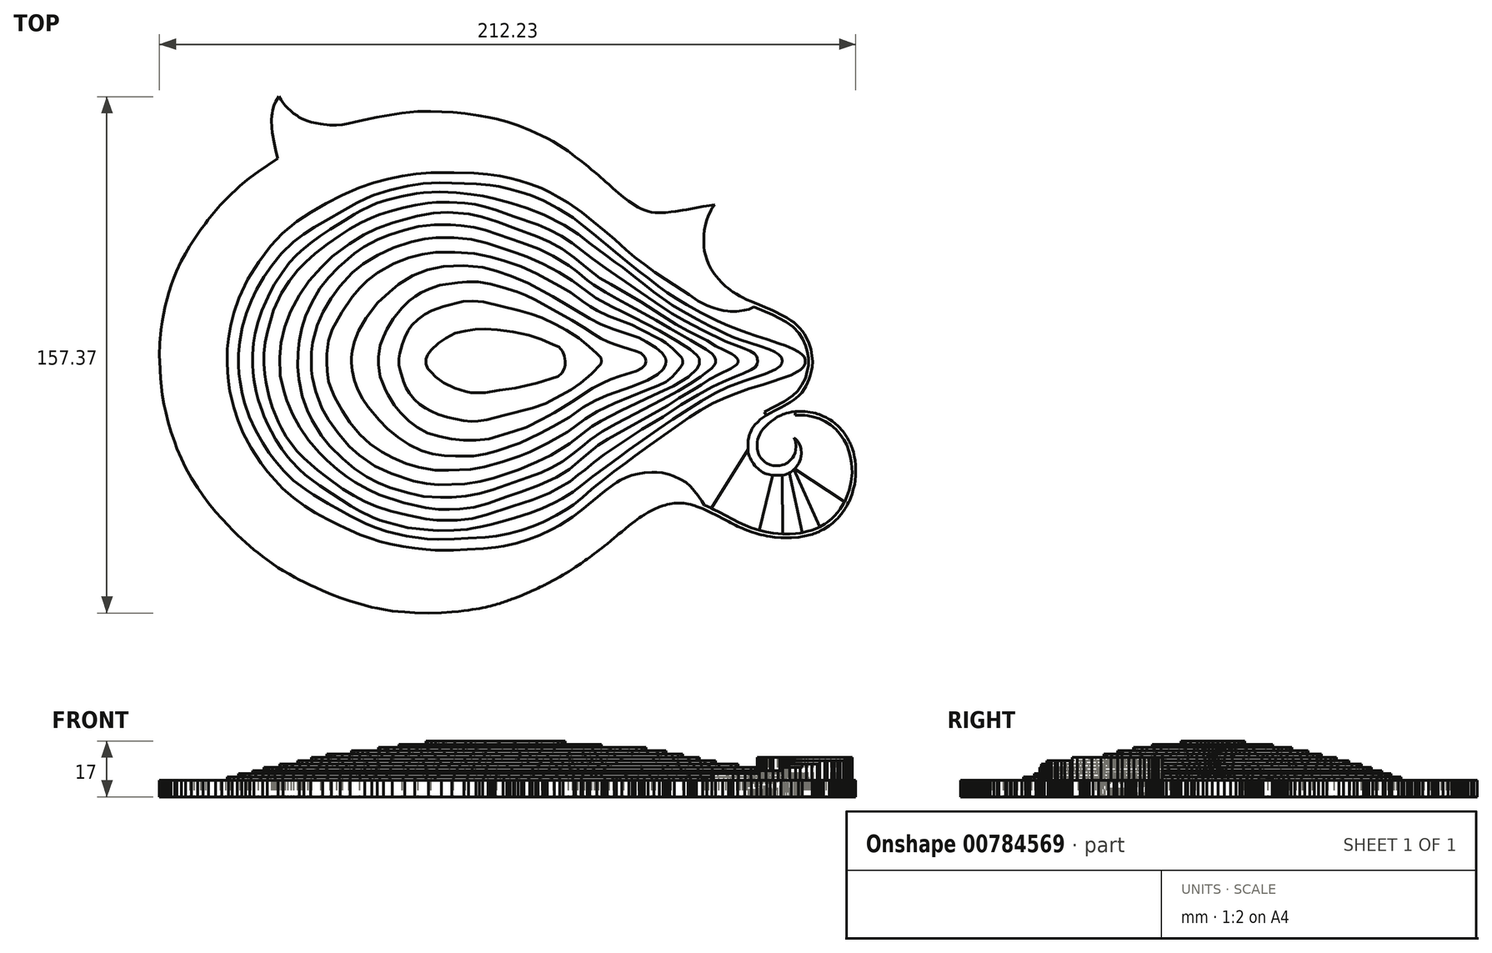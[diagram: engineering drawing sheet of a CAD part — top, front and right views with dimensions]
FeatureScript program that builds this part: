
annotation { "Feature Type Name" : "Feature", "Feature Type Description" : "" }
export const myFeature = defineFeature(function(context is Context, id is Id, definition is map)
    precondition{}
    {
        {
            var Q0;
            Q0=qCreatedBy(makeId("Top.planeOp"),FACE);
            var sketch = newSketch(context, id + "F0", { "sketchPlane" : qUnion([Q0])});
            skLineSegment(sketch, "E0.MirrorCS", {"start": v(99.6, -273.9) * mm, "end": v(99.87, -273.72) * mm});
            skLineSegment(sketch, "E1.MirrorCS", {"start": v(99.87, -273.72) * mm, "end": v(100.2, -273.5) * mm});
            skLineSegment(sketch, "E2.MirrorCS", {"start": v(90.61, -246.87) * mm, "end": v(90.25, -246.1) * mm});
            skLineSegment(sketch, "E3.MirrorCS", {"start": v(97.35, -275.01) * mm, "end": v(97.85, -274.82) * mm});
            skLineSegment(sketch, "E4.MirrorCS", {"start": v(89.29, -252.91) * mm, "end": v(89.86, -252.2) * mm});
            skLineSegment(sketch, "E5.MirrorCS", {"start": v(95.23, -275.73) * mm, "end": v(95.84, -275.58) * mm});
            skLineSegment(sketch, "E6.MirrorCS", {"start": v(101.86, -270.8) * mm, "end": v(102.62, -270) * mm});
            skLineSegment(sketch, "E7.MirrorCS", {"start": v(106.09, -267.45) * mm, "end": v(106.36, -266.93) * mm});
            skLineSegment(sketch, "E8.MirrorCS", {"start": v(100.2, -273.5) * mm, "end": v(100.44, -273.35) * mm});
            skLineSegment(sketch, "E9.MirrorCS", {"start": v(90.25, -246.1) * mm, "end": v(90.81, -246.52) * mm});
            skLineSegment(sketch, "E10.MirrorCS", {"start": v(104.72, -269.4) * mm, "end": v(105.05, -268.97) * mm});
            skLineSegment(sketch, "E11.MirrorCS", {"start": v(108.03, -263.16) * mm, "end": v(108.19, -262.59) * mm});
            skLineSegment(sketch, "E12.MirrorCS", {"start": v(97.85, -274.82) * mm, "end": v(98.18, -274.6) * mm});
            skLineSegment(sketch, "E13.MirrorCS", {"start": v(90.61, -250.7) * mm, "end": v(90.8, -249.93) * mm});
            skLineSegment(sketch, "E14.MirrorCS", {"start": v(103.58, -270.74) * mm, "end": v(103.97, -270.34) * mm});
            skLineSegment(sketch, "E15.MirrorCS", {"start": v(89.86, -252.2) * mm, "end": v(90.22, -251.64) * mm});
            skLineSegment(sketch, "E16.MirrorCS", {"start": v(95.84, -275.58) * mm, "end": v(96.38, -275.37) * mm});
            skLineSegment(sketch, "E17.MirrorCS", {"start": v(102.45, -271.83) * mm, "end": v(102.83, -271.47) * mm});
            skLineSegment(sketch, "E18.MirrorCS", {"start": v(107.11, -265.56) * mm, "end": v(107.27, -265.15) * mm});
            skLineSegment(sketch, "E19.MirrorCS", {"start": v(3.33, -295.73) * mm, "end": v(3.76, -295.55) * mm});
            skLineSegment(sketch, "E20.MirrorCS", {"start": v(106.36, -266.93) * mm, "end": v(106.56, -266.53) * mm});
            skLineSegment(sketch, "E21.MirrorCS", {"start": v(91.71, -247.61) * mm, "end": v(92.2, -248.6) * mm});
            skLineSegment(sketch, "E22.MirrorCS", {"start": v(76.9, -244.77) * mm, "end": v(77.11, -244.24) * mm});
            skLineSegment(sketch, "E23.MirrorCS", {"start": v(100.44, -273.35) * mm, "end": v(100.76, -273.14) * mm});
            skLineSegment(sketch, "E24.MirrorCS", {"start": v(105.8, -267.9) * mm, "end": v(106.09, -267.45) * mm});
            skLineSegment(sketch, "E25.MirrorCS", {"start": v(91.16, -246.85) * mm, "end": v(91.38, -247.1) * mm});
            skLineSegment(sketch, "E26.MirrorCS", {"start": v(90.81, -246.52) * mm, "end": v(91.16, -246.85) * mm});
            skLineSegment(sketch, "E27.MirrorCS", {"start": v(82.4, -241.9) * mm, "end": v(81.84, -242.5) * mm});
            skLineSegment(sketch, "E28.MirrorCS", {"start": v(105.05, -268.97) * mm, "end": v(105.27, -268.64) * mm});
            skLineSegment(sketch, "E29.MirrorCS", {"start": v(106.88, -246.87) * mm, "end": v(106.51, -246.12) * mm});
            skLineSegment(sketch, "E30.MirrorCS", {"start": v(108.58, -261.1) * mm, "end": v(108.77, -260.34) * mm});
            skLineSegment(sketch, "E31.MirrorCS", {"start": v(81.3, -238.26) * mm, "end": v(82.28, -237.75) * mm});
            skLineSegment(sketch, "E32.MirrorCS", {"start": v(90.8, -247.4) * mm, "end": v(90.61, -246.87) * mm});
            skLineSegment(sketch, "E33.MirrorCS", {"start": v(92.13, -275.21) * mm, "end": v(92.88, -275.05) * mm});
            skLineSegment(sketch, "E34.MirrorCS", {"start": v(90.98, -248.7) * mm, "end": v(90.8, -247.4) * mm});
            skLineSegment(sketch, "E35.MirrorCS", {"start": v(108.19, -262.59) * mm, "end": v(108.38, -261.85) * mm});
            skLineSegment(sketch, "E36.MirrorCS", {"start": v(84.64, -240.23) * mm, "end": v(84.04, -240.62) * mm});
            skLineSegment(sketch, "E37.MirrorCS", {"start": v(98.18, -274.6) * mm, "end": v(98.93, -274.27) * mm});
            skLineSegment(sketch, "E38.MirrorCS", {"start": v(83.02, -238.7) * mm, "end": v(84.5, -237.95) * mm});
            skLineSegment(sketch, "E39.MirrorCS", {"start": v(90.8, -249.93) * mm, "end": v(90.98, -248.7) * mm});
            skLineSegment(sketch, "E40.MirrorCS", {"start": v(103.97, -270.34) * mm, "end": v(104.3, -270) * mm});
            skLineSegment(sketch, "E41.MirrorCS", {"start": v(81.92, -239.26) * mm, "end": v(83.02, -238.7) * mm});
            skLineSegment(sketch, "E42.MirrorCS", {"start": v(95.82, -224.6) * mm, "end": v(95.98, -222.96) * mm});
            skLineSegment(sketch, "E43.MirrorCS", {"start": v(107.82, -263.72) * mm, "end": v(108.03, -263.16) * mm});
            skLineSegment(sketch, "E44.MirrorCS", {"start": v(94.48, -239.43) * mm, "end": v(93.59, -239.33) * mm});
            skLineSegment(sketch, "E45.MirrorCS", {"start": v(90.22, -251.64) * mm, "end": v(90.61, -250.7) * mm});
            skLineSegment(sketch, "E46.MirrorCS", {"start": v(86.9, -239.1) * mm, "end": v(86.52, -239.26) * mm});
            skLineSegment(sketch, "E47.MirrorCS", {"start": v(107.27, -265.15) * mm, "end": v(107.48, -264.6) * mm});
            skLineSegment(sketch, "E48.MirrorCS", {"start": v(108.01, -249.29) * mm, "end": v(107.83, -248.86) * mm});
            skLineSegment(sketch, "E49.MirrorCS", {"start": v(96.38, -275.37) * mm, "end": v(96.9, -275.2) * mm});
            skLineSegment(sketch, "E50.MirrorCS", {"start": v(102.83, -271.47) * mm, "end": v(103.22, -271.1) * mm});
            skLineSegment(sketch, "E51.MirrorCS", {"start": v(3.76, -295.55) * mm, "end": v(4.3, -295.36) * mm});
            skLineSegment(sketch, "E52.MirrorCS", {"start": v(94.86, -228.32) * mm, "end": v(95.23, -227.18) * mm});
            skLineSegment(sketch, "E53.MirrorCS", {"start": v(104.4, -267.86) * mm, "end": v(105.38, -266.22) * mm});
            skLineSegment(sketch, "E54.MirrorCS", {"start": v(92.62, -250.96) * mm, "end": v(92.3, -252.6) * mm});
            skLineSegment(sketch, "E55.MirrorCS", {"start": v(88.77, -238.5) * mm, "end": v(88, -238.69) * mm});
            skLineSegment(sketch, "E56.MirrorCS", {"start": v(103.59, -268.9) * mm, "end": v(104.4, -267.86) * mm});
            skLineSegment(sketch, "E57.MirrorCS", {"start": v(92.49, -249.48) * mm, "end": v(92.62, -250.96) * mm});
            skLineSegment(sketch, "E58.MirrorCS", {"start": v(93.95, -230.35) * mm, "end": v(94.5, -229.25) * mm});
            skLineSegment(sketch, "E59.MirrorCS", {"start": v(89.67, -238.32) * mm, "end": v(88.77, -238.5) * mm});
            skLineSegment(sketch, "E60.MirrorCS", {"start": v(94.53, -275.9) * mm, "end": v(95.23, -275.73) * mm});
            skLineSegment(sketch, "E61.MirrorCS", {"start": v(101.53, -272.59) * mm, "end": v(102.06, -272.15) * mm});
            skLineSegment(sketch, "E62.MirrorCS", {"start": v(106.56, -266.53) * mm, "end": v(106.9, -265.9) * mm});
            skLineSegment(sketch, "E63.MirrorCS", {"start": v(108.55, -251.1) * mm, "end": v(108.4, -250.5) * mm});
            skLineSegment(sketch, "E64.MirrorCS", {"start": v(2.24, -296.12) * mm, "end": v(2.77, -295.92) * mm});
            skLineSegment(sketch, "E65.MirrorCS", {"start": v(93.8, -227.93) * mm, "end": v(94.39, -225.67) * mm});
            skLineSegment(sketch, "E66.MirrorCS", {"start": v(90.62, -238.15) * mm, "end": v(89.67, -238.32) * mm});
            skLineSegment(sketch, "E67.MirrorCS", {"start": v(92.2, -248.6) * mm, "end": v(92.49, -249.48) * mm});
            skLineSegment(sketch, "E68.MirrorCS", {"start": v(80.77, -256.67) * mm, "end": v(80.27, -256.3) * mm});
            skLineSegment(sketch, "E69.MirrorCS", {"start": v(77.11, -244.24) * mm, "end": v(77.28, -243.86) * mm});
            skLineSegment(sketch, "E70.MirrorCS", {"start": v(100.76, -273.14) * mm, "end": v(101.02, -272.97) * mm});
            skLineSegment(sketch, "E71.MirrorCS", {"start": v(105.25, -244.28) * mm, "end": v(104.87, -243.87) * mm});
            skLineSegment(sketch, "E72.MirrorCS", {"start": v(99.69, -272.45) * mm, "end": v(100.48, -271.9) * mm});
            skLineSegment(sketch, "E73.MirrorCS", {"start": v(91.38, -247.1) * mm, "end": v(91.71, -247.61) * mm});
            skLineSegment(sketch, "E74.MirrorCS", {"start": v(91.65, -276.49) * mm, "end": v(92.87, -276.3) * mm});
            skLineSegment(sketch, "E75.MirrorCS", {"start": v(96.17, -238.52) * mm, "end": v(95.23, -238.36) * mm});
            skLineSegment(sketch, "E76.MirrorCS", {"start": v(96.9, -238.71) * mm, "end": v(96.17, -238.52) * mm});
            skLineSegment(sketch, "E77.MirrorCS", {"start": v(81.84, -242.5) * mm, "end": v(81, -243.32) * mm});
            skLineSegment(sketch, "E78.MirrorCS", {"start": v(105.27, -268.64) * mm, "end": v(105.47, -268.33) * mm});
            skLineSegment(sketch, "E79.MirrorCS", {"start": v(-0.71, -297.05) * mm, "end": v(-0.14, -296.88) * mm});
            skLineSegment(sketch, "E80.MirrorCS", {"start": v(97.38, -273.66) * mm, "end": v(98.18, -273.35) * mm});
            skLineSegment(sketch, "E81.MirrorCS", {"start": v(90.23, -234.62) * mm, "end": v(90.97, -234.07) * mm});
            skLineSegment(sketch, "E82.MirrorCS", {"start": v(106.51, -246.12) * mm, "end": v(106.17, -245.6) * mm});
            skLineSegment(sketch, "E83.MirrorCS", {"start": v(108.77, -260.34) * mm, "end": v(108.94, -259.25) * mm});
            skLineSegment(sketch, "E84.MirrorCS", {"start": v(89.12, -235.38) * mm, "end": v(90.23, -234.62) * mm});
            skLineSegment(sketch, "E85.MirrorCS", {"start": v(98.03, -239.06) * mm, "end": v(97.46, -238.86) * mm});
            skLineSegment(sketch, "E86.MirrorCS", {"start": v(81.92, -253.9) * mm, "end": v(82.64, -254.23) * mm});
            skLineSegment(sketch, "E87.MirrorCS", {"start": v(99.32, -274.09) * mm, "end": v(99.6, -273.9) * mm});
            skLineSegment(sketch, "E88.MirrorCS", {"start": v(-2.2, -297.42) * mm, "end": v(-1.47, -297.24) * mm});
            skLineSegment(sketch, "E89.MirrorCS", {"start": v(81.92, -239.26) * mm, "end": v(81.3, -238.26) * mm});
            skLineSegment(sketch, "E90.MirrorCS", {"start": v(92.88, -275.05) * mm, "end": v(94.15, -274.78) * mm});
            skLineSegment(sketch, "E91.MirrorCS", {"start": v(86.54, -236.85) * mm, "end": v(89.12, -235.38) * mm});
            skLineSegment(sketch, "E92.MirrorCS", {"start": v(108.38, -261.85) * mm, "end": v(108.58, -261.1) * mm});
            skLineSegment(sketch, "E93.MirrorCS", {"start": v(84.04, -240.62) * mm, "end": v(83.28, -241.18) * mm});
            skLineSegment(sketch, "E94.MirrorCS", {"start": v(98.93, -274.27) * mm, "end": v(99.32, -274.09) * mm});
            skLineSegment(sketch, "E95.MirrorCS", {"start": v(104.54, -269.62) * mm, "end": v(104.72, -269.4) * mm});
            skLineSegment(sketch, "E96.MirrorCS", {"start": v(90.62, -239.35) * mm, "end": v(90.62, -238.15) * mm});
            skLineSegment(sketch, "E97.MirrorCS", {"start": v(84.5, -237.95) * mm, "end": v(86.54, -236.85) * mm});
            skLineSegment(sketch, "E98.MirrorCS", {"start": v(95.8, -221.16) * mm, "end": v(95.45, -219.22) * mm});
            skLineSegment(sketch, "E99.MirrorCS", {"start": v(80.97, -253.15) * mm, "end": v(81.37, -253.53) * mm});
            skLineSegment(sketch, "E100.MirrorCS", {"start": v(104.3, -270) * mm, "end": v(104.54, -269.62) * mm});
            skLineSegment(sketch, "E101.MirrorCS", {"start": v(-3.73, -297.78) * mm, "end": v(-2.94, -297.6) * mm});
            skLineSegment(sketch, "E102.MirrorCS", {"start": v(99.71, -227.6) * mm, "end": v(100.8, -227.29) * mm});
            skLineSegment(sketch, "E103.MirrorCS", {"start": v(107.12, -262) * mm, "end": v(107.65, -259.57) * mm});
            skLineSegment(sketch, "E104.MirrorCS", {"start": v(91.95, -239.27) * mm, "end": v(90.62, -239.35) * mm});
            skLineSegment(sketch, "E105.MirrorCS", {"start": v(95.98, -222.96) * mm, "end": v(95.8, -221.16) * mm});
            skLineSegment(sketch, "E106.MirrorCS", {"start": v(107.45, -247.97) * mm, "end": v(107.27, -247.56) * mm});
            skLineSegment(sketch, "E107.MirrorCS", {"start": v(85.24, -239.83) * mm, "end": v(84.64, -240.23) * mm});
            skLineSegment(sketch, "E108.MirrorCS", {"start": v(106.42, -264.05) * mm, "end": v(107.12, -262) * mm});
            skLineSegment(sketch, "E109.MirrorCS", {"start": v(93.59, -239.33) * mm, "end": v(91.95, -239.27) * mm});
            skLineSegment(sketch, "E110.MirrorCS", {"start": v(79.86, -251.83) * mm, "end": v(80.23, -252.4) * mm});
            skLineSegment(sketch, "E111.MirrorCS", {"start": v(77.36, -253.15) * mm, "end": v(76.92, -252.28) * mm});
            skLineSegment(sketch, "E112.MirrorCS", {"start": v(95.1, -227.6) * mm, "end": v(99.71, -227.6) * mm});
            skLineSegment(sketch, "E113.MirrorCS", {"start": v(86.52, -239.26) * mm, "end": v(85.24, -239.83) * mm});
            skLineSegment(sketch, "E114.MirrorCS", {"start": v(105.75, -265.65) * mm, "end": v(106.42, -264.05) * mm});
            skLineSegment(sketch, "E115.MirrorCS", {"start": v(95.64, -225.7) * mm, "end": v(95.82, -224.6) * mm});
            skLineSegment(sketch, "E116.MirrorCS", {"start": v(107.48, -264.6) * mm, "end": v(107.82, -263.72) * mm});
            skLineSegment(sketch, "E117.MirrorCS", {"start": v(107.83, -248.86) * mm, "end": v(107.62, -248.34) * mm});
            skLineSegment(sketch, "E118.MirrorCS", {"start": v(96.9, -275.2) * mm, "end": v(97.35, -275.01) * mm});
            skLineSegment(sketch, "E119.MirrorCS", {"start": v(103.22, -271.1) * mm, "end": v(103.58, -270.74) * mm});
            skLineSegment(sketch, "E120.MirrorCS", {"start": v(4.3, -295.36) * mm, "end": v(4.8, -295.17) * mm});
            skLineSegment(sketch, "E121.MirrorCS", {"start": v(79.3, -241.27) * mm, "end": v(80.05, -240.58) * mm});
            skLineSegment(sketch, "E122.MirrorCS", {"start": v(95.23, -227.18) * mm, "end": v(95.64, -225.7) * mm});
            skLineSegment(sketch, "E123.MirrorCS", {"start": v(79.3, -250.57) * mm, "end": v(79.48, -251.07) * mm});
            skLineSegment(sketch, "E124.MirrorCS", {"start": v(78.38, -254.64) * mm, "end": v(77.95, -254.05) * mm});
            skLineSegment(sketch, "E125.MirrorCS", {"start": v(87.42, -238.88) * mm, "end": v(86.9, -239.1) * mm});
            skLineSegment(sketch, "E126.MirrorCS", {"start": v(105.38, -266.22) * mm, "end": v(105.75, -265.65) * mm});
            skLineSegment(sketch, "E127.MirrorCS", {"start": v(96.16, -239.75) * mm, "end": v(94.48, -239.43) * mm});
            skLineSegment(sketch, "E128.MirrorCS", {"start": v(94.79, -221.9) * mm, "end": v(94.3, -219.9) * mm});
            skLineSegment(sketch, "E129.MirrorCS", {"start": v(88, -238.69) * mm, "end": v(87.42, -238.88) * mm});
            skLineSegment(sketch, "E130.MirrorCS", {"start": v(79.11, -249.6) * mm, "end": v(79.3, -250.57) * mm});
            skLineSegment(sketch, "E131.MirrorCS", {"start": v(94.7, -224.21) * mm, "end": v(94.79, -221.9) * mm});
            skLineSegment(sketch, "E132.MirrorCS", {"start": v(94.5, -229.25) * mm, "end": v(94.86, -228.32) * mm});
            skLineSegment(sketch, "E133.MirrorCS", {"start": v(102.06, -272.15) * mm, "end": v(102.45, -271.83) * mm});
            skLineSegment(sketch, "E134.MirrorCS", {"start": v(106.9, -265.9) * mm, "end": v(107.11, -265.56) * mm});
            skLineSegment(sketch, "E135.MirrorCS", {"start": v(108.4, -250.5) * mm, "end": v(108.2, -249.88) * mm});
            skLineSegment(sketch, "E136.MirrorCS", {"start": v(2.77, -295.92) * mm, "end": v(3.33, -295.73) * mm});
            skLineSegment(sketch, "E137.MirrorCS", {"start": v(94.39, -225.67) * mm, "end": v(94.7, -224.21) * mm});
            skLineSegment(sketch, "E138.MirrorCS", {"start": v(98.18, -273.35) * mm, "end": v(98.56, -274.43) * mm});
            skLineSegment(sketch, "E139.MirrorCS", {"start": v(80.27, -256.3) * mm, "end": v(79.74, -255.91) * mm});
            skLineSegment(sketch, "E140.MirrorCS", {"start": v(77.28, -243.86) * mm, "end": v(77.49, -243.47) * mm});
            skLineSegment(sketch, "E141.MirrorCS", {"start": v(104.1, -243.03) * mm, "end": v(103.71, -242.63) * mm});
            skLineSegment(sketch, "E142.MirrorCS", {"start": v(102.62, -270) * mm, "end": v(103.59, -268.9) * mm});
            skLineSegment(sketch, "E143.MirrorCS", {"start": v(79.5, -246.07) * mm, "end": v(79.3, -246.67) * mm});
            skLineSegment(sketch, "E144.MirrorCS", {"start": v(87.46, -254.25) * mm, "end": v(87.84, -254.08) * mm});
            skLineSegment(sketch, "E145.MirrorCS", {"start": v(93.77, -276.08) * mm, "end": v(94.53, -275.9) * mm});
            skLineSegment(sketch, "E146.MirrorCS", {"start": v(101.02, -272.97) * mm, "end": v(101.53, -272.59) * mm});
            skLineSegment(sketch, "E147.MirrorCS", {"start": v(92.76, -230) * mm, "end": v(93.8, -227.93) * mm});
            skLineSegment(sketch, "E148.MirrorCS", {"start": v(92.87, -276.3) * mm, "end": v(93.77, -276.08) * mm});
            skLineSegment(sketch, "E149.MirrorCS", {"start": v(100.48, -271.9) * mm, "end": v(101.86, -270.8) * mm});
            skLineSegment(sketch, "E150.MirrorCS", {"start": v(104.2, -244.95) * mm, "end": v(103.05, -243.67) * mm});
            skLineSegment(sketch, "E151.MirrorCS", {"start": v(93.74, -238.15) * mm, "end": v(90.62, -238.15) * mm});
            skLineSegment(sketch, "E152.MirrorCS", {"start": v(65.18, -267.67) * mm, "end": v(64.5, -268.73) * mm});
            skLineSegment(sketch, "E153.MirrorCS", {"start": v(82.07, -257.18) * mm, "end": v(81.5, -257.02) * mm});
            skLineSegment(sketch, "E154.MirrorCS", {"start": v(95.23, -238.36) * mm, "end": v(93.74, -238.15) * mm});
            skLineSegment(sketch, "E155.MirrorCS", {"start": v(80.42, -244.1) * mm, "end": v(79.86, -245.14) * mm});
            skLineSegment(sketch, "E156.MirrorCS", {"start": v(85.97, -254.63) * mm, "end": v(86.9, -254.44) * mm});
            skLineSegment(sketch, "E157.MirrorCS", {"start": v(87.4, -235.1) * mm, "end": v(89.9, -233.35) * mm});
            skLineSegment(sketch, "E158.MirrorCS", {"start": v(98.18, -273.35) * mm, "end": v(99.69, -272.45) * mm});
            skLineSegment(sketch, "E159.MirrorCS", {"start": v(-0.14, -296.88) * mm, "end": v(0.57, -296.66) * mm});
            skLineSegment(sketch, "E160.MirrorCS", {"start": v(105.78, -245) * mm, "end": v(105.6, -244.81) * mm});
            skLineSegment(sketch, "E161.MirrorCS", {"start": v(81, -243.32) * mm, "end": v(80.42, -244.1) * mm});
            skLineSegment(sketch, "E162.MirrorCS", {"start": v(105.47, -268.33) * mm, "end": v(105.8, -267.9) * mm});
            skLineSegment(sketch, "E163.MirrorCS", {"start": v(76.35, -247.04) * mm, "end": v(76.53, -245.94) * mm});
            skLineSegment(sketch, "E164.MirrorCS", {"start": v(90.97, -234.07) * mm, "end": v(91.76, -233.38) * mm});
            skLineSegment(sketch, "E165.MirrorCS", {"start": v(106.17, -245.6) * mm, "end": v(105.78, -245) * mm});
            skLineSegment(sketch, "E166.MirrorCS", {"start": v(84.64, -236.53) * mm, "end": v(87.4, -235.1) * mm});
            skLineSegment(sketch, "E167.MirrorCS", {"start": v(97.46, -238.86) * mm, "end": v(96.9, -238.71) * mm});
            skLineSegment(sketch, "E168.MirrorCS", {"start": v(82.64, -254.23) * mm, "end": v(83.04, -254.43) * mm});
            skLineSegment(sketch, "E169.MirrorCS", {"start": v(-1.47, -297.24) * mm, "end": v(-0.71, -297.05) * mm});
            skLineSegment(sketch, "E170.MirrorCS", {"start": v(82.28, -237.75) * mm, "end": v(84.64, -236.53) * mm});
            skLineSegment(sketch, "E171.MirrorCS", {"start": v(95.73, -274.34) * mm, "end": v(97.38, -273.66) * mm});
            skLineSegment(sketch, "E172.MirrorCS", {"start": v(87.47, -257.42) * mm, "end": v(86.72, -257.6) * mm});
            skLineSegment(sketch, "E173.MirrorCS", {"start": v(76.35, -250.37) * mm, "end": v(76.35, -249.7) * mm});
            skLineSegment(sketch, "E174.MirrorCS", {"start": v(83.28, -241.18) * mm, "end": v(82.4, -241.9) * mm});
            skLineSegment(sketch, "E175.MirrorCS", {"start": v(94.15, -274.78) * mm, "end": v(95.73, -274.34) * mm});
            skLineSegment(sketch, "E176.MirrorCS", {"start": v(81.37, -253.53) * mm, "end": v(81.92, -253.9) * mm});
            skLineSegment(sketch, "E177.MirrorCS", {"start": v(88.56, -257.01) * mm, "end": v(87.47, -257.42) * mm});
            skLineSegment(sketch, "E178.MirrorCS", {"start": v(76.5, -251.1) * mm, "end": v(76.35, -250.37) * mm});
            skLineSegment(sketch, "E179.MirrorCS", {"start": v(107.08, -247.18) * mm, "end": v(106.88, -246.87) * mm});
            skLineSegment(sketch, "E180.MirrorCS", {"start": v(98.56, -239.26) * mm, "end": v(98.03, -239.06) * mm});
            skLineSegment(sketch, "E181.MirrorCS", {"start": v(-2.94, -297.6) * mm, "end": v(-2.2, -297.42) * mm});
            skLineSegment(sketch, "E182.MirrorCS", {"start": v(76.73, -251.83) * mm, "end": v(76.5, -251.1) * mm});
            skLineSegment(sketch, "E183.MirrorCS", {"start": v(107.27, -247.56) * mm, "end": v(107.08, -247.18) * mm});
            skLineSegment(sketch, "E184.MirrorCS", {"start": v(67.47, -270.2) * mm, "end": v(68.58, -270.76) * mm});
            skLineSegment(sketch, "E185.MirrorCS", {"start": v(6.15, -294.64) * mm, "end": v(7.18, -294.24) * mm});
            skLineSegment(sketch, "E186.MirrorCS", {"start": v(80.23, -252.4) * mm, "end": v(80.97, -253.15) * mm});
            skLineSegment(sketch, "E187.MirrorCS", {"start": v(76.92, -252.28) * mm, "end": v(76.73, -251.83) * mm});
            skLineSegment(sketch, "E188.MirrorCS", {"start": v(5.22, -295.01) * mm, "end": v(6.15, -294.64) * mm});
            skLineSegment(sketch, "E189.MirrorCS", {"start": v(-4.64, -297.99) * mm, "end": v(-3.73, -297.78) * mm});
            skLineSegment(sketch, "E190.MirrorCS", {"start": v(90.55, -255.66) * mm, "end": v(89.89, -256.23) * mm});
            skLineSegment(sketch, "E191.MirrorCS", {"start": v(107.62, -248.34) * mm, "end": v(107.45, -247.97) * mm});
            skLineSegment(sketch, "E192.MirrorCS", {"start": v(100.79, -240.38) * mm, "end": v(100.06, -239.99) * mm});
            skLineSegment(sketch, "E193.MirrorCS", {"start": v(4.8, -295.17) * mm, "end": v(5.22, -295.01) * mm});
            skLineSegment(sketch, "E194.MirrorCS", {"start": v(80.05, -240.58) * mm, "end": v(81.92, -239.26) * mm});
            skLineSegment(sketch, "E195.MirrorCS", {"start": v(79.48, -251.07) * mm, "end": v(79.86, -251.83) * mm});
            skLineSegment(sketch, "E196.MirrorCS", {"start": v(77.95, -254.05) * mm, "end": v(77.36, -253.15) * mm});
            skLineSegment(sketch, "E197.MirrorCS", {"start": v(85.52, -275.4) * mm, "end": v(86.83, -275.47) * mm});
            skLineSegment(sketch, "E198.MirrorCS", {"start": v(92.3, -252.6) * mm, "end": v(91.8, -253.92) * mm});
            skLineSegment(sketch, "E199.MirrorCS", {"start": v(79.34, -255.53) * mm, "end": v(78.38, -254.64) * mm});
            skLineSegment(sketch, "E200.MirrorCS", {"start": v(78.37, -242.22) * mm, "end": v(79.3, -241.27) * mm});
            skLineSegment(sketch, "E201.MirrorCS", {"start": v(102.83, -241.84) * mm, "end": v(101.9, -241.13) * mm});
            skLineSegment(sketch, "E202.MirrorCS", {"start": v(108.2, -249.88) * mm, "end": v(108.01, -249.29) * mm});
            skLineSegment(sketch, "E203.MirrorCS", {"start": v(2.25, -294.84) * mm, "end": v(7.3, -292.96) * mm});
            skLineSegment(sketch, "E204.MirrorCS", {"start": v(98.05, -240.3) * mm, "end": v(96.16, -239.75) * mm});
            skLineSegment(sketch, "E205.MirrorCS", {"start": v(79.74, -255.91) * mm, "end": v(79.34, -255.53) * mm});
            skLineSegment(sketch, "E206.MirrorCS", {"start": v(77.49, -243.47) * mm, "end": v(78.37, -242.22) * mm});
            skLineSegment(sketch, "E207.MirrorCS", {"start": v(103.71, -242.63) * mm, "end": v(102.83, -241.84) * mm});
            skLineSegment(sketch, "E208.MirrorCS", {"start": v(79.11, -247.43) * mm, "end": v(79.11, -249.6) * mm});
            skLineSegment(sketch, "E209.MirrorCS", {"start": v(60.6, -267.07) * mm, "end": v(61.14, -267.28) * mm});
            skLineSegment(sketch, "E210.MirrorCS", {"start": v(-2.85, -296.34) * mm, "end": v(2.25, -294.84) * mm});
            skLineSegment(sketch, "E211.MirrorCS", {"start": v(99.77, -241.22) * mm, "end": v(98.05, -240.3) * mm});
            skLineSegment(sketch, "E212.MirrorCS", {"start": v(-66.45, -142.53) * mm, "end": v(-66.63, -142.2) * mm});
            skLineSegment(sketch, "E213.MirrorCS", {"start": v(79.3, -246.67) * mm, "end": v(79.11, -247.43) * mm});
            skLineSegment(sketch, "E214.MirrorCS", {"start": v(87.84, -254.08) * mm, "end": v(88.4, -253.71) * mm});
            skLineSegment(sketch, "E215.MirrorCS", {"start": v(13.73, -291.3) * mm, "end": v(14.1, -291.1) * mm});
            skLineSegment(sketch, "E216.MirrorCS", {"start": v(101.41, -242.2) * mm, "end": v(99.77, -241.22) * mm});
            skLineSegment(sketch, "E217.MirrorCS", {"start": v(104.87, -243.87) * mm, "end": v(104.1, -243.03) * mm});
            skLineSegment(sketch, "E218.MirrorCS", {"start": v(108.76, -251.96) * mm, "end": v(108.55, -251.1) * mm});
            skLineSegment(sketch, "E219.MirrorCS", {"start": v(59.5, -266.66) * mm, "end": v(60.07, -266.88) * mm});
            skLineSegment(sketch, "E220.MirrorCS", {"start": v(1.69, -296.33) * mm, "end": v(2.24, -296.12) * mm});
            skLineSegment(sketch, "E221.MirrorCS", {"start": v(103.05, -243.67) * mm, "end": v(101.41, -242.2) * mm});
            skLineSegment(sketch, "E222.MirrorCS", {"start": v(108.94, -252.95) * mm, "end": v(108.76, -251.96) * mm});
            skLineSegment(sketch, "E223.MirrorCS", {"start": v(58.84, -266.5) * mm, "end": v(59.5, -266.66) * mm});
            skLineSegment(sketch, "E224.MirrorCS", {"start": v(1.1, -296.5) * mm, "end": v(1.69, -296.33) * mm});
            skLineSegment(sketch, "E225.MirrorCS", {"start": v(64.5, -268.73) * mm, "end": v(65.18, -267.67) * mm});
            skLineSegment(sketch, "E226.MirrorCS", {"start": v(-64.78, -144.91) * mm, "end": v(-65.59, -143.92) * mm});
            skLineSegment(sketch, "E227.MirrorCS", {"start": v(81.5, -257.02) * mm, "end": v(80.77, -256.67) * mm});
            skLineSegment(sketch, "E228.MirrorCS", {"start": v(79.86, -245.14) * mm, "end": v(79.5, -246.07) * mm});
            skLineSegment(sketch, "E229.MirrorCS", {"start": v(86.9, -254.44) * mm, "end": v(87.46, -254.25) * mm});
            skLineSegment(sketch, "E230.MirrorCS", {"start": v(0.57, -296.66) * mm, "end": v(1.1, -296.5) * mm});
            skLineSegment(sketch, "E231.MirrorCS", {"start": v(105.5, -246.8) * mm, "end": v(104.2, -244.95) * mm});
            skLineSegment(sketch, "E232.MirrorCS", {"start": v(76.72, -245.27) * mm, "end": v(76.9, -244.77) * mm});
            skLineSegment(sketch, "E233.MirrorCS", {"start": v(105.6, -244.81) * mm, "end": v(105.25, -244.28) * mm});
            skLineSegment(sketch, "E234.MirrorCS", {"start": v(65.75, -267.95) * mm, "end": v(65.18, -267.67) * mm});
            skLineSegment(sketch, "E235.MirrorCS", {"start": v(106.39, -248.36) * mm, "end": v(105.5, -246.8) * mm});
            skLineSegment(sketch, "E236.MirrorCS", {"start": v(82.63, -257.38) * mm, "end": v(82.07, -257.18) * mm});
            skLineSegment(sketch, "E237.MirrorCS", {"start": v(76.53, -245.94) * mm, "end": v(76.72, -245.27) * mm});
            skLineSegment(sketch, "E238.MirrorCS", {"start": v(91.76, -233.38) * mm, "end": v(92.64, -232.4) * mm});
            skLineSegment(sketch, "E239.MirrorCS", {"start": v(83.93, -254.63) * mm, "end": v(85.97, -254.63) * mm});
            skLineSegment(sketch, "E240.MirrorCS", {"start": v(56.75, -266.12) * mm, "end": v(58, -266.3) * mm});
            skLineSegment(sketch, "E241.MirrorCS", {"start": v(83.6, -257.57) * mm, "end": v(82.63, -257.38) * mm});
            skLineSegment(sketch, "E242.MirrorCS", {"start": v(83.04, -254.43) * mm, "end": v(83.93, -254.63) * mm});
            skLineSegment(sketch, "E243.MirrorCS", {"start": v(108.94, -259.25) * mm, "end": v(109.14, -257.55) * mm});
            skLineSegment(sketch, "E244.MirrorCS", {"start": v(62.85, -178.67) * mm, "end": v(63.7, -176.8) * mm});
            skLineSegment(sketch, "E245.MirrorCS", {"start": v(107.06, -250.32) * mm, "end": v(106.39, -248.36) * mm});
            skLineSegment(sketch, "E246.MirrorCS", {"start": v(86.72, -257.6) * mm, "end": v(83.6, -257.57) * mm});
            skLineSegment(sketch, "E247.MirrorCS", {"start": v(76.35, -249.7) * mm, "end": v(76.35, -247.04) * mm});
            skLineSegment(sketch, "E248.MirrorCS", {"start": v(52.44, -266.3) * mm, "end": v(53.83, -266.12) * mm});
            skLineSegment(sketch, "E249.MirrorCS", {"start": v(107.45, -251.72) * mm, "end": v(107.06, -250.32) * mm});
            skLineSegment(sketch, "E250.MirrorCS", {"start": v(69.63, -271.33) * mm, "end": v(70.34, -271.7) * mm});
            skLineSegment(sketch, "E251.MirrorCS", {"start": v(107.85, -253.78) * mm, "end": v(107.45, -251.72) * mm});
            skLineSegment(sketch, "E252.MirrorCS", {"start": v(68.58, -270.76) * mm, "end": v(69.63, -271.33) * mm});
            skLineSegment(sketch, "E253.MirrorCS", {"start": v(107.65, -259.57) * mm, "end": v(108.03, -256.85) * mm});
            skLineSegment(sketch, "E254.MirrorCS", {"start": v(99.32, -239.63) * mm, "end": v(98.56, -239.26) * mm});
            skLineSegment(sketch, "E255.MirrorCS", {"start": v(90.8, -275.38) * mm, "end": v(92.13, -275.21) * mm});
            skLineSegment(sketch, "E256.MirrorCS", {"start": v(65.02, -176.8) * mm, "end": v(65.44, -176.06) * mm});
            skLineSegment(sketch, "E257.MirrorCS", {"start": v(89.89, -256.23) * mm, "end": v(89.28, -256.63) * mm});
            skLineSegment(sketch, "E258.MirrorCS", {"start": v(100.06, -239.99) * mm, "end": v(99.32, -239.63) * mm});
            skLineSegment(sketch, "E259.MirrorCS", {"start": v(66.37, -269.64) * mm, "end": v(67.47, -270.2) * mm});
            skLineSegment(sketch, "E260.MirrorCS", {"start": v(89.04, -275.46) * mm, "end": v(90.8, -275.38) * mm});
            skLineSegment(sketch, "E261.MirrorCS", {"start": v(65.25, -269.1) * mm, "end": v(66.37, -269.64) * mm});
            skLineSegment(sketch, "E262.MirrorCS", {"start": v(-5.54, -298.16) * mm, "end": v(-4.64, -297.99) * mm});
            skLineSegment(sketch, "E263.MirrorCS", {"start": v(86.83, -275.47) * mm, "end": v(89.04, -275.46) * mm});
            skLineSegment(sketch, "E264.MirrorCS", {"start": v(101.34, -240.7) * mm, "end": v(100.79, -240.38) * mm});
            skLineSegment(sketch, "E265.MirrorCS", {"start": v(63.71, -267) * mm, "end": v(65.18, -267.67) * mm});
            skLineSegment(sketch, "E266.MirrorCS", {"start": v(63.76, -268.37) * mm, "end": v(65.25, -269.1) * mm});
            skLineSegment(sketch, "E267.MirrorCS", {"start": v(-6.64, -298.34) * mm, "end": v(-5.54, -298.16) * mm});
            skLineSegment(sketch, "E268.MirrorCS", {"start": v(63.74, -179.76) * mm, "end": v(64.12, -178.68) * mm});
            skLineSegment(sketch, "E269.MirrorCS", {"start": v(91.8, -253.92) * mm, "end": v(91.2, -254.84) * mm});
            skLineSegment(sketch, "E270.MirrorCS", {"start": v(101.9, -241.13) * mm, "end": v(101.34, -240.7) * mm});
            skLineSegment(sketch, "E271.MirrorCS", {"start": v(62.45, -267.78) * mm, "end": v(63.76, -268.37) * mm});
            skLineSegment(sketch, "E272.MirrorCS", {"start": v(61.36, -265.85) * mm, "end": v(63.71, -267) * mm});
            skLineSegment(sketch, "E273.MirrorCS", {"start": v(61.14, -267.28) * mm, "end": v(62.45, -267.78) * mm});
            skLineSegment(sketch, "E274.MirrorCS", {"start": v(58.52, -265.16) * mm, "end": v(61.36, -265.85) * mm});
            skLineSegment(sketch, "E275.MirrorCS", {"start": v(-66.63, -142.2) * mm, "end": v(-67.15, -142.98) * mm});
            skLineSegment(sketch, "E276.MirrorCS", {"start": v(88.4, -253.71) * mm, "end": v(89.29, -252.91) * mm});
            skLineSegment(sketch, "E277.MirrorCS", {"start": v(14.1, -291.1) * mm, "end": v(14.48, -290.92) * mm});
            skLineSegment(sketch, "E278.MirrorCS", {"start": v(55.36, -264.8) * mm, "end": v(58.52, -265.16) * mm});
            skLineSegment(sketch, "E279.MirrorCS", {"start": v(81.75, -274.87) * mm, "end": v(83.87, -275.19) * mm});
            skLineSegment(sketch, "E280.MirrorCS", {"start": v(60.07, -266.88) * mm, "end": v(60.6, -267.07) * mm});
            skLineSegment(sketch, "E281.MirrorCS", {"start": v(52.87, -265.02) * mm, "end": v(55.36, -264.8) * mm});
            skLineSegment(sketch, "E282.MirrorCS", {"start": v(63.02, -182.96) * mm, "end": v(63.2, -182.05) * mm});
            skLineSegment(sketch, "E283.MirrorCS", {"start": v(-65.59, -143.92) * mm, "end": v(-66.09, -143.15) * mm});
            skLineSegment(sketch, "E284.MirrorCS", {"start": v(54.17, -177.17) * mm, "end": v(52.8, -177.37) * mm});
            skLineSegment(sketch, "E285.MirrorCS", {"start": v(93.2, -231.62) * mm, "end": v(93.6, -231.1) * mm});
            skLineSegment(sketch, "E286.MirrorCS", {"start": v(58, -266.3) * mm, "end": v(58.84, -266.5) * mm});
            skLineSegment(sketch, "E287.MirrorCS", {"start": v(92.64, -232.4) * mm, "end": v(93.2, -231.62) * mm});
            skLineSegment(sketch, "E288.MirrorCS", {"start": v(109.14, -254.6) * mm, "end": v(108.94, -252.95) * mm});
            skLineSegment(sketch, "E289.MirrorCS", {"start": v(63.7, -176.8) * mm, "end": v(61.62, -177.1) * mm});
            skLineSegment(sketch, "E290.MirrorCS", {"start": v(-63.04, -146.6) * mm, "end": v(-64.03, -145.74) * mm});
            skLineSegment(sketch, "E291.MirrorCS", {"start": v(89.56, -276.69) * mm, "end": v(91.65, -276.49) * mm});
            skLineSegment(sketch, "E292.MirrorCS", {"start": v(87.37, -276.69) * mm, "end": v(89.56, -276.69) * mm});
            skLineSegment(sketch, "E293.MirrorCS", {"start": v(53.83, -266.12) * mm, "end": v(56.75, -266.12) * mm});
            skLineSegment(sketch, "E294.MirrorCS", {"start": v(67.68, -268.94) * mm, "end": v(65.75, -267.95) * mm});
            skLineSegment(sketch, "E295.MirrorCS", {"start": v(86.3, -276.69) * mm, "end": v(87.37, -276.69) * mm});
            skLineSegment(sketch, "E296.MirrorCS", {"start": v(62.3, -180.12) * mm, "end": v(62.85, -178.67) * mm});
            skLineSegment(sketch, "E297.MirrorCS", {"start": v(69.26, -269.75) * mm, "end": v(67.68, -268.94) * mm});
            skLineSegment(sketch, "E298.MirrorCS", {"start": v(84.44, -276.48) * mm, "end": v(86.3, -276.69) * mm});
            skLineSegment(sketch, "E299.MirrorCS", {"start": v(61.87, -181.89) * mm, "end": v(62.3, -180.12) * mm});
            skLineSegment(sketch, "E300.MirrorCS", {"start": v(-60.53, -148.43) * mm, "end": v(-61.13, -148) * mm});
            skLineSegment(sketch, "E301.MirrorCS", {"start": v(63.62, -175.53) * mm, "end": v(62.64, -175.72) * mm});
            skLineSegment(sketch, "E302.MirrorCS", {"start": v(108.03, -256.85) * mm, "end": v(107.85, -253.78) * mm});
            skLineSegment(sketch, "E303.MirrorCS", {"start": v(61.62, -184.47) * mm, "end": v(61.87, -181.89) * mm});
            skLineSegment(sketch, "E304.MirrorCS", {"start": v(66.11, -175.14) * mm, "end": v(63.62, -175.53) * mm});
            skLineSegment(sketch, "E305.MirrorCS", {"start": v(83.05, -276.29) * mm, "end": v(84.44, -276.48) * mm});
            skLineSegment(sketch, "E306.MirrorCS", {"start": v(61.55, -186.62) * mm, "end": v(61.62, -184.47) * mm});
            skLineSegment(sketch, "E307.MirrorCS", {"start": v(-68.74, -147.33) * mm, "end": v(-68.85, -148.02) * mm});
            skLineSegment(sketch, "E308.MirrorCS", {"start": v(65.44, -176.06) * mm, "end": v(66.11, -175.14) * mm});
            skLineSegment(sketch, "E309.MirrorCS", {"start": v(89.28, -256.63) * mm, "end": v(88.56, -257.01) * mm});
            skLineSegment(sketch, "E310.MirrorCS", {"start": v(50.4, -266.85) * mm, "end": v(50.98, -266.67) * mm});
            skLineSegment(sketch, "E311.MirrorCS", {"start": v(-68.55, -146.34) * mm, "end": v(-68.74, -147.33) * mm});
            skLineSegment(sketch, "E312.MirrorCS", {"start": v(81.16, -275.92) * mm, "end": v(82.02, -276.1) * mm});
            skLineSegment(sketch, "E313.MirrorCS", {"start": v(-68.15, -144.96) * mm, "end": v(-68.55, -146.34) * mm});
            skLineSegment(sketch, "E314.MirrorCS", {"start": v(64.53, -177.84) * mm, "end": v(65.02, -176.8) * mm});
            skLineSegment(sketch, "E315.MirrorCS", {"start": v(-67.65, -143.76) * mm, "end": v(-68.15, -144.96) * mm});
            skLineSegment(sketch, "E316.MirrorCS", {"start": v(64.12, -178.68) * mm, "end": v(64.53, -177.84) * mm});
            skLineSegment(sketch, "E317.MirrorCS", {"start": v(45.94, -177.18) * mm, "end": v(44.83, -176.84) * mm});
            skLineSegment(sketch, "E318.MirrorCS", {"start": v(91.2, -254.84) * mm, "end": v(90.55, -255.66) * mm});
            skLineSegment(sketch, "E319.MirrorCS", {"start": v(-67.15, -142.98) * mm, "end": v(-67.65, -143.76) * mm});
            skLineSegment(sketch, "E320.MirrorCS", {"start": v(78.95, -275.37) * mm, "end": v(79.7, -275.57) * mm});
            skLineSegment(sketch, "E321.MirrorCS", {"start": v(-7.74, -298.53) * mm, "end": v(-6.64, -298.34) * mm});
            skLineSegment(sketch, "E322.MirrorCS", {"start": v(63.4, -181.1) * mm, "end": v(63.74, -179.76) * mm});
            skLineSegment(sketch, "E323.MirrorCS", {"start": v(48.02, -177.54) * mm, "end": v(46.9, -177.42) * mm});
            skLineSegment(sketch, "E324.MirrorCS", {"start": v(-8.97, -298.74) * mm, "end": v(-7.74, -298.53) * mm});
            skLineSegment(sketch, "E325.MirrorCS", {"start": v(14.48, -290.92) * mm, "end": v(14.85, -290.7) * mm});
            skLineSegment(sketch, "E326.MirrorCS", {"start": v(101.3, -218.53) * mm, "end": v(100.23, -218.1) * mm});
            skLineSegment(sketch, "E327.MirrorCS", {"start": v(83.87, -275.19) * mm, "end": v(85.52, -275.4) * mm});
            skLineSegment(sketch, "E328.MirrorCS", {"start": v(63.2, -182.05) * mm, "end": v(63.4, -181.1) * mm});
            skLineSegment(sketch, "E329.MirrorCS", {"start": v(-10.35, -298.9) * mm, "end": v(-8.97, -298.74) * mm});
            skLineSegment(sketch, "E330.MirrorCS", {"start": v(52.1, -178.72) * mm, "end": v(50.75, -178.87) * mm});
            skLineSegment(sketch, "E331.MirrorCS", {"start": v(-11.98, -299.07) * mm, "end": v(-10.35, -298.9) * mm});
            skLineSegment(sketch, "E332.MirrorCS", {"start": v(-8.26, -297.43) * mm, "end": v(-2.85, -296.34) * mm});
            skLineSegment(sketch, "E333.MirrorCS", {"start": v(53.64, -178.5) * mm, "end": v(52.1, -178.72) * mm});
            skLineSegment(sketch, "E334.MirrorCS", {"start": v(-66.09, -143.15) * mm, "end": v(-66.45, -142.53) * mm});
            skLineSegment(sketch, "E335.MirrorCS", {"start": v(52.8, -177.37) * mm, "end": v(51.19, -177.54) * mm});
            skLineSegment(sketch, "E336.MirrorCS", {"start": v(-12.96, -297.99) * mm, "end": v(-8.26, -297.43) * mm});
            skLineSegment(sketch, "E337.MirrorCS", {"start": v(56.44, -178.03) * mm, "end": v(53.64, -178.5) * mm});
            skLineSegment(sketch, "E338.MirrorCS", {"start": v(90.98, -211.64) * mm, "end": v(90.23, -211.03) * mm});
            skLineSegment(sketch, "E339.MirrorCS", {"start": v(62.84, -184.26) * mm, "end": v(63.02, -182.96) * mm});
            skLineSegment(sketch, "E340.MirrorCS", {"start": v(93.6, -231.1) * mm, "end": v(93.95, -230.35) * mm});
            skLineSegment(sketch, "E341.MirrorCS", {"start": v(91.46, -231.98) * mm, "end": v(92.76, -230) * mm});
            skLineSegment(sketch, "E342.MirrorCS", {"start": v(58.74, -177.62) * mm, "end": v(56.44, -178.03) * mm});
            skLineSegment(sketch, "E343.MirrorCS", {"start": v(62.84, -188.01) * mm, "end": v(62.84, -184.26) * mm});
            skLineSegment(sketch, "E344.MirrorCS", {"start": v(56.36, -176.84) * mm, "end": v(54.17, -177.17) * mm});
            skLineSegment(sketch, "E345.MirrorCS", {"start": v(89.9, -233.35) * mm, "end": v(91.46, -231.98) * mm});
            skLineSegment(sketch, "E346.MirrorCS", {"start": v(61.62, -177.1) * mm, "end": v(58.74, -177.62) * mm});
            skLineSegment(sketch, "E347.MirrorCS", {"start": v(-64.03, -145.74) * mm, "end": v(-64.78, -144.91) * mm});
            skLineSegment(sketch, "E348.MirrorCS", {"start": v(57.47, -176.64) * mm, "end": v(56.36, -176.84) * mm});
            skLineSegment(sketch, "E349.MirrorCS", {"start": v(92.92, -213.75) * mm, "end": v(92.06, -212.7) * mm});
            skLineSegment(sketch, "E350.MirrorCS", {"start": v(59.5, -176.28) * mm, "end": v(57.47, -176.64) * mm});
            skLineSegment(sketch, "E351.MirrorCS", {"start": v(109.14, -257.55) * mm, "end": v(109.14, -254.6) * mm});
            skLineSegment(sketch, "E352.MirrorCS", {"start": v(61.56, -175.92) * mm, "end": v(59.5, -176.28) * mm});
            skLineSegment(sketch, "E353.MirrorCS", {"start": v(-62.21, -147.3) * mm, "end": v(-63.04, -146.6) * mm});
            skLineSegment(sketch, "E354.MirrorCS", {"start": v(62.64, -175.72) * mm, "end": v(61.56, -175.92) * mm});
            skLineSegment(sketch, "E355.MirrorCS", {"start": v(70.34, -271.7) * mm, "end": v(71, -272.05) * mm});
            skLineSegment(sketch, "E356.MirrorCS", {"start": v(-61.13, -148) * mm, "end": v(-62.21, -147.3) * mm});
            skLineSegment(sketch, "E357.MirrorCS", {"start": v(51.63, -266.5) * mm, "end": v(52.44, -266.3) * mm});
            skLineSegment(sketch, "E358.MirrorCS", {"start": v(7.98, -293.9) * mm, "end": v(8.88, -293.54) * mm});
            skLineSegment(sketch, "E359.MirrorCS", {"start": v(50.98, -266.67) * mm, "end": v(51.63, -266.5) * mm});
            skLineSegment(sketch, "E360.MirrorCS", {"start": v(82.02, -276.1) * mm, "end": v(83.05, -276.29) * mm});
            skLineSegment(sketch, "E361.MirrorCS", {"start": v(43.83, -176.42) * mm, "end": v(42.76, -175.9) * mm});
            skLineSegment(sketch, "E362.MirrorCS", {"start": v(49.3, -267.22) * mm, "end": v(50.4, -266.85) * mm});
            skLineSegment(sketch, "E363.MirrorCS", {"start": v(44.83, -176.84) * mm, "end": v(43.83, -176.42) * mm});
            skLineSegment(sketch, "E364.MirrorCS", {"start": v(80.27, -275.73) * mm, "end": v(81.16, -275.92) * mm});
            skLineSegment(sketch, "E365.MirrorCS", {"start": v(94.3, -219.9) * mm, "end": v(93.81, -218.1) * mm});
            skLineSegment(sketch, "E366.MirrorCS", {"start": v(46.53, -268.52) * mm, "end": v(47.63, -267.97) * mm});
            skLineSegment(sketch, "E367.MirrorCS", {"start": v(46.9, -177.42) * mm, "end": v(45.94, -177.18) * mm});
            skLineSegment(sketch, "E368.MirrorCS", {"start": v(100.23, -218.1) * mm, "end": v(99.35, -218.03) * mm});
            skLineSegment(sketch, "E369.MirrorCS", {"start": v(48.13, -178.77) * mm, "end": v(45.18, -178.24) * mm});
            skLineSegment(sketch, "E370.MirrorCS", {"start": v(14.85, -290.7) * mm, "end": v(15.16, -290.55) * mm});
            skLineSegment(sketch, "E371.MirrorCS", {"start": v(88.1, -209.58) * mm, "end": v(87.3, -209.16) * mm});
            skLineSegment(sketch, "E372.MirrorCS", {"start": v(44.7, -269.6) * mm, "end": v(45.78, -268.9) * mm});
            skLineSegment(sketch, "E373.MirrorCS", {"start": v(50.75, -178.87) * mm, "end": v(48.13, -178.77) * mm});
            skLineSegment(sketch, "E374.MirrorCS", {"start": v(51.19, -177.54) * mm, "end": v(48.02, -177.54) * mm});
            skLineSegment(sketch, "E375.MirrorCS", {"start": v(75.34, -274.1) * mm, "end": v(76.27, -274.46) * mm});
            skLineSegment(sketch, "E376.MirrorCS", {"start": v(79.8, -274.4) * mm, "end": v(81.75, -274.87) * mm});
            skLineSegment(sketch, "E377.MirrorCS", {"start": v(90.23, -211.03) * mm, "end": v(89.44, -210.46) * mm});
            skLineSegment(sketch, "E378.MirrorCS", {"start": v(72.24, -202.03) * mm, "end": v(71.67, -201.66) * mm});
            skLineSegment(sketch, "E379.MirrorCS", {"start": v(51, -265.4) * mm, "end": v(52.87, -265.02) * mm});
            skLineSegment(sketch, "E380.MirrorCS", {"start": v(49.05, -266.12) * mm, "end": v(51, -265.4) * mm});
            skLineSegment(sketch, "E381.MirrorCS", {"start": v(12.26, -292.05) * mm, "end": v(13, -291.67) * mm});
            skLineSegment(sketch, "E382.MirrorCS", {"start": v(92.06, -212.7) * mm, "end": v(91.64, -212.3) * mm});
            skLineSegment(sketch, "E383.MirrorCS", {"start": v(46.22, -267.35) * mm, "end": v(47.42, -266.73) * mm});
            skLineSegment(sketch, "E384.MirrorCS", {"start": v(71.73, -272.4) * mm, "end": v(72.45, -272.78) * mm});
            skLineSegment(sketch, "E385.MirrorCS", {"start": v(71, -272.05) * mm, "end": v(71.73, -272.4) * mm});
            skLineSegment(sketch, "E386.MirrorCS", {"start": v(9.81, -293.18) * mm, "end": v(10.56, -292.8) * mm});
            skLineSegment(sketch, "E387.MirrorCS", {"start": v(64.3, -193.25) * mm, "end": v(63.75, -191.82) * mm});
            skLineSegment(sketch, "E388.MirrorCS", {"start": v(8.88, -293.54) * mm, "end": v(9.81, -293.18) * mm});
            skLineSegment(sketch, "E389.MirrorCS", {"start": v(102.3, -226.48) * mm, "end": v(103.05, -225.77) * mm});
            skLineSegment(sketch, "E390.MirrorCS", {"start": v(89.99, -212.35) * mm, "end": v(87.92, -210.82) * mm});
            skLineSegment(sketch, "E391.MirrorCS", {"start": v(73.42, -271.91) * mm, "end": v(71.8, -271.08) * mm});
            skLineSegment(sketch, "E392.MirrorCS", {"start": v(-68.85, -148.02) * mm, "end": v(-68.91, -149.41) * mm});
            skLineSegment(sketch, "E393.MirrorCS", {"start": v(95.45, -219.22) * mm, "end": v(94.89, -217.32) * mm});
            skLineSegment(sketch, "E394.MirrorCS", {"start": v(7.18, -294.24) * mm, "end": v(7.98, -293.9) * mm});
            skLineSegment(sketch, "E395.MirrorCS", {"start": v(100.8, -227.29) * mm, "end": v(101.7, -226.84) * mm});
            skLineSegment(sketch, "E396.MirrorCS", {"start": v(91.87, -214.3) * mm, "end": v(89.99, -212.35) * mm});
            skLineSegment(sketch, "E397.MirrorCS", {"start": v(75.45, -272.86) * mm, "end": v(73.42, -271.91) * mm});
            skLineSegment(sketch, "E398.MirrorCS", {"start": v(42.76, -175.9) * mm, "end": v(41.94, -175.37) * mm});
            skLineSegment(sketch, "E399.MirrorCS", {"start": v(92.97, -216.03) * mm, "end": v(91.87, -214.3) * mm});
            skLineSegment(sketch, "E400.MirrorCS", {"start": v(61.65, -188.26) * mm, "end": v(61.55, -186.62) * mm});
            skLineSegment(sketch, "E401.MirrorCS", {"start": v(77.22, -273.57) * mm, "end": v(75.45, -272.86) * mm});
            skLineSegment(sketch, "E402.MirrorCS", {"start": v(42.97, -177.4) * mm, "end": v(40.9, -176.2) * mm});
            skLineSegment(sketch, "E403.MirrorCS", {"start": v(93.81, -218.1) * mm, "end": v(92.97, -216.03) * mm});
            skLineSegment(sketch, "E404.MirrorCS", {"start": v(62.04, -190.26) * mm, "end": v(61.65, -188.26) * mm});
            skLineSegment(sketch, "E405.MirrorCS", {"start": v(27.49, -163.44) * mm, "end": v(26.44, -162.6) * mm});
            skLineSegment(sketch, "E406.MirrorCS", {"start": v(79.8, -274.4) * mm, "end": v(79.53, -275.53) * mm});
            skLineSegment(sketch, "E407.MirrorCS", {"start": v(47.63, -267.97) * mm, "end": v(49.3, -267.22) * mm});
            skLineSegment(sketch, "E408.MirrorCS", {"start": v(62.82, -192.53) * mm, "end": v(62.04, -190.26) * mm});
            skLineSegment(sketch, "E409.MirrorCS", {"start": v(69.49, -199.98) * mm, "end": v(69.08, -199.6) * mm});
            skLineSegment(sketch, "E410.MirrorCS", {"start": v(11.39, -291.1) * mm, "end": v(15.62, -289) * mm});
            skLineSegment(sketch, "E411.MirrorCS", {"start": v(99.35, -218.03) * mm, "end": v(95.1, -218.07) * mm});
            skLineSegment(sketch, "E412.MirrorCS", {"start": v(45.18, -178.24) * mm, "end": v(42.97, -177.4) * mm});
            skLineSegment(sketch, "E413.MirrorCS", {"start": v(15.16, -290.55) * mm, "end": v(17.26, -289.43) * mm});
            skLineSegment(sketch, "E414.MirrorCS", {"start": v(87.3, -209.16) * mm, "end": v(86.38, -208.62) * mm});
            skLineSegment(sketch, "E415.MirrorCS", {"start": v(7.3, -292.96) * mm, "end": v(11.39, -291.1) * mm});
            skLineSegment(sketch, "E416.MirrorCS", {"start": v(63.35, -194.06) * mm, "end": v(62.82, -192.53) * mm});
            skLineSegment(sketch, "E417.MirrorCS", {"start": v(45.78, -268.9) * mm, "end": v(46.53, -268.52) * mm});
            skLineSegment(sketch, "E418.MirrorCS", {"start": v(77.28, -274.84) * mm, "end": v(78.95, -275.37) * mm});
            skLineSegment(sketch, "E419.MirrorCS", {"start": v(89.44, -210.46) * mm, "end": v(88.1, -209.58) * mm});
            skLineSegment(sketch, "E420.MirrorCS", {"start": v(71.67, -201.66) * mm, "end": v(70.97, -201.15) * mm});
            skLineSegment(sketch, "E421.MirrorCS", {"start": v(76.27, -274.46) * mm, "end": v(77.28, -274.84) * mm});
            skLineSegment(sketch, "E422.MirrorCS", {"start": v(-68.07, -161.79) * mm, "end": v(-68.96, -162.37) * mm});
            skLineSegment(sketch, "E423.MirrorCS", {"start": v(103.05, -219.91) * mm, "end": v(102.4, -219.18) * mm});
            skLineSegment(sketch, "E424.MirrorCS", {"start": v(-67.05, -161.12) * mm, "end": v(-68.07, -161.79) * mm});
            skLineSegment(sketch, "E425.MirrorCS", {"start": v(74.47, -273.72) * mm, "end": v(75.34, -274.1) * mm});
            skLineSegment(sketch, "E426.MirrorCS", {"start": v(13, -291.67) * mm, "end": v(13.73, -291.3) * mm});
            skLineSegment(sketch, "E427.MirrorCS", {"start": v(67.1, -199.45) * mm, "end": v(66.2, -198.49) * mm});
            skLineSegment(sketch, "E428.MirrorCS", {"start": v(-67.4, -159.7) * mm, "end": v(-67.05, -161.12) * mm});
            skLineSegment(sketch, "E429.MirrorCS", {"start": v(73.2, -273.16) * mm, "end": v(74.47, -273.72) * mm});
            skLineSegment(sketch, "E430.MirrorCS", {"start": v(-67.72, -158.41) * mm, "end": v(-67.4, -159.7) * mm});
            skLineSegment(sketch, "E431.MirrorCS", {"start": v(91.64, -212.3) * mm, "end": v(90.98, -211.64) * mm});
            skLineSegment(sketch, "E432.MirrorCS", {"start": v(47.42, -266.73) * mm, "end": v(49.05, -266.12) * mm});
            skLineSegment(sketch, "E433.MirrorCS", {"start": v(104.04, -222.83) * mm, "end": v(103.98, -222) * mm});
            skLineSegment(sketch, "E434.MirrorCS", {"start": v(72.45, -272.78) * mm, "end": v(73.2, -273.16) * mm});
            skLineSegment(sketch, "E435.MirrorCS", {"start": v(11.48, -292.39) * mm, "end": v(12.26, -292.05) * mm});
            skLineSegment(sketch, "E436.MirrorCS", {"start": v(-68.13, -156.45) * mm, "end": v(-67.72, -158.41) * mm});
            skLineSegment(sketch, "E437.MirrorCS", {"start": v(74.47, -203.34) * mm, "end": v(73.73, -202.94) * mm});
            skLineSegment(sketch, "E438.MirrorCS", {"start": v(63.02, -189.2) * mm, "end": v(62.84, -188.01) * mm});
            skLineSegment(sketch, "E439.MirrorCS", {"start": v(10.56, -292.8) * mm, "end": v(11.48, -292.39) * mm});
            skLineSegment(sketch, "E440.MirrorCS", {"start": v(-68.3, -155.5) * mm, "end": v(-68.13, -156.45) * mm});
            skLineSegment(sketch, "E441.MirrorCS", {"start": v(63.34, -190.52) * mm, "end": v(63.02, -189.2) * mm});
            skLineSegment(sketch, "E442.MirrorCS", {"start": v(25.95, -284.07) * mm, "end": v(26.7, -283.53) * mm});
            skLineSegment(sketch, "E443.MirrorCS", {"start": v(93.48, -214.5) * mm, "end": v(92.92, -213.75) * mm});
            skLineSegment(sketch, "E444.MirrorCS", {"start": v(63.75, -191.82) * mm, "end": v(63.34, -190.52) * mm});
            skLineSegment(sketch, "E445.MirrorCS", {"start": v(-68.72, -153.16) * mm, "end": v(-68.3, -155.5) * mm});
            skLineSegment(sketch, "E446.MirrorCS", {"start": v(94.1, -215.61) * mm, "end": v(93.48, -214.5) * mm});
            skLineSegment(sketch, "E447.MirrorCS", {"start": v(-68.85, -151.64) * mm, "end": v(-68.72, -153.16) * mm});
            skLineSegment(sketch, "E448.MirrorCS", {"start": v(71.8, -271.08) * mm, "end": v(69.26, -269.75) * mm});
            skLineSegment(sketch, "E449.MirrorCS", {"start": v(-68.91, -149.41) * mm, "end": v(-68.85, -151.64) * mm});
            skLineSegment(sketch, "E450.MirrorCS", {"start": v(94.89, -217.32) * mm, "end": v(94.1, -215.61) * mm});
            skLineSegment(sketch, "E451.MirrorCS", {"start": v(65.03, -194.77) * mm, "end": v(64.3, -193.25) * mm});
            skLineSegment(sketch, "E452.MirrorCS", {"start": v(101.7, -226.84) * mm, "end": v(102.3, -226.48) * mm});
            skLineSegment(sketch, "E453.MirrorCS", {"start": v(65.97, -196.29) * mm, "end": v(65.03, -194.77) * mm});
            skLineSegment(sketch, "E454.MirrorCS", {"start": v(67.25, -197.8) * mm, "end": v(65.97, -196.29) * mm});
            skLineSegment(sketch, "E455.MirrorCS", {"start": v(34.48, -277.57) * mm, "end": v(35.58, -276.66) * mm});
            skLineSegment(sketch, "E456.MirrorCS", {"start": v(26.44, -162.6) * mm, "end": v(25.77, -162.1) * mm});
            skLineSegment(sketch, "E457.MirrorCS", {"start": v(-57.99, -149.64) * mm, "end": v(-58.99, -149.22) * mm});
            skLineSegment(sketch, "E458.MirrorCS", {"start": v(68.34, -198.9) * mm, "end": v(67.25, -197.8) * mm});
            skLineSegment(sketch, "E459.MirrorCS", {"start": v(79.8, -274.4) * mm, "end": v(77.22, -273.57) * mm});
            skLineSegment(sketch, "E460.MirrorCS", {"start": v(69.08, -199.6) * mm, "end": v(68.34, -198.9) * mm});
            skLineSegment(sketch, "E461.MirrorCS", {"start": v(17.26, -289.43) * mm, "end": v(18.92, -288.5) * mm});
            skLineSegment(sketch, "E462.MirrorCS", {"start": v(32.61, -279.09) * mm, "end": v(33.35, -278.52) * mm});
            skLineSegment(sketch, "E463.MirrorCS", {"start": v(79.7, -275.57) * mm, "end": v(80.27, -275.73) * mm});
            skLineSegment(sketch, "E464.MirrorCS", {"start": v(29.44, -165.1) * mm, "end": v(28.62, -164.5) * mm});
            skLineSegment(sketch, "E465.MirrorCS", {"start": v(70.2, -200.5) * mm, "end": v(69.49, -199.98) * mm});
            skLineSegment(sketch, "E466.MirrorCS", {"start": v(70.97, -201.15) * mm, "end": v(70.2, -200.5) * mm});
            skLineSegment(sketch, "E467.MirrorCS", {"start": v(30.2, -280.92) * mm, "end": v(30.95, -280.36) * mm});
            skLineSegment(sketch, "E468.MirrorCS", {"start": v(64, -195.3) * mm, "end": v(63.35, -194.06) * mm});
            skLineSegment(sketch, "E469.MirrorCS", {"start": v(-68.96, -162.37) * mm, "end": v(-71.26, -163.88) * mm});
            skLineSegment(sketch, "E470.MirrorCS", {"start": v(102.4, -219.18) * mm, "end": v(101.3, -218.53) * mm});
            skLineSegment(sketch, "E471.MirrorCS", {"start": v(65.12, -197.13) * mm, "end": v(64, -195.3) * mm});
            skLineSegment(sketch, "E472.MirrorCS", {"start": v(28.74, -282.03) * mm, "end": v(29.46, -281.48) * mm});
            skLineSegment(sketch, "E473.MirrorCS", {"start": v(43.2, -270.56) * mm, "end": v(43.75, -270.2) * mm});
            skLineSegment(sketch, "E474.MirrorCS", {"start": v(66.2, -198.49) * mm, "end": v(65.12, -197.13) * mm});
            skLineSegment(sketch, "E475.MirrorCS", {"start": v(103.64, -220.78) * mm, "end": v(103.05, -219.91) * mm});
            skLineSegment(sketch, "E476.MirrorCS", {"start": v(-14.03, -299.26) * mm, "end": v(-11.98, -299.07) * mm});
            skLineSegment(sketch, "E477.MirrorCS", {"start": v(33.85, -168.99) * mm, "end": v(32.82, -168.14) * mm});
            skLineSegment(sketch, "E478.MirrorCS", {"start": v(72.8, -202.4) * mm, "end": v(72.24, -202.03) * mm});
            skLineSegment(sketch, "E479.MirrorCS", {"start": v(103.98, -222) * mm, "end": v(103.64, -220.78) * mm});
            skLineSegment(sketch, "E480.MirrorCS", {"start": v(-17.19, -298.24) * mm, "end": v(-12.96, -297.99) * mm});
            skLineSegment(sketch, "E481.MirrorCS", {"start": v(-17.13, -299.48) * mm, "end": v(-14.03, -299.26) * mm});
            skLineSegment(sketch, "E482.MirrorCS", {"start": v(68.71, -200.9) * mm, "end": v(67.1, -199.45) * mm});
            skLineSegment(sketch, "E483.MirrorCS", {"start": v(73.73, -202.94) * mm, "end": v(72.8, -202.4) * mm});
            skLineSegment(sketch, "E484.MirrorCS", {"start": v(71.35, -203.03) * mm, "end": v(68.71, -200.9) * mm});
            skLineSegment(sketch, "E485.MirrorCS", {"start": v(26.7, -283.53) * mm, "end": v(27.24, -283.13) * mm});
            skLineSegment(sketch, "E486.MirrorCS", {"start": v(35.94, -170.89) * mm, "end": v(35.18, -170.16) * mm});
            skLineSegment(sketch, "E487.MirrorCS", {"start": v(103.97, -223.9) * mm, "end": v(104.04, -222.83) * mm});
            skLineSegment(sketch, "E488.MirrorCS", {"start": v(73.67, -204.32) * mm, "end": v(71.35, -203.03) * mm});
            skLineSegment(sketch, "E489.MirrorCS", {"start": v(38.92, -273.88) * mm, "end": v(40.03, -272.96) * mm});
            skLineSegment(sketch, "E490.MirrorCS", {"start": v(75.97, -204.05) * mm, "end": v(75.21, -203.7) * mm});
            skLineSegment(sketch, "E491.MirrorCS", {"start": v(103.72, -224.7) * mm, "end": v(103.97, -223.9) * mm});
            skLineSegment(sketch, "E492.MirrorCS", {"start": v(21.5, -158.84) * mm, "end": v(20.4, -158.12) * mm});
            skLineSegment(sketch, "E493.MirrorCS", {"start": v(23.75, -285.55) * mm, "end": v(25.4, -284.47) * mm});
            skLineSegment(sketch, "E494.MirrorCS", {"start": v(36.87, -275.55) * mm, "end": v(37.8, -274.8) * mm});
            skLineSegment(sketch, "E495.MirrorCS", {"start": v(103.05, -225.77) * mm, "end": v(103.72, -224.7) * mm});
            skLineSegment(sketch, "E496.MirrorCS", {"start": v(39.2, -173.52) * mm, "end": v(38.36, -172.9) * mm});
            skLineSegment(sketch, "E497.MirrorCS", {"start": v(23.2, -285.93) * mm, "end": v(23.75, -285.55) * mm});
            skLineSegment(sketch, "E498.MirrorCS", {"start": v(36.14, -276.12) * mm, "end": v(36.87, -275.55) * mm});
            skLineSegment(sketch, "E499.MirrorCS", {"start": v(23.67, -160.5) * mm, "end": v(22.78, -159.77) * mm});
            skLineSegment(sketch, "E500.MirrorCS", {"start": v(39.92, -174.05) * mm, "end": v(39.2, -173.52) * mm});
            skLineSegment(sketch, "E501.MirrorCS", {"start": v(31.17, -278.8) * mm, "end": v(35.74, -275.02) * mm});
            skLineSegment(sketch, "E502.MirrorCS", {"start": v(24.43, -161.05) * mm, "end": v(23.67, -160.5) * mm});
            skLineSegment(sketch, "E503.MirrorCS", {"start": v(-59.78, -148.84) * mm, "end": v(-60.53, -148.43) * mm});
            skLineSegment(sketch, "E504.MirrorCS", {"start": v(41.94, -175.37) * mm, "end": v(39.92, -174.05) * mm});
            skLineSegment(sketch, "E505.MirrorCS", {"start": v(80.78, -206.09) * mm, "end": v(79.48, -205.55) * mm});
            skLineSegment(sketch, "E506.MirrorCS", {"start": v(21.67, -286.86) * mm, "end": v(23.2, -285.93) * mm});
            skLineSegment(sketch, "E507.MirrorCS", {"start": v(35.58, -276.66) * mm, "end": v(36.14, -276.12) * mm});
            skLineSegment(sketch, "E508.MirrorCS", {"start": v(24.52, -283.55) * mm, "end": v(31.17, -278.8) * mm});
            skLineSegment(sketch, "E509.MirrorCS", {"start": v(38.88, -174.88) * mm, "end": v(36.22, -172.76) * mm});
            skLineSegment(sketch, "E510.MirrorCS", {"start": v(-24.47, -147.9) * mm, "end": v(-27.83, -148.17) * mm});
            skLineSegment(sketch, "E511.MirrorCS", {"start": v(25.77, -162.1) * mm, "end": v(24.43, -161.05) * mm});
            skLineSegment(sketch, "E512.MirrorCS", {"start": v(-58.99, -149.22) * mm, "end": v(-59.78, -148.84) * mm});
            skLineSegment(sketch, "E513.MirrorCS", {"start": v(82.6, -206.84) * mm, "end": v(80.78, -206.09) * mm});
            skLineSegment(sketch, "E514.MirrorCS", {"start": v(19.87, -287.96) * mm, "end": v(21.67, -286.86) * mm});
            skLineSegment(sketch, "E515.MirrorCS", {"start": v(19.96, -286.45) * mm, "end": v(24.52, -283.55) * mm});
            skLineSegment(sketch, "E516.MirrorCS", {"start": v(40.9, -176.2) * mm, "end": v(38.88, -174.88) * mm});
            skLineSegment(sketch, "E517.MirrorCS", {"start": v(18.92, -288.5) * mm, "end": v(19.87, -287.96) * mm});
            skLineSegment(sketch, "E518.MirrorCS", {"start": v(33.35, -278.52) * mm, "end": v(34.48, -277.57) * mm});
            skLineSegment(sketch, "E519.MirrorCS", {"start": v(-56.81, -149.96) * mm, "end": v(-57.99, -149.64) * mm});
            skLineSegment(sketch, "E520.MirrorCS", {"start": v(15.62, -289) * mm, "end": v(19.96, -286.45) * mm});
            skLineSegment(sketch, "E521.MirrorCS", {"start": v(28.62, -164.5) * mm, "end": v(27.49, -163.44) * mm});
            skLineSegment(sketch, "E522.MirrorCS", {"start": v(86.38, -208.62) * mm, "end": v(84.69, -207.76) * mm});
            skLineSegment(sketch, "E523.MirrorCS", {"start": v(31.7, -279.82) * mm, "end": v(32.61, -279.09) * mm});
            skLineSegment(sketch, "E524.MirrorCS", {"start": v(-71.26, -163.88) * mm, "end": v(-73.08, -165.08) * mm});
            skLineSegment(sketch, "E525.MirrorCS", {"start": v(30.95, -280.36) * mm, "end": v(31.7, -279.82) * mm});
            skLineSegment(sketch, "E526.MirrorCS", {"start": v(29.46, -281.48) * mm, "end": v(30.2, -280.92) * mm});
            skLineSegment(sketch, "E527.MirrorCS", {"start": v(43.75, -270.2) * mm, "end": v(44.7, -269.6) * mm});
            skLineSegment(sketch, "E528.MirrorCS", {"start": v(31.94, -167.31) * mm, "end": v(30.75, -166.2) * mm});
            skLineSegment(sketch, "E529.MirrorCS", {"start": v(32.82, -168.14) * mm, "end": v(31.94, -167.31) * mm});
            skLineSegment(sketch, "E530.MirrorCS", {"start": v(28, -282.6) * mm, "end": v(28.74, -282.03) * mm});
            skLineSegment(sketch, "E531.MirrorCS", {"start": v(41.9, -271.5) * mm, "end": v(43.2, -270.56) * mm});
            skLineSegment(sketch, "E532.MirrorCS", {"start": v(-63.2, -160.42) * mm, "end": v(-68.8, -163.92) * mm});
            skLineSegment(sketch, "E533.MirrorCS", {"start": v(27.24, -283.13) * mm, "end": v(28, -282.6) * mm});
            skLineSegment(sketch, "E534.MirrorCS", {"start": v(40.96, -272.22) * mm, "end": v(41.9, -271.5) * mm});
            skLineSegment(sketch, "E535.MirrorCS", {"start": v(35.18, -170.16) * mm, "end": v(33.85, -168.99) * mm});
            skLineSegment(sketch, "E536.MirrorCS", {"start": v(-21.33, -298.4) * mm, "end": v(-17.19, -298.24) * mm});
            skLineSegment(sketch, "E537.MirrorCS", {"start": v(40.03, -272.96) * mm, "end": v(40.96, -272.22) * mm});
            skLineSegment(sketch, "E538.MirrorCS", {"start": v(-21.04, -299.57) * mm, "end": v(-17.13, -299.48) * mm});
            skLineSegment(sketch, "E539.MirrorCS", {"start": v(-25.01, -298.3) * mm, "end": v(-21.33, -298.4) * mm});
            skLineSegment(sketch, "E540.MirrorCS", {"start": v(-25.27, -299.47) * mm, "end": v(-21.04, -299.57) * mm});
            skLineSegment(sketch, "E541.MirrorCS", {"start": v(36.8, -171.61) * mm, "end": v(35.94, -170.89) * mm});
            skLineSegment(sketch, "E542.MirrorCS", {"start": v(20.4, -158.12) * mm, "end": v(18.7, -157) * mm});
            skLineSegment(sketch, "E543.MirrorCS", {"start": v(75.21, -203.7) * mm, "end": v(74.47, -203.34) * mm});
            skLineSegment(sketch, "E544.MirrorCS", {"start": v(38.36, -172.9) * mm, "end": v(36.8, -171.61) * mm});
            skLineSegment(sketch, "E545.MirrorCS", {"start": v(25.4, -284.47) * mm, "end": v(25.95, -284.07) * mm});
            skLineSegment(sketch, "E546.MirrorCS", {"start": v(37.8, -274.8) * mm, "end": v(38.92, -273.88) * mm});
            skLineSegment(sketch, "E547.MirrorCS", {"start": v(-28.32, -299.27) * mm, "end": v(-25.27, -299.47) * mm});
            skLineSegment(sketch, "E548.MirrorCS", {"start": v(43.51, -268.82) * mm, "end": v(46.22, -267.35) * mm});
            skLineSegment(sketch, "E549.MirrorCS", {"start": v(-29.51, -297.99) * mm, "end": v(-25.01, -298.3) * mm});
            skLineSegment(sketch, "E550.MirrorCS", {"start": v(75.89, -205.34) * mm, "end": v(73.67, -204.32) * mm});
            skLineSegment(sketch, "E551.MirrorCS", {"start": v(23.58, -161.87) * mm, "end": v(20.48, -159.7) * mm});
            skLineSegment(sketch, "E552.MirrorCS", {"start": v(-25.75, -146.8) * mm, "end": v(-29.27, -147.16) * mm});
            skLineSegment(sketch, "E553.MirrorCS", {"start": v(77.27, -204.63) * mm, "end": v(75.97, -204.05) * mm});
            skLineSegment(sketch, "E554.MirrorCS", {"start": v(-30.42, -299.09) * mm, "end": v(-28.32, -299.27) * mm});
            skLineSegment(sketch, "E555.MirrorCS", {"start": v(39.3, -271.97) * mm, "end": v(43.51, -268.82) * mm});
            skLineSegment(sketch, "E556.MirrorCS", {"start": v(27.14, -164.63) * mm, "end": v(23.58, -161.87) * mm});
            skLineSegment(sketch, "E557.MirrorCS", {"start": v(-24.38, -146.66) * mm, "end": v(-25.75, -146.8) * mm});
            skLineSegment(sketch, "E558.MirrorCS", {"start": v(22.78, -159.77) * mm, "end": v(21.5, -158.84) * mm});
            skLineSegment(sketch, "E559.MirrorCS", {"start": v(-32.18, -298.92) * mm, "end": v(-30.42, -299.09) * mm});
            skLineSegment(sketch, "E560.MirrorCS", {"start": v(35.74, -275.02) * mm, "end": v(39.3, -271.97) * mm});
            skLineSegment(sketch, "E561.MirrorCS", {"start": v(29.54, -166.78) * mm, "end": v(27.14, -164.63) * mm});
            skLineSegment(sketch, "E562.MirrorCS", {"start": v(-20.4, -146.66) * mm, "end": v(-24.38, -146.66) * mm});
            skLineSegment(sketch, "E563.MirrorCS", {"start": v(79.48, -205.55) * mm, "end": v(77.27, -204.63) * mm});
            skLineSegment(sketch, "E564.MirrorCS", {"start": v(-101.71, -235.94) * mm, "end": v(-101.16, -238.55) * mm});
            skLineSegment(sketch, "E565.MirrorCS", {"start": v(-102.23, -233.05) * mm, "end": v(-101.71, -235.94) * mm});
            skLineSegment(sketch, "E566.MirrorCS", {"start": v(-102.78, -228.14) * mm, "end": v(-102.23, -233.05) * mm});
            skLineSegment(sketch, "E567.MirrorCS", {"start": v(84.69, -207.76) * mm, "end": v(83.89, -207.38) * mm});
            skLineSegment(sketch, "E568.MirrorCS", {"start": v(-54.01, -150.51) * mm, "end": v(-56.81, -149.96) * mm});
            skLineSegment(sketch, "E569.MirrorCS", {"start": v(-51.24, -150.9) * mm, "end": v(-54.01, -150.51) * mm});
            skLineSegment(sketch, "E570.MirrorCS", {"start": v(-100.93, -233.62) * mm, "end": v(-100.13, -237.62) * mm});
            skLineSegment(sketch, "E571.MirrorCS", {"start": v(-49.13, -150.9) * mm, "end": v(-51.24, -150.9) * mm});
            skLineSegment(sketch, "E572.MirrorCS", {"start": v(-101.5, -228.64) * mm, "end": v(-100.93, -233.62) * mm});
            skLineSegment(sketch, "E573.MirrorCS", {"start": v(-47.39, -150.72) * mm, "end": v(-49.13, -150.9) * mm});
            skLineSegment(sketch, "E574.MirrorCS", {"start": v(-77.95, -277.07) * mm, "end": v(-76.88, -278) * mm});
            skLineSegment(sketch, "E575.MirrorCS", {"start": v(-101.86, -218.92) * mm, "end": v(-101.86, -224.26) * mm});
            skLineSegment(sketch, "E576.MirrorCS", {"start": v(-101.68, -216.1) * mm, "end": v(-101.86, -218.92) * mm});
            skLineSegment(sketch, "E577.MirrorCS", {"start": v(-103.09, -221.16) * mm, "end": v(-103.01, -222.81) * mm});
            skLineSegment(sketch, "E578.MirrorCS", {"start": v(-103, -217.26) * mm, "end": v(-103.09, -221.16) * mm});
            skLineSegment(sketch, "E579.MirrorCS", {"start": v(18.7, -157) * mm, "end": v(16.9, -155.9) * mm});
            skLineSegment(sketch, "E580.MirrorCS", {"start": v(-49.12, -154.09) * mm, "end": v(-52.36, -155.4) * mm});
            skLineSegment(sketch, "E581.MirrorCS", {"start": v(20.48, -159.7) * mm, "end": v(17.4, -157.68) * mm});
            skLineSegment(sketch, "E582.MirrorCS", {"start": v(-102.6, -213.24) * mm, "end": v(-103, -217.26) * mm});
            skLineSegment(sketch, "E583.MirrorCS", {"start": v(-29.27, -147.16) * mm, "end": v(-31.83, -147.61) * mm});
            skLineSegment(sketch, "E584.MirrorCS", {"start": v(-61.85, -288.66) * mm, "end": v(-60.43, -289.43) * mm});
            skLineSegment(sketch, "E585.MirrorCS", {"start": v(-33.82, -297.5) * mm, "end": v(-29.51, -297.99) * mm});
            skLineSegment(sketch, "E586.MirrorCS", {"start": v(-65.4, -286.68) * mm, "end": v(-63.55, -287.72) * mm});
            skLineSegment(sketch, "E587.MirrorCS", {"start": v(-97.81, -198.42) * mm, "end": v(-98.82, -201.31) * mm});
            skLineSegment(sketch, "E588.MirrorCS", {"start": v(87.92, -210.82) * mm, "end": v(83.77, -208.67) * mm});
            skLineSegment(sketch, "E589.MirrorCS", {"start": v(-101.32, -206.05) * mm, "end": v(-101.9, -208.7) * mm});
            skLineSegment(sketch, "E590.MirrorCS", {"start": v(-81.65, -172.37) * mm, "end": v(-82.94, -173.64) * mm});
            skLineSegment(sketch, "E591.MirrorCS", {"start": v(-91.46, -261.34) * mm, "end": v(-89.82, -263.77) * mm});
            skLineSegment(sketch, "E592.MirrorCS", {"start": v(-93.3, -258.46) * mm, "end": v(-91.46, -261.34) * mm});
            skLineSegment(sketch, "E593.MirrorCS", {"start": v(-95.13, -255.24) * mm, "end": v(-93.3, -258.46) * mm});
            skLineSegment(sketch, "E594.MirrorCS", {"start": v(-96.43, -252.5) * mm, "end": v(-95.13, -255.24) * mm});
            skLineSegment(sketch, "E595.MirrorCS", {"start": v(-97.76, -249.4) * mm, "end": v(-96.43, -252.5) * mm});
            skLineSegment(sketch, "E596.MirrorCS", {"start": v(-98.49, -247.44) * mm, "end": v(-97.76, -249.4) * mm});
            skLineSegment(sketch, "E597.MirrorCS", {"start": v(-99.59, -244.31) * mm, "end": v(-98.49, -247.44) * mm});
            skLineSegment(sketch, "E598.MirrorCS", {"start": v(-100.47, -241.33) * mm, "end": v(-99.59, -244.31) * mm});
            skLineSegment(sketch, "E599.MirrorCS", {"start": v(-101.16, -238.55) * mm, "end": v(-100.47, -241.33) * mm});
            skLineSegment(sketch, "E600.MirrorCS", {"start": v(-103.01, -222.81) * mm, "end": v(-102.78, -228.14) * mm});
            skLineSegment(sketch, "E601.MirrorCS", {"start": v(-85.98, -268.73) * mm, "end": v(-84.1, -270.81) * mm});
            skLineSegment(sketch, "E602.MirrorCS", {"start": v(-89.82, -263.77) * mm, "end": v(-88.1, -266.1) * mm});
            skLineSegment(sketch, "E603.MirrorCS", {"start": v(-42.53, -295.49) * mm, "end": v(-38.6, -296.6) * mm});
            skLineSegment(sketch, "E604.MirrorCS", {"start": v(36.22, -172.76) * mm, "end": v(29.54, -166.78) * mm});
            skLineSegment(sketch, "E605.MirrorCS", {"start": v(-27.83, -148.17) * mm, "end": v(-31.44, -148.74) * mm});
            skLineSegment(sketch, "E606.MirrorCS", {"start": v(-96.52, -195.38) * mm, "end": v(-97.81, -198.42) * mm});
            skLineSegment(sketch, "E607.MirrorCS", {"start": v(-93.69, -255.35) * mm, "end": v(-91.8, -258.63) * mm});
            skLineSegment(sketch, "E608.MirrorCS", {"start": v(-79.36, -170.22) * mm, "end": v(-81.65, -172.37) * mm});
            skLineSegment(sketch, "E609.MirrorCS", {"start": v(-100.75, -203.75) * mm, "end": v(-101.32, -206.05) * mm});
            skLineSegment(sketch, "E610.MirrorCS", {"start": v(-66.95, -285.72) * mm, "end": v(-65.4, -286.68) * mm});
            skLineSegment(sketch, "E611.MirrorCS", {"start": v(-34.77, -298.52) * mm, "end": v(-32.18, -298.92) * mm});
            skLineSegment(sketch, "E612.MirrorCS", {"start": v(-95.3, -252.04) * mm, "end": v(-93.69, -255.35) * mm});
            skLineSegment(sketch, "E613.MirrorCS", {"start": v(-78.57, -169.5) * mm, "end": v(-79.36, -170.22) * mm});
            skLineSegment(sketch, "E614.MirrorCS", {"start": v(-100.21, -201.77) * mm, "end": v(-100.75, -203.75) * mm});
            skLineSegment(sketch, "E615.MirrorCS", {"start": v(-68.8, -284.42) * mm, "end": v(-66.95, -285.72) * mm});
            skLineSegment(sketch, "E616.MirrorCS", {"start": v(-36.65, -298.15) * mm, "end": v(-34.77, -298.52) * mm});
            skLineSegment(sketch, "E617.MirrorCS", {"start": v(-96.84, -248.34) * mm, "end": v(-95.3, -252.04) * mm});
            skLineSegment(sketch, "E618.MirrorCS", {"start": v(-76.31, -167.59) * mm, "end": v(-78.57, -169.5) * mm});
            skLineSegment(sketch, "E619.MirrorCS", {"start": v(-99.44, -199.37) * mm, "end": v(-100.21, -201.77) * mm});
            skLineSegment(sketch, "E620.MirrorCS", {"start": v(-5.9, -147.92) * mm, "end": v(-9.98, -147.35) * mm});
            skLineSegment(sketch, "E621.MirrorCS", {"start": v(83.89, -207.38) * mm, "end": v(82.6, -206.84) * mm});
            skLineSegment(sketch, "E622.MirrorCS", {"start": v(-70.21, -283.41) * mm, "end": v(-68.8, -284.42) * mm});
            skLineSegment(sketch, "E623.MirrorCS", {"start": v(-38.31, -297.8) * mm, "end": v(-36.65, -298.15) * mm});
            skLineSegment(sketch, "E624.MirrorCS", {"start": v(-98.01, -245.2) * mm, "end": v(-96.84, -248.34) * mm});
            skLineSegment(sketch, "E625.MirrorCS", {"start": v(-75.38, -166.81) * mm, "end": v(-76.31, -167.59) * mm});
            skLineSegment(sketch, "E626.MirrorCS", {"start": v(-98.73, -197.37) * mm, "end": v(-99.44, -199.37) * mm});
            skLineSegment(sketch, "E627.MirrorCS", {"start": v(-2.9, -148.47) * mm, "end": v(-5.9, -147.92) * mm});
            skLineSegment(sketch, "E628.MirrorCS", {"start": v(-71.68, -282.33) * mm, "end": v(-70.21, -283.41) * mm});
            skLineSegment(sketch, "E629.MirrorCS", {"start": v(-40.55, -297.25) * mm, "end": v(-38.31, -297.8) * mm});
            skLineSegment(sketch, "E630.MirrorCS", {"start": v(-73.08, -165.08) * mm, "end": v(-75.38, -166.81) * mm});
            skLineSegment(sketch, "E631.MirrorCS", {"start": v(-97.95, -195.5) * mm, "end": v(-98.73, -197.37) * mm});
            skLineSegment(sketch, "E632.MirrorCS", {"start": v(-0.4, -149.05) * mm, "end": v(-2.9, -148.47) * mm});
            skLineSegment(sketch, "E633.MirrorCS", {"start": v(-60.32, -288.13) * mm, "end": v(-57, -289.78) * mm});
            skLineSegment(sketch, "E634.MirrorCS", {"start": v(-99.15, -241.56) * mm, "end": v(-98.01, -245.2) * mm});
            skLineSegment(sketch, "E635.MirrorCS", {"start": v(-87.21, -180.3) * mm, "end": v(-89.88, -184.22) * mm});
            skLineSegment(sketch, "E636.MirrorCS", {"start": v(-73.07, -281.23) * mm, "end": v(-71.68, -282.33) * mm});
            skLineSegment(sketch, "E637.MirrorCS", {"start": v(-42.74, -296.63) * mm, "end": v(-40.55, -297.25) * mm});
            skLineSegment(sketch, "E638.MirrorCS", {"start": v(2.87, -149.91) * mm, "end": v(-0.4, -149.05) * mm});
            skLineSegment(sketch, "E639.MirrorCS", {"start": v(-63.91, -286.18) * mm, "end": v(-60.32, -288.13) * mm});
            skLineSegment(sketch, "E640.MirrorCS", {"start": v(-84.2, -176.71) * mm, "end": v(-87.21, -180.3) * mm});
            skLineSegment(sketch, "E641.MirrorCS", {"start": v(-100.13, -237.62) * mm, "end": v(-99.15, -241.56) * mm});
            skLineSegment(sketch, "E642.MirrorCS", {"start": v(-74.3, -280.25) * mm, "end": v(-73.07, -281.23) * mm});
            skLineSegment(sketch, "E643.MirrorCS", {"start": v(-44.98, -295.98) * mm, "end": v(-42.74, -296.63) * mm});
            skLineSegment(sketch, "E644.MirrorCS", {"start": v(-75.6, -279.15) * mm, "end": v(-74.3, -280.25) * mm});
            skLineSegment(sketch, "E645.MirrorCS", {"start": v(-81.24, -173.58) * mm, "end": v(-84.2, -176.71) * mm});
            skLineSegment(sketch, "E646.MirrorCS", {"start": v(-67.29, -284.01) * mm, "end": v(-63.91, -286.18) * mm});
            skLineSegment(sketch, "E647.MirrorCS", {"start": v(-3.48, -149.63) * mm, "end": v(-7.1, -148.96) * mm});
            skLineSegment(sketch, "E648.MirrorCS", {"start": v(30.75, -166.2) * mm, "end": v(29.44, -165.1) * mm});
            skLineSegment(sketch, "E649.MirrorCS", {"start": v(6.3, -151.06) * mm, "end": v(2.87, -149.91) * mm});
            skLineSegment(sketch, "E650.MirrorCS", {"start": v(-76.88, -278) * mm, "end": v(-75.6, -279.15) * mm});
            skLineSegment(sketch, "E651.MirrorCS", {"start": v(-79.7, -172.37) * mm, "end": v(-81.24, -173.58) * mm});
            skLineSegment(sketch, "E652.MirrorCS", {"start": v(-71.84, -280.73) * mm, "end": v(-67.29, -284.01) * mm});
            skLineSegment(sketch, "E653.MirrorCS", {"start": v(-0.32, -150.31) * mm, "end": v(-3.48, -149.63) * mm});
            skLineSegment(sketch, "E654.MirrorCS", {"start": v(10.02, -152.53) * mm, "end": v(6.3, -151.06) * mm});
            skLineSegment(sketch, "E655.MirrorCS", {"start": v(-53.35, -292.76) * mm, "end": v(-50.69, -293.88) * mm});
            skLineSegment(sketch, "E656.MirrorCS", {"start": v(-74.44, -167.58) * mm, "end": v(-79.7, -172.37) * mm});
            skLineSegment(sketch, "E657.MirrorCS", {"start": v(-101.86, -224.26) * mm, "end": v(-101.5, -228.64) * mm});
            skLineSegment(sketch, "E658.MirrorCS", {"start": v(-75, -278.18) * mm, "end": v(-71.84, -280.73) * mm});
            skLineSegment(sketch, "E659.MirrorCS", {"start": v(2.44, -151.12) * mm, "end": v(-0.32, -150.31) * mm});
            skLineSegment(sketch, "E660.MirrorCS", {"start": v(13.37, -154.04) * mm, "end": v(10.02, -152.53) * mm});
            skLineSegment(sketch, "E661.MirrorCS", {"start": v(-55.5, -291.79) * mm, "end": v(-53.35, -292.76) * mm});
            skLineSegment(sketch, "E662.MirrorCS", {"start": v(-79.41, -275.68) * mm, "end": v(-77.95, -277.07) * mm});
            skLineSegment(sketch, "E663.MirrorCS", {"start": v(-68.8, -163.92) * mm, "end": v(-74.44, -167.58) * mm});
            skLineSegment(sketch, "E664.MirrorCS", {"start": v(-77.08, -276.26) * mm, "end": v(-75, -278.18) * mm});
            skLineSegment(sketch, "E665.MirrorCS", {"start": v(8.65, -153.34) * mm, "end": v(2.44, -151.12) * mm});
            skLineSegment(sketch, "E666.MirrorCS", {"start": v(-90.58, -182.77) * mm, "end": v(-92.63, -185.8) * mm});
            skLineSegment(sketch, "E667.MirrorCS", {"start": v(15.17, -154.96) * mm, "end": v(13.37, -154.04) * mm});
            skLineSegment(sketch, "E668.MirrorCS", {"start": v(-79.55, -273.86) * mm, "end": v(-77.08, -276.26) * mm});
            skLineSegment(sketch, "E669.MirrorCS", {"start": v(-57.04, -291.08) * mm, "end": v(-55.5, -291.79) * mm});
            skLineSegment(sketch, "E670.MirrorCS", {"start": v(-80.85, -274.27) * mm, "end": v(-79.41, -275.68) * mm});
            skLineSegment(sketch, "E671.MirrorCS", {"start": v(13.76, -155.66) * mm, "end": v(8.65, -153.34) * mm});
            skLineSegment(sketch, "E672.MirrorCS", {"start": v(-36.86, -148.5) * mm, "end": v(-42.2, -149.58) * mm});
            skLineSegment(sketch, "E673.MirrorCS", {"start": v(-89.09, -180.82) * mm, "end": v(-90.58, -182.77) * mm});
            skLineSegment(sketch, "E674.MirrorCS", {"start": v(16.9, -155.9) * mm, "end": v(15.17, -154.96) * mm});
            skLineSegment(sketch, "E675.MirrorCS", {"start": v(-82.62, -270.65) * mm, "end": v(-79.55, -273.86) * mm});
            skLineSegment(sketch, "E676.MirrorCS", {"start": v(-101.21, -212.08) * mm, "end": v(-101.68, -216.1) * mm});
            skLineSegment(sketch, "E677.MirrorCS", {"start": v(17.4, -157.68) * mm, "end": v(13.76, -155.66) * mm});
            skLineSegment(sketch, "E678.MirrorCS", {"start": v(-59.05, -290.14) * mm, "end": v(-57.04, -291.08) * mm});
            skLineSegment(sketch, "E679.MirrorCS", {"start": v(-82.1, -272.96) * mm, "end": v(-80.85, -274.27) * mm});
            skLineSegment(sketch, "E680.MirrorCS", {"start": v(-31.83, -147.61) * mm, "end": v(-36.86, -148.5) * mm});
            skLineSegment(sketch, "E681.MirrorCS", {"start": v(-88.35, -179.81) * mm, "end": v(-89.09, -180.82) * mm});
            skLineSegment(sketch, "E682.MirrorCS", {"start": v(-100.56, -208.4) * mm, "end": v(-101.21, -212.08) * mm});
            skLineSegment(sketch, "E683.MirrorCS", {"start": v(-60.43, -289.43) * mm, "end": v(-59.05, -290.14) * mm});
            skLineSegment(sketch, "E684.MirrorCS", {"start": v(-84.1, -270.81) * mm, "end": v(-82.1, -272.96) * mm});
            skLineSegment(sketch, "E685.MirrorCS", {"start": v(-86.49, -177.56) * mm, "end": v(-88.35, -179.81) * mm});
            skLineSegment(sketch, "E686.MirrorCS", {"start": v(-99.6, -204.47) * mm, "end": v(-100.56, -208.4) * mm});
            skLineSegment(sketch, "E687.MirrorCS", {"start": v(-87.39, -265) * mm, "end": v(-85.18, -267.8) * mm});
            skLineSegment(sketch, "E688.MirrorCS", {"start": v(-102.22, -210.68) * mm, "end": v(-102.6, -213.24) * mm});
            skLineSegment(sketch, "E689.MirrorCS", {"start": v(-84.63, -175.34) * mm, "end": v(-86.49, -177.56) * mm});
            skLineSegment(sketch, "E690.MirrorCS", {"start": v(-63.55, -287.72) * mm, "end": v(-61.85, -288.66) * mm});
            skLineSegment(sketch, "E691.MirrorCS", {"start": v(-36.83, -149.7) * mm, "end": v(-44.37, -152.32) * mm});
            skLineSegment(sketch, "E692.MirrorCS", {"start": v(-98.82, -201.31) * mm, "end": v(-99.6, -204.47) * mm});
            skLineSegment(sketch, "E693.MirrorCS", {"start": v(-89.65, -261.9) * mm, "end": v(-87.39, -265) * mm});
            skLineSegment(sketch, "E694.MirrorCS", {"start": v(83.77, -208.67) * mm, "end": v(75.89, -205.34) * mm});
            skLineSegment(sketch, "E695.MirrorCS", {"start": v(-101.9, -208.7) * mm, "end": v(-102.22, -210.68) * mm});
            skLineSegment(sketch, "E696.MirrorCS", {"start": v(-82.94, -173.64) * mm, "end": v(-84.63, -175.34) * mm});
            skLineSegment(sketch, "E697.MirrorCS", {"start": v(-31.44, -148.74) * mm, "end": v(-36.83, -149.7) * mm});
            skLineSegment(sketch, "E698.MirrorCS", {"start": v(-91.8, -258.63) * mm, "end": v(-89.65, -261.9) * mm});
            skLineSegment(sketch, "E699.MirrorCS", {"start": v(-38.6, -296.6) * mm, "end": v(-33.82, -297.5) * mm});
            skLineSegment(sketch, "E700.MirrorCS", {"start": v(-13.56, -147) * mm, "end": v(-20.4, -146.66) * mm});
            skLineSegment(sketch, "E701.MirrorCS", {"start": v(-46.58, -294.12) * mm, "end": v(-42.53, -295.49) * mm});
            skLineSegment(sketch, "E702.MirrorCS", {"start": v(-9.98, -147.35) * mm, "end": v(-13.56, -147) * mm});
            skLineSegment(sketch, "E703.MirrorCS", {"start": v(-50.85, -292.56) * mm, "end": v(-46.58, -294.12) * mm});
            skLineSegment(sketch, "E704.MirrorCS", {"start": v(-18.62, -147.9) * mm, "end": v(-24.47, -147.9) * mm});
            skLineSegment(sketch, "E705.MirrorCS", {"start": v(-15.37, -148.16) * mm, "end": v(-18.62, -147.9) * mm});
            skLineSegment(sketch, "E706.MirrorCS", {"start": v(-57, -289.78) * mm, "end": v(-50.85, -292.56) * mm});
            skLineSegment(sketch, "E707.MirrorCS", {"start": v(-11.83, -148.29) * mm, "end": v(-15.37, -148.16) * mm});
            skLineSegment(sketch, "E708.MirrorCS", {"start": v(-7.1, -148.96) * mm, "end": v(-11.83, -148.29) * mm});
            skLineSegment(sketch, "E709.MirrorCS", {"start": v(-48.07, -294.88) * mm, "end": v(-44.98, -295.98) * mm});
            skLineSegment(sketch, "E710.MirrorCS", {"start": v(-50.69, -293.88) * mm, "end": v(-48.07, -294.88) * mm});
            skLineSegment(sketch, "E711.MirrorCS", {"start": v(-45.46, -150.38) * mm, "end": v(-47.39, -150.72) * mm});
            skLineSegment(sketch, "E712.MirrorCS", {"start": v(-92.63, -185.8) * mm, "end": v(-93.9, -187.77) * mm});
            skLineSegment(sketch, "E713.MirrorCS", {"start": v(-42.2, -149.58) * mm, "end": v(-45.46, -150.38) * mm});
            skLineSegment(sketch, "E714.MirrorCS", {"start": v(-44.37, -152.32) * mm, "end": v(-49.12, -154.09) * mm});
            skLineSegment(sketch, "E715.MirrorCS", {"start": v(-88.1, -266.1) * mm, "end": v(-85.98, -268.73) * mm});
            skLineSegment(sketch, "E716.MirrorCS", {"start": v(-94.7, -191.88) * mm, "end": v(-96.52, -195.38) * mm});
            skLineSegment(sketch, "E717.MirrorCS", {"start": v(-93.05, -188.86) * mm, "end": v(-94.7, -191.88) * mm});
            skLineSegment(sketch, "E718.MirrorCS", {"start": v(-89.88, -184.22) * mm, "end": v(-93.05, -188.86) * mm});
            skLineSegment(sketch, "E719.MirrorCS", {"start": v(-96.48, -192.43) * mm, "end": v(-97.95, -195.5) * mm});
            skLineSegment(sketch, "E720.MirrorCS", {"start": v(-95.14, -189.98) * mm, "end": v(-96.48, -192.43) * mm});
            skLineSegment(sketch, "E721.MirrorCS", {"start": v(-93.9, -187.77) * mm, "end": v(-95.14, -189.98) * mm});
            skLineSegment(sketch, "E722.MirrorCS", {"start": v(-52.36, -155.4) * mm, "end": v(-63.2, -160.42) * mm});
            skLineSegment(sketch, "E723.MirrorCS", {"start": v(-85.18, -267.8) * mm, "end": v(-82.62, -270.65) * mm});
            skLineSegment(sketch, "E724.MirrorCS", {"start": v(83.85, -257.57) * mm, "end": v(79.8, -274.4) * mm});
            skLineSegment(sketch, "E725.MirrorCS", {"start": v(86.84, -276.69) * mm, "end": v(86.72, -257.6) * mm});
            skLineSegment(sketch, "E726.MirrorCS", {"start": v(88.92, -256.82) * mm, "end": v(93.14, -276.24) * mm});
            skLineSegment(sketch, "E727.MirrorCS", {"start": v(90.32, -255.86) * mm, "end": v(98.18, -273.35) * mm});
            skPoint(sketch, "E728.MirrorP", {"position": v(94.49, -238.26) * mm});
            skLineSegment(sketch, "E729.MirrorCS", {"start": v(90.55, -255.66) * mm, "end": v(106.7, -266.28) * mm});
            skLineSegment(sketch, "E730.MirrorCS", {"start": v(65.18, -267.67) * mm, "end": v(76.35, -249.7) * mm});
            skPoint(sketch, "E731.MirrorP", {"position": v(98.56, -274.43) * mm});
            skLineSegment(sketch, "E732", {"start": v(-82.49, -223.04) * mm, "end": v(-82.49, -221.4) * mm});
            skLineSegment(sketch, "E733", {"start": v(-82.49, -221.4) * mm, "end": v(-82.49, -219.05) * mm});
            skLineSegment(sketch, "E734", {"start": v(-82.49, -219.05) * mm, "end": v(-82.02, -216.06) * mm});
            skLineSegment(sketch, "E735", {"start": v(-82.02, -216.06) * mm, "end": v(-81.43, -212.07) * mm});
            skLineSegment(sketch, "E736", {"start": v(-81.43, -212.07) * mm, "end": v(-80.43, -208.08) * mm});
            skLineSegment(sketch, "E737", {"start": v(-80.43, -208.08) * mm, "end": v(-78.82, -203.66) * mm});
            skLineSegment(sketch, "E738", {"start": v(-78.82, -203.66) * mm, "end": v(-76.26, -197.83) * mm});
            skLineSegment(sketch, "E739", {"start": v(-76.26, -197.83) * mm, "end": v(-72.8, -192.6) * mm});
            skLineSegment(sketch, "E740", {"start": v(-72.8, -192.6) * mm, "end": v(-69.25, -187.67) * mm});
            skLineSegment(sketch, "E741", {"start": v(-69.25, -187.67) * mm, "end": v(-65.7, -183.92) * mm});
            skLineSegment(sketch, "E742", {"start": v(-65.7, -183.92) * mm, "end": v(-61.26, -180.17) * mm});
            skLineSegment(sketch, "E743", {"start": v(-61.26, -180.17) * mm, "end": v(-56.92, -177.41) * mm});
            skLineSegment(sketch, "E744", {"start": v(-56.92, -177.41) * mm, "end": v(-52.28, -174.75) * mm});
            skLineSegment(sketch, "E745", {"start": v(-52.28, -174.75) * mm, "end": v(-47.35, -172.28) * mm});
            skLineSegment(sketch, "E746", {"start": v(-47.35, -172.28) * mm, "end": v(-42.22, -170.01) * mm});
            skLineSegment(sketch, "E747", {"start": v(-42.22, -170.01) * mm, "end": v(-37.68, -168.43) * mm});
            skLineSegment(sketch, "E748", {"start": v(-37.68, -168.43) * mm, "end": v(-33.24, -167.25) * mm});
            skLineSegment(sketch, "E749", {"start": v(-33.24, -167.25) * mm, "end": v(-29.1, -166.36) * mm});
            skLineSegment(sketch, "E750", {"start": v(-29.1, -166.36) * mm, "end": v(-24.96, -165.78) * mm});
            skLineSegment(sketch, "E751", {"start": v(-24.96, -165.78) * mm, "end": v(-20.31, -165.33) * mm});
            skLineSegment(sketch, "E752", {"start": v(-20.31, -165.33) * mm, "end": v(-13.4, -165.33) * mm});
            skLineSegment(sketch, "E753", {"start": v(-13.4, -165.33) * mm, "end": v(-7.28, -165.55) * mm});
            skLineSegment(sketch, "E754", {"start": v(-7.28, -165.55) * mm, "end": v(-3.07, -165.86) * mm});
            skLineSegment(sketch, "E755", {"start": v(-3.07, -165.86) * mm, "end": v(0.75, -166.36) * mm});
            skLineSegment(sketch, "E756", {"start": v(0.75, -166.36) * mm, "end": v(3.61, -167.02) * mm});
            skLineSegment(sketch, "E757", {"start": v(3.61, -167.02) * mm, "end": v(6.56, -167.81) * mm});
            skLineSegment(sketch, "E758", {"start": v(6.56, -167.81) * mm, "end": v(9.81, -168.83) * mm});
            skLineSegment(sketch, "E759", {"start": v(9.81, -168.83) * mm, "end": v(13.38, -170.11) * mm});
            skLineSegment(sketch, "E760", {"start": v(13.38, -170.11) * mm, "end": v(15.8, -171.4) * mm});
            skLineSegment(sketch, "E761", {"start": v(15.8, -171.4) * mm, "end": v(18.59, -172.8) * mm});
            skLineSegment(sketch, "E762", {"start": v(18.59, -172.8) * mm, "end": v(21.5, -174.5) * mm});
            skLineSegment(sketch, "E763", {"start": v(21.5, -174.5) * mm, "end": v(25.68, -177.48) * mm});
            skLineSegment(sketch, "E764", {"start": v(25.68, -177.48) * mm, "end": v(29.17, -180.38) * mm});
            skLineSegment(sketch, "E765", {"start": v(29.17, -180.38) * mm, "end": v(32.57, -183.16) * mm});
            skLineSegment(sketch, "E766", {"start": v(32.57, -183.16) * mm, "end": v(35.64, -185.73) * mm});
            skLineSegment(sketch, "E767", {"start": v(35.64, -185.73) * mm, "end": v(37.42, -187.3) * mm});
            skLineSegment(sketch, "E768", {"start": v(37.42, -187.3) * mm, "end": v(39.16, -188.92) * mm});
            skLineSegment(sketch, "E769", {"start": v(39.16, -188.92) * mm, "end": v(41.78, -191.1) * mm});
            skLineSegment(sketch, "E770", {"start": v(41.78, -191.1) * mm, "end": v(45.01, -193.57) * mm});
            skLineSegment(sketch, "E771", {"start": v(45.01, -193.57) * mm, "end": v(47.81, -195.69) * mm});
            skLineSegment(sketch, "E772", {"start": v(47.81, -195.69) * mm, "end": v(51.17, -197.93) * mm});
            skLineSegment(sketch, "E773", {"start": v(51.17, -197.93) * mm, "end": v(53.68, -199.57) * mm});
            skLineSegment(sketch, "E774", {"start": v(53.68, -199.57) * mm, "end": v(56.3, -201.2) * mm});
            skLineSegment(sketch, "E775", {"start": v(56.3, -201.2) * mm, "end": v(58.35, -202.64) * mm});
            skLineSegment(sketch, "E776", {"start": v(58.35, -202.64) * mm, "end": v(61.13, -204.46) * mm});
            skLineSegment(sketch, "E777", {"start": v(61.13, -204.46) * mm, "end": v(62.38, -205.1) * mm});
            skLineSegment(sketch, "E778", {"start": v(62.38, -205.1) * mm, "end": v(63.9, -205.86) * mm});
            skLineSegment(sketch, "E779", {"start": v(63.9, -205.86) * mm, "end": v(65.64, -206.56) * mm});
            skLineSegment(sketch, "E780", {"start": v(65.64, -206.56) * mm, "end": v(67.25, -207.09) * mm});
            skLineSegment(sketch, "E781", {"start": v(67.25, -207.09) * mm, "end": v(68.79, -207.4) * mm});
            skLineSegment(sketch, "E782", {"start": v(68.79, -207.4) * mm, "end": v(70.05, -207.57) * mm});
            skLineSegment(sketch, "E783", {"start": v(70.05, -207.57) * mm, "end": v(70.9, -207.62) * mm});
            skLineSegment(sketch, "E784", {"start": v(70.9, -207.62) * mm, "end": v(72.92, -207.62) * mm});
            skLineSegment(sketch, "E785", {"start": v(72.92, -207.62) * mm, "end": v(75.18, -207.3) * mm});
            skLineSegment(sketch, "E786", {"start": v(75.18, -207.3) * mm, "end": v(76.57, -207) * mm});
            skLineSegment(sketch, "E787", {"start": v(76.57, -207) * mm, "end": v(78.1, -206.27) * mm});
            skLineSegment(sketch, "E788", {"start": v(-82.49, -223.04) * mm, "end": v(-82.36, -226.24) * mm});
            skLineSegment(sketch, "E789", {"start": v(-82.36, -226.24) * mm, "end": v(-82.05, -229.04) * mm});
            skLineSegment(sketch, "E790", {"start": v(-82.05, -229.04) * mm, "end": v(-81.62, -231.92) * mm});
            skLineSegment(sketch, "E791", {"start": v(-81.62, -231.92) * mm, "end": v(-80.4, -237.06) * mm});
            skLineSegment(sketch, "E792", {"start": v(-80.4, -237.06) * mm, "end": v(-79.11, -240.99) * mm});
            skLineSegment(sketch, "E793", {"start": v(-79.11, -240.99) * mm, "end": v(-77.57, -244.7) * mm});
            skLineSegment(sketch, "E794", {"start": v(-77.57, -244.7) * mm, "end": v(-75.22, -249.17) * mm});
            skLineSegment(sketch, "E795", {"start": v(-75.22, -249.17) * mm, "end": v(-72.17, -253.89) * mm});
            skLineSegment(sketch, "E796", {"start": v(-72.17, -253.89) * mm, "end": v(-70.06, -256.62) * mm});
            skLineSegment(sketch, "E797", {"start": v(-70.06, -256.62) * mm, "end": v(-67.85, -259.13) * mm});
            skLineSegment(sketch, "E798", {"start": v(-67.85, -259.13) * mm, "end": v(-65.53, -261.68) * mm});
            skLineSegment(sketch, "E799", {"start": v(-65.53, -261.68) * mm, "end": v(-62.29, -264.48) * mm});
            skLineSegment(sketch, "E800", {"start": v(-62.29, -264.48) * mm, "end": v(-58.84, -267.03) * mm});
            skLineSegment(sketch, "E801", {"start": v(-58.84, -267.03) * mm, "end": v(-55.6, -269.01) * mm});
            skLineSegment(sketch, "E802", {"start": v(-55.6, -269.01) * mm, "end": v(-51.88, -271.02) * mm});
            skLineSegment(sketch, "E803", {"start": v(-51.88, -271.02) * mm, "end": v(-48.23, -272.84) * mm});
            skLineSegment(sketch, "E804", {"start": v(-48.23, -272.84) * mm, "end": v(-44.91, -274.38) * mm});
            skLineSegment(sketch, "E805", {"start": v(-44.91, -274.38) * mm, "end": v(-41.88, -275.71) * mm});
            skLineSegment(sketch, "E806", {"start": v(-41.88, -275.71) * mm, "end": v(-38.9, -276.79) * mm});
            skLineSegment(sketch, "E807", {"start": v(-38.9, -276.79) * mm, "end": v(-35.92, -277.74) * mm});
            skLineSegment(sketch, "E808", {"start": v(-35.92, -277.74) * mm, "end": v(-32.72, -278.5) * mm});
            skLineSegment(sketch, "E809", {"start": v(-32.72, -278.5) * mm, "end": v(-28.83, -279.26) * mm});
            skLineSegment(sketch, "E810", {"start": v(-28.83, -279.26) * mm, "end": v(-25.23, -279.8) * mm});
            skLineSegment(sketch, "E811", {"start": v(-25.23, -279.8) * mm, "end": v(-21.89, -280.23) * mm});
            skLineSegment(sketch, "E812", {"start": v(-21.89, -280.23) * mm, "end": v(-19.1, -280.4) * mm});
            skLineSegment(sketch, "E813", {"start": v(-19.1, -280.4) * mm, "end": v(-13.53, -280.4) * mm});
            skLineSegment(sketch, "E814", {"start": v(-13.53, -280.4) * mm, "end": v(-9.3, -280.2) * mm});
            skLineSegment(sketch, "E815", {"start": v(-9.3, -280.2) * mm, "end": v(-4.3, -279.93) * mm});
            skLineSegment(sketch, "E816", {"start": v(-4.3, -279.93) * mm, "end": v(-0.6, -279.6) * mm});
            skLineSegment(sketch, "E817", {"start": v(-0.6, -279.6) * mm, "end": v(1.94, -279.2) * mm});
            skLineSegment(sketch, "E818", {"start": v(1.94, -279.2) * mm, "end": v(5.8, -278.25) * mm});
            skLineSegment(sketch, "E819", {"start": v(5.8, -278.25) * mm, "end": v(9.37, -277.2) * mm});
            skLineSegment(sketch, "E820", {"start": v(9.37, -277.2) * mm, "end": v(12.8, -275.88) * mm});
            skLineSegment(sketch, "E821", {"start": v(12.8, -275.88) * mm, "end": v(16.46, -274.07) * mm});
            skLineSegment(sketch, "E822", {"start": v(16.46, -274.07) * mm, "end": v(18.93, -272.78) * mm});
            skLineSegment(sketch, "E823", {"start": v(18.93, -272.78) * mm, "end": v(22.84, -270.25) * mm});
            skLineSegment(sketch, "E824", {"start": v(22.84, -270.25) * mm, "end": v(25.45, -268.28) * mm});
            skLineSegment(sketch, "E825", {"start": v(25.45, -268.28) * mm, "end": v(28.1, -266.08) * mm});
            skLineSegment(sketch, "E826", {"start": v(28.1, -266.08) * mm, "end": v(30.88, -263.77) * mm});
            skLineSegment(sketch, "E827", {"start": v(30.88, -263.77) * mm, "end": v(32.57, -262.36) * mm});
            skLineSegment(sketch, "E828", {"start": v(32.57, -262.36) * mm, "end": v(35.03, -260.59) * mm});
            skLineSegment(sketch, "E829", {"start": v(35.03, -260.59) * mm, "end": v(36.34, -259.73) * mm});
            skLineSegment(sketch, "E830", {"start": v(36.34, -259.73) * mm, "end": v(37.39, -259.07) * mm});
            skLineSegment(sketch, "E831", {"start": v(37.39, -259.07) * mm, "end": v(39.18, -258.17) * mm});
            skLineSegment(sketch, "E832", {"start": v(39.18, -258.17) * mm, "end": v(40.92, -257.56) * mm});
            skLineSegment(sketch, "E833", {"start": v(40.92, -257.56) * mm, "end": v(42.63, -257.16) * mm});
            skLineSegment(sketch, "E834", {"start": v(42.63, -257.16) * mm, "end": v(44.72, -256.83) * mm});
            skLineSegment(sketch, "E835", {"start": v(44.72, -256.83) * mm, "end": v(46.95, -256.65) * mm});
            skLineSegment(sketch, "E836", {"start": v(46.95, -256.65) * mm, "end": v(48.54, -256.65) * mm});
            skLineSegment(sketch, "E837", {"start": v(48.54, -256.65) * mm, "end": v(50.14, -256.82) * mm});
            skLineSegment(sketch, "E838", {"start": v(50.14, -256.82) * mm, "end": v(52.15, -257.36) * mm});
            skLineSegment(sketch, "E839", {"start": v(52.15, -257.36) * mm, "end": v(53.62, -257.84) * mm});
            skLineSegment(sketch, "E840", {"start": v(53.62, -257.84) * mm, "end": v(55.7, -258.8) * mm});
            skLineSegment(sketch, "E841", {"start": v(55.7, -258.8) * mm, "end": v(57.35, -259.73) * mm});
            skLineSegment(sketch, "E842", {"start": v(57.35, -259.73) * mm, "end": v(58.75, -261.02) * mm});
            skLineSegment(sketch, "E843", {"start": v(58.75, -261.02) * mm, "end": v(60.06, -262.59) * mm});
            skLineSegment(sketch, "E844", {"start": v(60.06, -262.59) * mm, "end": v(61.05, -263.79) * mm});
            skLineSegment(sketch, "E845", {"start": v(61.05, -263.79) * mm, "end": v(62.26, -265.48) * mm});
            skLineSegment(sketch, "E846", {"start": v(62.26, -265.48) * mm, "end": v(63.04, -266.68) * mm});
            skLineSegment(sketch, "E847", {"start": v(-79.04, -222.95) * mm, "end": v(-79.04, -220.6) * mm});
            skLineSegment(sketch, "E848", {"start": v(-79.04, -220.6) * mm, "end": v(-78.67, -216.93) * mm});
            skLineSegment(sketch, "E849", {"start": v(-78.67, -216.93) * mm, "end": v(-77.85, -212.47) * mm});
            skLineSegment(sketch, "E850", {"start": v(-77.85, -212.47) * mm, "end": v(-76.66, -208.14) * mm});
            skLineSegment(sketch, "E851", {"start": v(-76.66, -208.14) * mm, "end": v(-75.12, -204.33) * mm});
            skLineSegment(sketch, "E852", {"start": v(-75.12, -204.33) * mm, "end": v(-73.56, -201.1) * mm});
            skLineSegment(sketch, "E853", {"start": v(-73.56, -201.1) * mm, "end": v(-71.28, -197.14) * mm});
            skLineSegment(sketch, "E854", {"start": v(-71.28, -197.14) * mm, "end": v(-68.86, -193.67) * mm});
            skLineSegment(sketch, "E855", {"start": v(-68.86, -193.67) * mm, "end": v(-65.93, -190.03) * mm});
            skLineSegment(sketch, "E856", {"start": v(-65.93, -190.03) * mm, "end": v(-62.18, -186.48) * mm});
            skLineSegment(sketch, "E857", {"start": v(-62.18, -186.48) * mm, "end": v(-59.25, -184.13) * mm});
            skLineSegment(sketch, "E858", {"start": v(-59.25, -184.13) * mm, "end": v(-55.95, -181.99) * mm});
            skLineSegment(sketch, "E859", {"start": v(-55.95, -181.99) * mm, "end": v(-43.08, -174.7) * mm});
            skLineSegment(sketch, "E860", {"start": v(-43.08, -174.7) * mm, "end": v(-39.88, -173.17) * mm});
            skLineSegment(sketch, "E861", {"start": v(-39.88, -173.17) * mm, "end": v(-37.83, -172.28) * mm});
            skLineSegment(sketch, "E862", {"start": v(-37.83, -172.28) * mm, "end": v(-32.93, -170.68) * mm});
            skLineSegment(sketch, "E863", {"start": v(-32.93, -170.68) * mm, "end": v(-27.38, -169.39) * mm});
            skLineSegment(sketch, "E864", {"start": v(-27.38, -169.39) * mm, "end": v(-22.71, -168.74) * mm});
            skLineSegment(sketch, "E865", {"start": v(-22.71, -168.74) * mm, "end": v(-17.64, -168.47) * mm});
            skLineSegment(sketch, "E866", {"start": v(-17.64, -168.47) * mm, "end": v(-6.44, -168.84) * mm});
            skLineSegment(sketch, "E867", {"start": v(-6.44, -168.84) * mm, "end": v(-2.3, -169.22) * mm});
            skLineSegment(sketch, "E868", {"start": v(-2.3, -169.22) * mm, "end": v(0.41, -169.6) * mm});
            skLineSegment(sketch, "E869", {"start": v(0.41, -169.6) * mm, "end": v(3.4, -170.27) * mm});
            skLineSegment(sketch, "E870", {"start": v(3.4, -170.27) * mm, "end": v(7.16, -171.3) * mm});
            skLineSegment(sketch, "E871", {"start": v(7.16, -171.3) * mm, "end": v(9.97, -172.25) * mm});
            skLineSegment(sketch, "E872", {"start": v(9.97, -172.25) * mm, "end": v(13.97, -173.85) * mm});
            skLineSegment(sketch, "E873", {"start": v(13.97, -173.85) * mm, "end": v(18.4, -176.28) * mm});
            skLineSegment(sketch, "E874", {"start": v(18.4, -176.28) * mm, "end": v(22.92, -179.1) * mm});
            skLineSegment(sketch, "E875", {"start": v(22.92, -179.1) * mm, "end": v(26.13, -181.58) * mm});
            skLineSegment(sketch, "E876", {"start": v(26.13, -181.58) * mm, "end": v(29.22, -184.08) * mm});
            skLineSegment(sketch, "E877", {"start": v(29.22, -184.08) * mm, "end": v(35.95, -189.62) * mm});
            skLineSegment(sketch, "E878", {"start": v(35.95, -189.62) * mm, "end": v(39.46, -192.51) * mm});
            skLineSegment(sketch, "E879", {"start": v(39.46, -192.51) * mm, "end": v(42.78, -195.18) * mm});
            skLineSegment(sketch, "E880", {"start": v(42.78, -195.18) * mm, "end": v(46.17, -197.79) * mm});
            skLineSegment(sketch, "E881", {"start": v(46.17, -197.79) * mm, "end": v(48.87, -199.92) * mm});
            skLineSegment(sketch, "E882", {"start": v(48.87, -199.92) * mm, "end": v(51.65, -201.9) * mm});
            skLineSegment(sketch, "E883", {"start": v(51.65, -201.9) * mm, "end": v(54.4, -203.77) * mm});
            skLineSegment(sketch, "E884", {"start": v(54.4, -203.77) * mm, "end": v(57.6, -205.69) * mm});
            skLineSegment(sketch, "E885", {"start": v(57.6, -205.69) * mm, "end": v(61.97, -208.07) * mm});
            skLineSegment(sketch, "E886", {"start": v(61.97, -208.07) * mm, "end": v(67.04, -210.56) * mm});
            skLineSegment(sketch, "E887", {"start": v(67.04, -210.56) * mm, "end": v(70.28, -211.96) * mm});
            skLineSegment(sketch, "E888", {"start": v(70.28, -211.96) * mm, "end": v(73.56, -213.27) * mm});
            skLineSegment(sketch, "E889", {"start": v(73.56, -213.27) * mm, "end": v(75.95, -214.1) * mm});
            skLineSegment(sketch, "E890", {"start": v(75.95, -214.1) * mm, "end": v(78.88, -215.1) * mm});
            skLineSegment(sketch, "E891", {"start": v(78.88, -215.1) * mm, "end": v(82.18, -216.23) * mm});
            skLineSegment(sketch, "E892", {"start": v(82.18, -216.23) * mm, "end": v(85.75, -217.39) * mm});
            skLineSegment(sketch, "E893", {"start": v(85.75, -217.39) * mm, "end": v(87.78, -218.12) * mm});
            skLineSegment(sketch, "E894", {"start": v(87.78, -218.12) * mm, "end": v(90.01, -219.1) * mm});
            skLineSegment(sketch, "E895", {"start": v(90.01, -219.1) * mm, "end": v(91.7, -219.96) * mm});
            skLineSegment(sketch, "E896", {"start": v(91.7, -219.96) * mm, "end": v(92.68, -220.78) * mm});
            skLineSegment(sketch, "E897", {"start": v(92.68, -220.78) * mm, "end": v(93.42, -221.5) * mm});
            skLineSegment(sketch, "E898", {"start": v(93.42, -221.5) * mm, "end": v(93.7, -222.25) * mm});
            skLineSegment(sketch, "E899", {"start": v(93.7, -222.25) * mm, "end": v(93.7, -223.5) * mm});
            skLineSegment(sketch, "E900", {"start": v(93.7, -223.5) * mm, "end": v(93.5, -224.1) * mm});
            skLineSegment(sketch, "E901", {"start": v(93.5, -224.1) * mm, "end": v(93.2, -224.59) * mm});
            skLineSegment(sketch, "E902", {"start": v(93.2, -224.59) * mm, "end": v(92.3, -225.42) * mm});
            skLineSegment(sketch, "E903", {"start": v(92.3, -225.42) * mm, "end": v(91.45, -226) * mm});
            skLineSegment(sketch, "E904", {"start": v(91.45, -226) * mm, "end": v(89.39, -227.05) * mm});
            skLineSegment(sketch, "E905", {"start": v(89.39, -227.05) * mm, "end": v(80.72, -230) * mm});
            skLineSegment(sketch, "E906", {"start": v(80.72, -230) * mm, "end": v(76.74, -231.2) * mm});
            skLineSegment(sketch, "E907", {"start": v(76.74, -231.2) * mm, "end": v(72.64, -232.66) * mm});
            skLineSegment(sketch, "E908", {"start": v(72.64, -232.66) * mm, "end": v(69.75, -233.77) * mm});
            skLineSegment(sketch, "E909", {"start": v(69.75, -233.77) * mm, "end": v(65.7, -235.63) * mm});
            skLineSegment(sketch, "E910", {"start": v(65.7, -235.63) * mm, "end": v(61.82, -237.73) * mm});
            skLineSegment(sketch, "E911", {"start": v(61.82, -237.73) * mm, "end": v(58.47, -239.92) * mm});
            skLineSegment(sketch, "E912", {"start": v(58.47, -239.92) * mm, "end": v(51.94, -244.5) * mm});
            skLineSegment(sketch, "E913", {"start": v(51.94, -244.5) * mm, "end": v(46.32, -248.44) * mm});
            skLineSegment(sketch, "E914", {"start": v(46.32, -248.44) * mm, "end": v(41.76, -251.76) * mm});
            skLineSegment(sketch, "E915", {"start": v(41.76, -251.76) * mm, "end": v(38.91, -253.87) * mm});
            skLineSegment(sketch, "E916", {"start": v(38.91, -253.87) * mm, "end": v(35.47, -256.5) * mm});
            skLineSegment(sketch, "E917", {"start": v(35.47, -256.5) * mm, "end": v(31.55, -259.5) * mm});
            skLineSegment(sketch, "E918", {"start": v(31.55, -259.5) * mm, "end": v(29.9, -260.8) * mm});
            skLineSegment(sketch, "E919", {"start": v(29.9, -260.8) * mm, "end": v(28.59, -261.9) * mm});
            skLineSegment(sketch, "E920", {"start": v(28.59, -261.9) * mm, "end": v(25.85, -264.3) * mm});
            skLineSegment(sketch, "E921", {"start": v(25.85, -264.3) * mm, "end": v(23.04, -266.57) * mm});
            skLineSegment(sketch, "E922", {"start": v(23.04, -266.57) * mm, "end": v(20.96, -267.99) * mm});
            skLineSegment(sketch, "E923", {"start": v(20.96, -267.99) * mm, "end": v(17.86, -269.78) * mm});
            skLineSegment(sketch, "E924", {"start": v(17.86, -269.78) * mm, "end": v(13.98, -271.82) * mm});
            skLineSegment(sketch, "E925", {"start": v(13.98, -271.82) * mm, "end": v(10.96, -273.07) * mm});
            skLineSegment(sketch, "E926", {"start": v(10.96, -273.07) * mm, "end": v(7.2, -274.33) * mm});
            skLineSegment(sketch, "E927", {"start": v(7.2, -274.33) * mm, "end": v(3.48, -275.34) * mm});
            skLineSegment(sketch, "E928", {"start": v(3.48, -275.34) * mm, "end": v(-0.44, -276.13) * mm});
            skLineSegment(sketch, "E929", {"start": v(-0.44, -276.13) * mm, "end": v(-3.77, -276.48) * mm});
            skLineSegment(sketch, "E930", {"start": v(-3.77, -276.48) * mm, "end": v(-9.07, -276.82) * mm});
            skLineSegment(sketch, "E931", {"start": v(-9.07, -276.82) * mm, "end": v(-13.22, -277.02) * mm});
            skLineSegment(sketch, "E932", {"start": v(-13.22, -277.02) * mm, "end": v(-18.16, -277.17) * mm});
            skLineSegment(sketch, "E933", {"start": v(-18.16, -277.17) * mm, "end": v(-21.42, -276.96) * mm});
            skLineSegment(sketch, "E934", {"start": v(-21.42, -276.96) * mm, "end": v(-27.88, -276.18) * mm});
            skLineSegment(sketch, "E935", {"start": v(-27.88, -276.18) * mm, "end": v(-33.85, -274.7) * mm});
            skLineSegment(sketch, "E936", {"start": v(-33.85, -274.7) * mm, "end": v(-37.14, -273.6) * mm});
            skLineSegment(sketch, "E937", {"start": v(-37.14, -273.6) * mm, "end": v(-40.04, -272.38) * mm});
            skLineSegment(sketch, "E938", {"start": v(-40.04, -272.38) * mm, "end": v(-42.06, -271.41) * mm});
            skLineSegment(sketch, "E939", {"start": v(-42.06, -271.41) * mm, "end": v(-44.8, -270.02) * mm});
            skLineSegment(sketch, "E940", {"start": v(-44.8, -270.02) * mm, "end": v(-48, -268.18) * mm});
            skLineSegment(sketch, "E941", {"start": v(-48, -268.18) * mm, "end": v(-51.7, -266.18) * mm});
            skLineSegment(sketch, "E942", {"start": v(-51.7, -266.18) * mm, "end": v(-56.12, -263.54) * mm});
            skLineSegment(sketch, "E943", {"start": v(-56.12, -263.54) * mm, "end": v(-58.62, -261.88) * mm});
            skLineSegment(sketch, "E944", {"start": v(-58.62, -261.88) * mm, "end": v(-62.18, -259.2) * mm});
            skLineSegment(sketch, "E945", {"start": v(-62.18, -259.2) * mm, "end": v(-65.12, -256.33) * mm});
            skLineSegment(sketch, "E946", {"start": v(-65.12, -256.33) * mm, "end": v(-67.96, -253.06) * mm});
            skLineSegment(sketch, "E947", {"start": v(-67.96, -253.06) * mm, "end": v(-69.73, -250.76) * mm});
            skLineSegment(sketch, "E948", {"start": v(-69.73, -250.76) * mm, "end": v(-71.66, -247.68) * mm});
            skLineSegment(sketch, "E949", {"start": v(-71.66, -247.68) * mm, "end": v(-73.82, -243.82) * mm});
            skLineSegment(sketch, "E950", {"start": v(-73.82, -243.82) * mm, "end": v(-75.68, -239.77) * mm});
            skLineSegment(sketch, "E951", {"start": v(-75.68, -239.77) * mm, "end": v(-77.1, -235.7) * mm});
            skLineSegment(sketch, "E952", {"start": v(-77.1, -235.7) * mm, "end": v(-77.83, -232.82) * mm});
            skLineSegment(sketch, "E953", {"start": v(-77.83, -232.82) * mm, "end": v(-78.56, -229.12) * mm});
            skLineSegment(sketch, "E954", {"start": v(-78.56, -229.12) * mm, "end": v(-78.84, -226.59) * mm});
            skLineSegment(sketch, "E955", {"start": v(-78.84, -226.59) * mm, "end": v(-79.04, -224.04) * mm});
            skLineSegment(sketch, "E956", {"start": v(-79.04, -224.04) * mm, "end": v(-79.04, -222.95) * mm});
            skLineSegment(sketch, "E957.0", {"start": v(-74.74, -220.8) * mm, "end": v(-74.39, -217.36) * mm});
            skLineSegment(sketch, "E957.1", {"start": v(-74.74, -222.95) * mm, "end": v(-74.74, -220.8) * mm});
            skLineSegment(sketch, "E957.2", {"start": v(-74.74, -223.87) * mm, "end": v(-74.74, -222.95) * mm});
            skLineSegment(sketch, "E957.3", {"start": v(-74.56, -226.18) * mm, "end": v(-74.74, -223.87) * mm});
            skLineSegment(sketch, "E957.4", {"start": v(-71.62, -238.35) * mm, "end": v(-72.98, -234.46) * mm});
            skLineSegment(sketch, "E957.5", {"start": v(-72.98, -234.46) * mm, "end": v(-73.63, -231.88) * mm});
            skLineSegment(sketch, "E957.6", {"start": v(-73.63, -231.88) * mm, "end": v(-74.3, -228.46) * mm});
            skLineSegment(sketch, "E957.7", {"start": v(-74.3, -228.46) * mm, "end": v(-74.56, -226.18) * mm});
            skLineSegment(sketch, "E958.0", {"start": v(-27.4, -273.52) * mm, "end": v(-33.2, -272.08) * mm});
            skLineSegment(sketch, "E958.1", {"start": v(-21.17, -274.27) * mm, "end": v(-27.4, -273.52) * mm});
            skLineSegment(sketch, "E958.2", {"start": v(-18.12, -274.46) * mm, "end": v(-21.17, -274.27) * mm});
            skLineSegment(sketch, "E958.3", {"start": v(-13.33, -274.32) * mm, "end": v(-18.12, -274.46) * mm});
            skLineSegment(sketch, "E958.4", {"start": v(-9.22, -274.12) * mm, "end": v(-13.33, -274.32) * mm});
            skLineSegment(sketch, "E959.0", {"start": v(-38.8, -175.53) * mm, "end": v(-36.8, -174.67) * mm});
            skLineSegment(sketch, "E959.1", {"start": v(-41.96, -177.05) * mm, "end": v(-38.8, -175.53) * mm});
            skLineSegment(sketch, "E960.1", {"start": v(-22.57, -171.44) * mm, "end": v(-17.61, -171.17) * mm});
            skLineSegment(sketch, "E961.0", {"start": v(-68.08, -199.37) * mm, "end": v(-65.66, -195.9) * mm});
            skLineSegment(sketch, "E962.0", {"start": v(-60, -189.21) * mm, "end": v(-57.06, -186.86) * mm});
            skLineSegment(sketch, "E963.0", {"start": v(56.45, -207.69) * mm, "end": v(60.87, -210.1) * mm});
            skLineSegment(sketch, "E963.1", {"start": v(53.22, -205.73) * mm, "end": v(56.45, -207.69) * mm});
            skLineSegment(sketch, "E964.0", {"start": v(44.82, -199.53) * mm, "end": v(47.51, -201.65) * mm});
            skLineSegment(sketch, "E964.1", {"start": v(41.42, -196.91) * mm, "end": v(44.82, -199.53) * mm});
            skLineSegment(sketch, "E964.2", {"start": v(38.08, -194.22) * mm, "end": v(41.42, -196.91) * mm});
            skLineSegment(sketch, "E965", {"start": v(47.51, -201.65) * mm, "end": v(53.22, -205.73) * mm});
            skLineSegment(sketch, "E966", {"start": v(60.87, -210.1) * mm, "end": v(64.62, -212.1) * mm});
            skLineSegment(sketch, "E967", {"start": v(64.62, -212.1) * mm, "end": v(67.03, -213.26) * mm});
            skLineSegment(sketch, "E968", {"start": v(67.03, -213.26) * mm, "end": v(69.32, -214.46) * mm});
            skLineSegment(sketch, "E969", {"start": v(69.32, -214.46) * mm, "end": v(71.46, -215.38) * mm});
            skLineSegment(sketch, "E970", {"start": v(71.46, -215.38) * mm, "end": v(73.9, -216.27) * mm});
            skLineSegment(sketch, "E971", {"start": v(73.9, -216.27) * mm, "end": v(79.82, -218.24) * mm});
            skLineSegment(sketch, "E972", {"start": v(79.82, -218.24) * mm, "end": v(82.73, -219.2) * mm});
            skLineSegment(sketch, "E973", {"start": v(82.73, -219.2) * mm, "end": v(84.46, -220.02) * mm});
            skLineSegment(sketch, "E974", {"start": v(84.46, -220.02) * mm, "end": v(85.52, -220.7) * mm});
            skLineSegment(sketch, "E975", {"start": v(85.52, -220.7) * mm, "end": v(86.47, -221.67) * mm});
            skLineSegment(sketch, "E976", {"start": v(86.47, -221.67) * mm, "end": v(86.74, -222.66) * mm});
            skLineSegment(sketch, "E977", {"start": v(86.74, -222.66) * mm, "end": v(86.6, -223.59) * mm});
            skLineSegment(sketch, "E978", {"start": v(86.6, -223.59) * mm, "end": v(86.15, -224.32) * mm});
            skLineSegment(sketch, "E979", {"start": v(86.15, -224.32) * mm, "end": v(84.72, -225.34) * mm});
            skLineSegment(sketch, "E980", {"start": v(84.72, -225.34) * mm, "end": v(81.57, -226.66) * mm});
            skLineSegment(sketch, "E981", {"start": v(81.57, -226.66) * mm, "end": v(75.03, -228.83) * mm});
            skLineSegment(sketch, "E982", {"start": v(75.03, -228.83) * mm, "end": v(70.16, -230.7) * mm});
            skLineSegment(sketch, "E983", {"start": v(70.16, -230.7) * mm, "end": v(66.25, -232.55) * mm});
            skLineSegment(sketch, "E984", {"start": v(66.25, -232.55) * mm, "end": v(62.03, -234.96) * mm});
            skLineSegment(sketch, "E985", {"start": v(62.03, -234.96) * mm, "end": v(56.88, -238.27) * mm});
            skLineSegment(sketch, "E986", {"start": v(56.88, -238.27) * mm, "end": v(53.37, -240.6) * mm});
            skLineSegment(sketch, "E987", {"start": v(53.37, -240.6) * mm, "end": v(48.93, -243.61) * mm});
            skLineSegment(sketch, "E988", {"start": v(48.93, -243.61) * mm, "end": v(44.2, -246.92) * mm});
            skLineSegment(sketch, "E989", {"start": v(44.2, -246.92) * mm, "end": v(39.98, -249.87) * mm});
            skLineSegment(sketch, "E990", {"start": v(39.98, -249.87) * mm, "end": v(37.29, -251.88) * mm});
            skLineSegment(sketch, "E991", {"start": v(37.29, -251.88) * mm, "end": v(32.96, -255.02) * mm});
            skLineSegment(sketch, "E992", {"start": v(32.96, -255.02) * mm, "end": v(28.96, -258) * mm});
            skLineSegment(sketch, "E993", {"start": v(28.96, -258) * mm, "end": v(25.82, -260.46) * mm});
            skLineSegment(sketch, "E994", {"start": v(25.82, -260.46) * mm, "end": v(23.02, -262.69) * mm});
            skLineSegment(sketch, "E995", {"start": v(23.02, -262.69) * mm, "end": v(19.65, -264.71) * mm});
            skLineSegment(sketch, "E996", {"start": v(19.65, -264.71) * mm, "end": v(17.3, -266) * mm});
            skLineSegment(sketch, "E997", {"start": v(17.3, -266) * mm, "end": v(13.4, -267.77) * mm});
            skLineSegment(sketch, "E998", {"start": v(13.4, -267.77) * mm, "end": v(9.72, -269.15) * mm});
            skLineSegment(sketch, "E999", {"start": v(9.72, -269.15) * mm, "end": v(5.3, -270.59) * mm});
            skLineSegment(sketch, "E1000", {"start": v(5.3, -270.59) * mm, "end": v(2.24, -271.45) * mm});
            skLineSegment(sketch, "E1001", {"start": v(2.24, -271.45) * mm, "end": v(-1.9, -272.56) * mm});
            skLineSegment(sketch, "E1002", {"start": v(-1.9, -272.56) * mm, "end": v(-4.69, -273.14) * mm});
            skLineSegment(sketch, "E1003", {"start": v(-4.69, -273.14) * mm, "end": v(-8.13, -273.8) * mm});
            skLineSegment(sketch, "E1004", {"start": v(-8.13, -273.8) * mm, "end": v(-9.22, -274.12) * mm});
            skLineSegment(sketch, "E1005", {"start": v(-33.2, -272.08) * mm, "end": v(-35.92, -271.23) * mm});
            skLineSegment(sketch, "E1006", {"start": v(-35.92, -271.23) * mm, "end": v(-38.08, -270.35) * mm});
            skLineSegment(sketch, "E1007", {"start": v(-38.08, -270.35) * mm, "end": v(-42.05, -268.44) * mm});
            skLineSegment(sketch, "E1008", {"start": v(-42.05, -268.44) * mm, "end": v(-44.7, -266.92) * mm});
            skLineSegment(sketch, "E1009", {"start": v(-44.7, -266.92) * mm, "end": v(-50.62, -263.16) * mm});
            skLineSegment(sketch, "E1010", {"start": v(-50.62, -263.16) * mm, "end": v(-54.23, -260.8) * mm});
            skLineSegment(sketch, "E1011", {"start": v(-54.23, -260.8) * mm, "end": v(-57.19, -258.56) * mm});
            skLineSegment(sketch, "E1012", {"start": v(-57.19, -258.56) * mm, "end": v(-58.65, -257.42) * mm});
            skLineSegment(sketch, "E1013", {"start": v(-58.65, -257.42) * mm, "end": v(-60.56, -255.65) * mm});
            skLineSegment(sketch, "E1014", {"start": v(-60.56, -255.65) * mm, "end": v(-62.92, -253.26) * mm});
            skLineSegment(sketch, "E1015", {"start": v(-62.92, -253.26) * mm, "end": v(-64.04, -251.98) * mm});
            skLineSegment(sketch, "E1016", {"start": v(-64.04, -251.98) * mm, "end": v(-65.8, -249.62) * mm});
            skLineSegment(sketch, "E1017", {"start": v(-65.8, -249.62) * mm, "end": v(-67.66, -246.7) * mm});
            skLineSegment(sketch, "E1018", {"start": v(-67.66, -246.7) * mm, "end": v(-68.98, -244.24) * mm});
            skLineSegment(sketch, "E1019", {"start": v(-68.98, -244.24) * mm, "end": v(-69.99, -242.29) * mm});
            skLineSegment(sketch, "E1020", {"start": v(-69.99, -242.29) * mm, "end": v(-71.2, -239.6) * mm});
            skLineSegment(sketch, "E1021", {"start": v(-71.2, -239.6) * mm, "end": v(-71.62, -238.35) * mm});
            skLineSegment(sketch, "E1022", {"start": v(-74.39, -217.36) * mm, "end": v(-73.93, -214.3) * mm});
            skLineSegment(sketch, "E1023", {"start": v(-73.93, -214.3) * mm, "end": v(-73.02, -210.84) * mm});
            skLineSegment(sketch, "E1024", {"start": v(-73.02, -210.84) * mm, "end": v(-71.9, -207.44) * mm});
            skLineSegment(sketch, "E1025", {"start": v(-71.9, -207.44) * mm, "end": v(-69.4, -201.8) * mm});
            skLineSegment(sketch, "E1026", {"start": v(-69.4, -201.8) * mm, "end": v(-68.08, -199.37) * mm});
            skLineSegment(sketch, "E1027", {"start": v(-65.66, -195.9) * mm, "end": v(-63.46, -192.85) * mm});
            skLineSegment(sketch, "E1028", {"start": v(-63.46, -192.85) * mm, "end": v(-61.48, -190.68) * mm});
            skLineSegment(sketch, "E1029", {"start": v(-61.48, -190.68) * mm, "end": v(-60, -189.21) * mm});
            skLineSegment(sketch, "E1030", {"start": v(-57.06, -186.86) * mm, "end": v(-54.09, -184.7) * mm});
            skLineSegment(sketch, "E1031", {"start": v(-54.09, -184.7) * mm, "end": v(-51.05, -182.66) * mm});
            skLineSegment(sketch, "E1032", {"start": v(-51.05, -182.66) * mm, "end": v(-46.54, -179.82) * mm});
            skLineSegment(sketch, "E1033", {"start": v(-46.54, -179.82) * mm, "end": v(-43.64, -178.02) * mm});
            skLineSegment(sketch, "E1034", {"start": v(-43.64, -178.02) * mm, "end": v(-41.96, -177.05) * mm});
            skLineSegment(sketch, "E1035", {"start": v(-36.8, -174.67) * mm, "end": v(-33.96, -173.77) * mm});
            skLineSegment(sketch, "E1036", {"start": v(-33.96, -173.77) * mm, "end": v(-29.39, -172.6) * mm});
            skLineSegment(sketch, "E1037", {"start": v(-29.39, -172.6) * mm, "end": v(-24.77, -171.78) * mm});
            skLineSegment(sketch, "E1038", {"start": v(-24.77, -171.78) * mm, "end": v(-22.57, -171.44) * mm});
            skLineSegment(sketch, "E1039", {"start": v(-17.61, -171.17) * mm, "end": v(-12.52, -171.51) * mm});
            skLineSegment(sketch, "E1040", {"start": v(-12.52, -171.51) * mm, "end": v(-8.2, -171.92) * mm});
            skLineSegment(sketch, "E1041", {"start": v(-8.2, -171.92) * mm, "end": v(-4.5, -172.47) * mm});
            skLineSegment(sketch, "E1042", {"start": v(-4.5, -172.47) * mm, "end": v(-1.12, -173.22) * mm});
            skLineSegment(sketch, "E1043", {"start": v(-1.12, -173.22) * mm, "end": v(4.1, -174.68) * mm});
            skLineSegment(sketch, "E1044", {"start": v(4.1, -174.68) * mm, "end": v(8.91, -176.2) * mm});
            skLineSegment(sketch, "E1045", {"start": v(8.91, -176.2) * mm, "end": v(14.1, -178.19) * mm});
            skLineSegment(sketch, "E1046", {"start": v(14.1, -178.19) * mm, "end": v(20.37, -181.44) * mm});
            skLineSegment(sketch, "E1047", {"start": v(20.37, -181.44) * mm, "end": v(24.63, -184.16) * mm});
            skLineSegment(sketch, "E1048", {"start": v(24.63, -184.16) * mm, "end": v(28.3, -187.06) * mm});
            skLineSegment(sketch, "E1049", {"start": v(28.3, -187.06) * mm, "end": v(32.68, -190.33) * mm});
            skLineSegment(sketch, "E1050", {"start": v(32.68, -190.33) * mm, "end": v(35.78, -192.75) * mm});
            skLineSegment(sketch, "E1051", {"start": v(35.78, -192.75) * mm, "end": v(38.08, -194.22) * mm});
            skLineSegment(sketch, "E1052", {"start": v(79.25, -222.81) * mm, "end": v(79.12, -223.7) * mm});
            skLineSegment(sketch, "E1053", {"start": v(79.12, -223.7) * mm, "end": v(78.48, -224.68) * mm});
            skLineSegment(sketch, "E1054", {"start": v(78.48, -224.68) * mm, "end": v(77.26, -225.42) * mm});
            skLineSegment(sketch, "E1055", {"start": v(77.26, -225.42) * mm, "end": v(74.83, -226.6) * mm});
            skLineSegment(sketch, "E1056", {"start": v(74.83, -226.6) * mm, "end": v(72.3, -227.6) * mm});
            skLineSegment(sketch, "E1057", {"start": v(72.3, -227.6) * mm, "end": v(68.65, -229.1) * mm});
            skLineSegment(sketch, "E1058", {"start": v(68.65, -229.1) * mm, "end": v(65.45, -230.67) * mm});
            skLineSegment(sketch, "E1059", {"start": v(65.45, -230.67) * mm, "end": v(61.12, -233.09) * mm});
            skLineSegment(sketch, "E1060", {"start": v(61.12, -233.09) * mm, "end": v(55.88, -236.15) * mm});
            skLineSegment(sketch, "E1061", {"start": v(55.88, -236.15) * mm, "end": v(50.37, -239.8) * mm});
            skLineSegment(sketch, "E1062", {"start": v(50.37, -239.8) * mm, "end": v(43.92, -243.61) * mm});
            skLineSegment(sketch, "E1063", {"start": v(43.92, -243.61) * mm, "end": v(39.72, -246.4) * mm});
            skLineSegment(sketch, "E1064", {"start": v(39.72, -246.4) * mm, "end": v(32.48, -251.2) * mm});
            skLineSegment(sketch, "E1065", {"start": v(32.48, -251.2) * mm, "end": v(29.37, -253.65) * mm});
            skLineSegment(sketch, "E1066", {"start": v(29.37, -253.65) * mm, "end": v(26.62, -255.9) * mm});
            skLineSegment(sketch, "E1067", {"start": v(26.62, -255.9) * mm, "end": v(24.55, -257.43) * mm});
            skLineSegment(sketch, "E1068", {"start": v(24.55, -257.43) * mm, "end": v(22.05, -259.5) * mm});
            skLineSegment(sketch, "E1069", {"start": v(22.05, -259.5) * mm, "end": v(18.9, -261.3) * mm});
            skLineSegment(sketch, "E1070", {"start": v(18.9, -261.3) * mm, "end": v(15.71, -263.03) * mm});
            skLineSegment(sketch, "E1071", {"start": v(15.71, -263.03) * mm, "end": v(10.6, -265.04) * mm});
            skLineSegment(sketch, "E1072", {"start": v(10.6, -265.04) * mm, "end": v(4.37, -267.06) * mm});
            skLineSegment(sketch, "E1073", {"start": v(4.37, -267.06) * mm, "end": v(-3.39, -269.68) * mm});
            skLineSegment(sketch, "E1074", {"start": v(-3.39, -269.68) * mm, "end": v(-7.78, -270.73) * mm});
            skLineSegment(sketch, "E1075", {"start": v(-7.78, -270.73) * mm, "end": v(-12.28, -271.26) * mm});
            skLineSegment(sketch, "E1076", {"start": v(-12.28, -271.26) * mm, "end": v(-18.5, -271.26) * mm});
            skLineSegment(sketch, "E1077", {"start": v(-18.5, -271.26) * mm, "end": v(-21.89, -270.93) * mm});
            skLineSegment(sketch, "E1078", {"start": v(-21.89, -270.93) * mm, "end": v(-27.33, -269.83) * mm});
            skLineSegment(sketch, "E1079", {"start": v(-27.33, -269.83) * mm, "end": v(-32.63, -268.5) * mm});
            skLineSegment(sketch, "E1080", {"start": v(-32.63, -268.5) * mm, "end": v(-36.9, -267.15) * mm});
            skLineSegment(sketch, "E1081", {"start": v(-36.9, -267.15) * mm, "end": v(-40.49, -265.6) * mm});
            skLineSegment(sketch, "E1082", {"start": v(-40.49, -265.6) * mm, "end": v(-43.8, -263.84) * mm});
            skLineSegment(sketch, "E1083", {"start": v(-43.8, -263.84) * mm, "end": v(-47.22, -261.75) * mm});
            skLineSegment(sketch, "E1084", {"start": v(-47.22, -261.75) * mm, "end": v(-52.2, -258.14) * mm});
            skLineSegment(sketch, "E1085", {"start": v(-52.2, -258.14) * mm, "end": v(-54.86, -256.08) * mm});
            skLineSegment(sketch, "E1086", {"start": v(-54.86, -256.08) * mm, "end": v(-59.1, -252.33) * mm});
            skLineSegment(sketch, "E1087", {"start": v(-59.1, -252.33) * mm, "end": v(-61.19, -250.2) * mm});
            skLineSegment(sketch, "E1088", {"start": v(-61.19, -250.2) * mm, "end": v(-64.5, -245.76) * mm});
            skLineSegment(sketch, "E1089", {"start": v(-64.5, -245.76) * mm, "end": v(-65.97, -243.18) * mm});
            skLineSegment(sketch, "E1090", {"start": v(-65.97, -243.18) * mm, "end": v(-66.87, -241.4) * mm});
            skLineSegment(sketch, "E1091", {"start": v(-66.87, -241.4) * mm, "end": v(-67.45, -239.93) * mm});
            skLineSegment(sketch, "E1092", {"start": v(-67.45, -239.93) * mm, "end": v(-68.7, -236.82) * mm});
            skLineSegment(sketch, "E1093", {"start": v(-68.7, -236.82) * mm, "end": v(-69.7, -233.45) * mm});
            skLineSegment(sketch, "E1094", {"start": v(-69.7, -233.45) * mm, "end": v(-70.63, -229.3) * mm});
            skLineSegment(sketch, "E1095", {"start": v(-70.63, -229.3) * mm, "end": v(-71.04, -226.73) * mm});
            skLineSegment(sketch, "E1096", {"start": v(-71.04, -226.73) * mm, "end": v(-71.31, -223.48) * mm});
            skLineSegment(sketch, "E1097", {"start": v(-71.31, -223.48) * mm, "end": v(-71.31, -220.52) * mm});
            skLineSegment(sketch, "E1098", {"start": v(-71.31, -220.52) * mm, "end": v(-70.84, -217.08) * mm});
            skLineSegment(sketch, "E1099", {"start": v(-70.84, -217.08) * mm, "end": v(-70.17, -213.64) * mm});
            skLineSegment(sketch, "E1100", {"start": v(-70.17, -213.64) * mm, "end": v(-68.3, -207.33) * mm});
            skLineSegment(sketch, "E1101", {"start": v(-68.3, -207.33) * mm, "end": v(-65.89, -202.09) * mm});
            skLineSegment(sketch, "E1102", {"start": v(-65.89, -202.09) * mm, "end": v(-63.54, -198.35) * mm});
            skLineSegment(sketch, "E1103", {"start": v(-63.54, -198.35) * mm, "end": v(-60.93, -195.07) * mm});
            skLineSegment(sketch, "E1104", {"start": v(-60.93, -195.07) * mm, "end": v(-58.53, -192.7) * mm});
            skLineSegment(sketch, "E1105", {"start": v(-58.53, -192.7) * mm, "end": v(-55.58, -190.08) * mm});
            skLineSegment(sketch, "E1106", {"start": v(-55.58, -190.08) * mm, "end": v(-51.85, -187.15) * mm});
            skLineSegment(sketch, "E1107", {"start": v(-51.85, -187.15) * mm, "end": v(-48.2, -184.55) * mm});
            skLineSegment(sketch, "E1108", {"start": v(-48.2, -184.55) * mm, "end": v(-45.1, -182.5) * mm});
            skLineSegment(sketch, "E1109", {"start": v(-45.1, -182.5) * mm, "end": v(-41.73, -180.61) * mm});
            skLineSegment(sketch, "E1110", {"start": v(-41.73, -180.61) * mm, "end": v(-38.61, -179.17) * mm});
            skLineSegment(sketch, "E1111", {"start": v(-38.61, -179.17) * mm, "end": v(-36.16, -178.23) * mm});
            skLineSegment(sketch, "E1112", {"start": v(-36.16, -178.23) * mm, "end": v(-32.85, -177.2) * mm});
            skLineSegment(sketch, "E1113", {"start": v(-32.85, -177.2) * mm, "end": v(-28.72, -176.1) * mm});
            skLineSegment(sketch, "E1114", {"start": v(-28.72, -176.1) * mm, "end": v(-25.12, -175.27) * mm});
            skLineSegment(sketch, "E1115", {"start": v(-25.12, -175.27) * mm, "end": v(-21.3, -174.61) * mm});
            skLineSegment(sketch, "E1116", {"start": v(-21.3, -174.61) * mm, "end": v(-18.65, -174.35) * mm});
            skLineSegment(sketch, "E1117", {"start": v(-18.65, -174.35) * mm, "end": v(-14.79, -174.35) * mm});
            skLineSegment(sketch, "E1118", {"start": v(-14.79, -174.35) * mm, "end": v(-10.09, -174.6) * mm});
            skLineSegment(sketch, "E1119", {"start": v(-10.09, -174.6) * mm, "end": v(-6.82, -175.08) * mm});
            skLineSegment(sketch, "E1120", {"start": v(-6.82, -175.08) * mm, "end": v(-3.83, -175.79) * mm});
            skLineSegment(sketch, "E1121", {"start": v(-3.83, -175.79) * mm, "end": v(-0.42, -176.86) * mm});
            skLineSegment(sketch, "E1122", {"start": v(-0.42, -176.86) * mm, "end": v(4.76, -178.65) * mm});
            skLineSegment(sketch, "E1123", {"start": v(4.76, -178.65) * mm, "end": v(12.33, -181.3) * mm});
            skLineSegment(sketch, "E1124", {"start": v(12.33, -181.3) * mm, "end": v(15.73, -182.77) * mm});
            skLineSegment(sketch, "E1125", {"start": v(15.73, -182.77) * mm, "end": v(19.4, -184.7) * mm});
            skLineSegment(sketch, "E1126", {"start": v(19.4, -184.7) * mm, "end": v(22.76, -186.78) * mm});
            skLineSegment(sketch, "E1127", {"start": v(22.76, -186.78) * mm, "end": v(25.55, -188.96) * mm});
            skLineSegment(sketch, "E1128", {"start": v(25.55, -188.96) * mm, "end": v(28.78, -191.48) * mm});
            skLineSegment(sketch, "E1129", {"start": v(28.78, -191.48) * mm, "end": v(32.84, -194.49) * mm});
            skLineSegment(sketch, "E1130", {"start": v(32.84, -194.49) * mm, "end": v(36.19, -196.76) * mm});
            skLineSegment(sketch, "E1131", {"start": v(36.19, -196.76) * mm, "end": v(38.95, -198.67) * mm});
            skLineSegment(sketch, "E1132", {"start": v(38.95, -198.67) * mm, "end": v(43.55, -201.82) * mm});
            skLineSegment(sketch, "E1133", {"start": v(43.55, -201.82) * mm, "end": v(48.03, -204.88) * mm});
            skLineSegment(sketch, "E1134", {"start": v(48.03, -204.88) * mm, "end": v(53.11, -208.33) * mm});
            skLineSegment(sketch, "E1135", {"start": v(53.11, -208.33) * mm, "end": v(57.08, -210.56) * mm});
            skLineSegment(sketch, "E1136", {"start": v(57.08, -210.56) * mm, "end": v(62.46, -213.33) * mm});
            skLineSegment(sketch, "E1137", {"start": v(62.46, -213.33) * mm, "end": v(69.43, -216.76) * mm});
            skLineSegment(sketch, "E1138", {"start": v(69.43, -216.76) * mm, "end": v(74.56, -218.75) * mm});
            skLineSegment(sketch, "E1139", {"start": v(74.56, -218.75) * mm, "end": v(76.95, -219.79) * mm});
            skLineSegment(sketch, "E1140", {"start": v(76.95, -219.79) * mm, "end": v(78.18, -220.52) * mm});
            skLineSegment(sketch, "E1141", {"start": v(78.18, -220.52) * mm, "end": v(79, -221.43) * mm});
            skLineSegment(sketch, "E1142", {"start": v(79, -221.43) * mm, "end": v(79.25, -222.81) * mm});
            skLineSegment(sketch, "E1143", {"start": v(59.82, -231.36) * mm, "end": v(55.28, -234.04) * mm});
            skLineSegment(sketch, "E1144", {"start": v(55.28, -234.04) * mm, "end": v(51.82, -236.33) * mm});
            skLineSegment(sketch, "E1145", {"start": v(51.82, -236.33) * mm, "end": v(40.76, -242.52) * mm});
            skLineSegment(sketch, "E1146", {"start": v(40.76, -242.52) * mm, "end": v(33.6, -246.52) * mm});
            skLineSegment(sketch, "E1147", {"start": v(33.6, -246.52) * mm, "end": v(30.64, -248.4) * mm});
            skLineSegment(sketch, "E1148", {"start": v(30.64, -248.4) * mm, "end": v(27.68, -250.88) * mm});
            skLineSegment(sketch, "E1149", {"start": v(27.68, -250.88) * mm, "end": v(25.42, -252.79) * mm});
            skLineSegment(sketch, "E1150", {"start": v(25.42, -252.79) * mm, "end": v(21.8, -255.8) * mm});
            skLineSegment(sketch, "E1151", {"start": v(21.8, -255.8) * mm, "end": v(17.86, -258.17) * mm});
            skLineSegment(sketch, "E1152", {"start": v(17.86, -258.17) * mm, "end": v(12.58, -260.68) * mm});
            skLineSegment(sketch, "E1153", {"start": v(12.58, -260.68) * mm, "end": v(7.1, -262.67) * mm});
            skLineSegment(sketch, "E1154", {"start": v(7.1, -262.67) * mm, "end": v(2.92, -264.09) * mm});
            skLineSegment(sketch, "E1155", {"start": v(2.92, -264.09) * mm, "end": v(-3.1, -266.23) * mm});
            skLineSegment(sketch, "E1156", {"start": v(-3.1, -266.23) * mm, "end": v(-7.2, -267.35) * mm});
            skLineSegment(sketch, "E1157", {"start": v(-7.2, -267.35) * mm, "end": v(-11.52, -267.85) * mm});
            skLineSegment(sketch, "E1158", {"start": v(-11.52, -267.85) * mm, "end": v(-14.76, -268.06) * mm});
            skLineSegment(sketch, "E1159", {"start": v(-14.76, -268.06) * mm, "end": v(-18.04, -267.97) * mm});
            skLineSegment(sketch, "E1160", {"start": v(-18.04, -267.97) * mm, "end": v(-21.95, -267.47) * mm});
            skLineSegment(sketch, "E1161", {"start": v(-21.95, -267.47) * mm, "end": v(-28.73, -265.97) * mm});
            skLineSegment(sketch, "E1162", {"start": v(-28.73, -265.97) * mm, "end": v(-36.06, -263.56) * mm});
            skLineSegment(sketch, "E1163", {"start": v(-36.06, -263.56) * mm, "end": v(-39.52, -261.96) * mm});
            skLineSegment(sketch, "E1164", {"start": v(-39.52, -261.96) * mm, "end": v(-43.41, -259.7) * mm});
            skLineSegment(sketch, "E1165", {"start": v(-43.41, -259.7) * mm, "end": v(-46.06, -257.93) * mm});
            skLineSegment(sketch, "E1166", {"start": v(-46.06, -257.93) * mm, "end": v(-48.92, -255.76) * mm});
            skLineSegment(sketch, "E1167", {"start": v(-48.92, -255.76) * mm, "end": v(-52.1, -253.01) * mm});
            skLineSegment(sketch, "E1168", {"start": v(-52.1, -253.01) * mm, "end": v(-54.36, -250.74) * mm});
            skLineSegment(sketch, "E1169", {"start": v(-54.36, -250.74) * mm, "end": v(-57.62, -246.85) * mm});
            skLineSegment(sketch, "E1170", {"start": v(-57.62, -246.85) * mm, "end": v(-60.36, -242.99) * mm});
            skLineSegment(sketch, "E1171", {"start": v(-60.36, -242.99) * mm, "end": v(-62.55, -239.08) * mm});
            skLineSegment(sketch, "E1172", {"start": v(-62.55, -239.08) * mm, "end": v(-64.27, -234.83) * mm});
            skLineSegment(sketch, "E1173", {"start": v(-64.27, -234.83) * mm, "end": v(-65.16, -231.93) * mm});
            skLineSegment(sketch, "E1174", {"start": v(-65.16, -231.93) * mm, "end": v(-66.25, -227.21) * mm});
            skLineSegment(sketch, "E1175", {"start": v(-66.25, -227.21) * mm, "end": v(-66.47, -221.67) * mm});
            skLineSegment(sketch, "E1176", {"start": v(-66.47, -221.67) * mm, "end": v(-66.05, -217.23) * mm});
            skLineSegment(sketch, "E1177", {"start": v(-66.05, -217.23) * mm, "end": v(-64.87, -212.37) * mm});
            skLineSegment(sketch, "E1178", {"start": v(-64.87, -212.37) * mm, "end": v(-63.11, -207.71) * mm});
            skLineSegment(sketch, "E1179", {"start": v(-63.11, -207.71) * mm, "end": v(-60.44, -202.71) * mm});
            skLineSegment(sketch, "E1180", {"start": v(-60.44, -202.71) * mm, "end": v(-57.5, -198.46) * mm});
            skLineSegment(sketch, "E1181", {"start": v(-57.5, -198.46) * mm, "end": v(-53.8, -194.22) * mm});
            skLineSegment(sketch, "E1182", {"start": v(-53.8, -194.22) * mm, "end": v(-50.43, -190.93) * mm});
            skLineSegment(sketch, "E1183", {"start": v(-50.43, -190.93) * mm, "end": v(-45.24, -187.06) * mm});
            skLineSegment(sketch, "E1184", {"start": v(-45.24, -187.06) * mm, "end": v(-40.8, -184.3) * mm});
            skLineSegment(sketch, "E1185", {"start": v(-40.8, -184.3) * mm, "end": v(-36.83, -182.4) * mm});
            skLineSegment(sketch, "E1186", {"start": v(-36.83, -182.4) * mm, "end": v(-31.85, -180.64) * mm});
            skLineSegment(sketch, "E1187", {"start": v(-31.85, -180.64) * mm, "end": v(-24.56, -178.64) * mm});
            skLineSegment(sketch, "E1188", {"start": v(-24.56, -178.64) * mm, "end": v(-19.52, -177.68) * mm});
            skLineSegment(sketch, "E1189", {"start": v(-19.52, -177.68) * mm, "end": v(-15.3, -177.5) * mm});
            skLineSegment(sketch, "E1190", {"start": v(-15.3, -177.5) * mm, "end": v(-8.78, -177.95) * mm});
            skLineSegment(sketch, "E1191", {"start": v(-8.78, -177.95) * mm, "end": v(-4.86, -178.84) * mm});
            skLineSegment(sketch, "E1192", {"start": v(-4.86, -178.84) * mm, "end": v(0, -180.36) * mm});
            skLineSegment(sketch, "E1193", {"start": v(0, -180.36) * mm, "end": v(5.71, -182.46) * mm});
            skLineSegment(sketch, "E1194", {"start": v(5.71, -182.46) * mm, "end": v(11.97, -184.75) * mm});
            skLineSegment(sketch, "E1195", {"start": v(11.97, -184.75) * mm, "end": v(15.68, -186.41) * mm});
            skLineSegment(sketch, "E1196", {"start": v(15.68, -186.41) * mm, "end": v(19.66, -188.6) * mm});
            skLineSegment(sketch, "E1197", {"start": v(19.66, -188.6) * mm, "end": v(23.37, -191.23) * mm});
            skLineSegment(sketch, "E1198", {"start": v(23.37, -191.23) * mm, "end": v(27.54, -194.65) * mm});
            skLineSegment(sketch, "E1199", {"start": v(27.54, -194.65) * mm, "end": v(31.13, -197.45) * mm});
            skLineSegment(sketch, "E1200", {"start": v(31.13, -197.45) * mm, "end": v(34.5, -199.47) * mm});
            skLineSegment(sketch, "E1201", {"start": v(34.5, -199.47) * mm, "end": v(43.68, -204.8) * mm});
            skLineSegment(sketch, "E1202", {"start": v(43.68, -204.8) * mm, "end": v(50.16, -208.97) * mm});
            skLineSegment(sketch, "E1203", {"start": v(50.16, -208.97) * mm, "end": v(54.33, -211.58) * mm});
            skLineSegment(sketch, "E1204", {"start": v(54.33, -211.58) * mm, "end": v(58.08, -213.6) * mm});
            skLineSegment(sketch, "E1205", {"start": v(58.08, -213.6) * mm, "end": v(63.87, -216.58) * mm});
            skLineSegment(sketch, "E1206", {"start": v(63.87, -216.58) * mm, "end": v(66.46, -218.22) * mm});
            skLineSegment(sketch, "E1207", {"start": v(66.46, -218.22) * mm, "end": v(69.01, -219.48) * mm});
            skLineSegment(sketch, "E1208", {"start": v(69.01, -219.48) * mm, "end": v(71.4, -220.63) * mm});
            skLineSegment(sketch, "E1209", {"start": v(71.4, -220.63) * mm, "end": v(72.3, -221.3) * mm});
            skLineSegment(sketch, "E1210", {"start": v(72.3, -221.3) * mm, "end": v(72.82, -221.76) * mm});
            skLineSegment(sketch, "E1211", {"start": v(72.82, -221.76) * mm, "end": v(73.24, -222.35) * mm});
            skLineSegment(sketch, "E1212", {"start": v(73.24, -222.35) * mm, "end": v(73.25, -223.26) * mm});
            skLineSegment(sketch, "E1213", {"start": v(73.25, -223.26) * mm, "end": v(72.78, -223.89) * mm});
            skLineSegment(sketch, "E1214", {"start": v(72.78, -223.89) * mm, "end": v(71.12, -225.04) * mm});
            skLineSegment(sketch, "E1215", {"start": v(71.12, -225.04) * mm, "end": v(67.4, -226.83) * mm});
            skLineSegment(sketch, "E1216", {"start": v(67.4, -226.83) * mm, "end": v(64.55, -228.4) * mm});
            skLineSegment(sketch, "E1217", {"start": v(64.55, -228.4) * mm, "end": v(62.04, -230) * mm});
            skLineSegment(sketch, "E1218", {"start": v(62.04, -230) * mm, "end": v(59.82, -231.36) * mm});
            skLineSegment(sketch, "E1219", {"start": v(61.84, -227.6) * mm, "end": v(58.57, -229.76) * mm});
            skLineSegment(sketch, "E1220", {"start": v(58.57, -229.76) * mm, "end": v(54.94, -231.95) * mm});
            skLineSegment(sketch, "E1221", {"start": v(54.94, -231.95) * mm, "end": v(49.97, -234.58) * mm});
            skLineSegment(sketch, "E1222", {"start": v(49.97, -234.58) * mm, "end": v(36.18, -241.8) * mm});
            skLineSegment(sketch, "E1223", {"start": v(36.18, -241.8) * mm, "end": v(31.89, -244.2) * mm});
            skLineSegment(sketch, "E1224", {"start": v(31.89, -244.2) * mm, "end": v(28.22, -246.78) * mm});
            skLineSegment(sketch, "E1225", {"start": v(28.22, -246.78) * mm, "end": v(25.76, -248.82) * mm});
            skLineSegment(sketch, "E1226", {"start": v(25.76, -248.82) * mm, "end": v(22.86, -251.13) * mm});
            skLineSegment(sketch, "E1227", {"start": v(22.86, -251.13) * mm, "end": v(19.77, -253.44) * mm});
            skLineSegment(sketch, "E1228", {"start": v(19.77, -253.44) * mm, "end": v(16.34, -255.24) * mm});
            skLineSegment(sketch, "E1229", {"start": v(16.34, -255.24) * mm, "end": v(13.18, -256.8) * mm});
            skLineSegment(sketch, "E1230", {"start": v(13.18, -256.8) * mm, "end": v(9.31, -258.24) * mm});
            skLineSegment(sketch, "E1231", {"start": v(9.31, -258.24) * mm, "end": v(-1.58, -262) * mm});
            skLineSegment(sketch, "E1232", {"start": v(-1.58, -262) * mm, "end": v(-5.55, -263.16) * mm});
            skLineSegment(sketch, "E1233", {"start": v(-5.55, -263.16) * mm, "end": v(-9.7, -263.89) * mm});
            skLineSegment(sketch, "E1234", {"start": v(-9.7, -263.89) * mm, "end": v(-14, -264.32) * mm});
            skLineSegment(sketch, "E1235", {"start": v(-14, -264.32) * mm, "end": v(-17.4, -264.32) * mm});
            skLineSegment(sketch, "E1236", {"start": v(-17.4, -264.32) * mm, "end": v(-22.62, -264.05) * mm});
            skLineSegment(sketch, "E1237", {"start": v(-22.62, -264.05) * mm, "end": v(-27, -263.06) * mm});
            skLineSegment(sketch, "E1238", {"start": v(-27, -263.06) * mm, "end": v(-32.74, -261.36) * mm});
            skLineSegment(sketch, "E1239", {"start": v(-32.74, -261.36) * mm, "end": v(-36.43, -259.88) * mm});
            skLineSegment(sketch, "E1240", {"start": v(-36.43, -259.88) * mm, "end": v(-39.9, -258.06) * mm});
            skLineSegment(sketch, "E1241", {"start": v(-39.9, -258.06) * mm, "end": v(-43.68, -255.57) * mm});
            skLineSegment(sketch, "E1242", {"start": v(-43.68, -255.57) * mm, "end": v(-47.32, -252.55) * mm});
            skLineSegment(sketch, "E1243", {"start": v(-47.32, -252.55) * mm, "end": v(-51.14, -248.65) * mm});
            skLineSegment(sketch, "E1244", {"start": v(-51.14, -248.65) * mm, "end": v(-53.7, -245.54) * mm});
            skLineSegment(sketch, "E1245", {"start": v(-53.7, -245.54) * mm, "end": v(-56.66, -240.7) * mm});
            skLineSegment(sketch, "E1246", {"start": v(-56.66, -240.7) * mm, "end": v(-58, -237.79) * mm});
            skLineSegment(sketch, "E1247", {"start": v(-58, -237.79) * mm, "end": v(-59.53, -233.56) * mm});
            skLineSegment(sketch, "E1248", {"start": v(-59.53, -233.56) * mm, "end": v(-60.56, -228.33) * mm});
            skLineSegment(sketch, "E1249", {"start": v(-60.56, -228.33) * mm, "end": v(-61.03, -224.45) * mm});
            skLineSegment(sketch, "E1250", {"start": v(-61.03, -224.45) * mm, "end": v(-60.89, -220.21) * mm});
            skLineSegment(sketch, "E1251", {"start": v(-60.89, -220.21) * mm, "end": v(-60.52, -216.55) * mm});
            skLineSegment(sketch, "E1252", {"start": v(-60.52, -216.55) * mm, "end": v(-59.75, -212.76) * mm});
            skLineSegment(sketch, "E1253", {"start": v(-59.75, -212.76) * mm, "end": v(-58.54, -209.06) * mm});
            skLineSegment(sketch, "E1254", {"start": v(-58.54, -209.06) * mm, "end": v(-56.72, -204.95) * mm});
            skLineSegment(sketch, "E1255", {"start": v(-56.72, -204.95) * mm, "end": v(-54.2, -200.71) * mm});
            skLineSegment(sketch, "E1256", {"start": v(-54.2, -200.71) * mm, "end": v(-51.55, -197.33) * mm});
            skLineSegment(sketch, "E1257", {"start": v(-51.55, -197.33) * mm, "end": v(-48.58, -194.22) * mm});
            skLineSegment(sketch, "E1258", {"start": v(-48.58, -194.22) * mm, "end": v(-43.72, -190.02) * mm});
            skLineSegment(sketch, "E1259", {"start": v(-43.72, -190.02) * mm, "end": v(-40.82, -188) * mm});
            skLineSegment(sketch, "E1260", {"start": v(-40.82, -188) * mm, "end": v(-36.47, -185.75) * mm});
            skLineSegment(sketch, "E1261", {"start": v(-36.47, -185.75) * mm, "end": v(-32.96, -184.3) * mm});
            skLineSegment(sketch, "E1262", {"start": v(-32.96, -184.3) * mm, "end": v(-28.43, -182.94) * mm});
            skLineSegment(sketch, "E1263", {"start": v(-28.43, -182.94) * mm, "end": v(-24.1, -181.82) * mm});
            skLineSegment(sketch, "E1264", {"start": v(-24.1, -181.82) * mm, "end": v(-19.34, -181.25) * mm});
            skLineSegment(sketch, "E1265", {"start": v(-19.34, -181.25) * mm, "end": v(-14.36, -181.25) * mm});
            skLineSegment(sketch, "E1266", {"start": v(-14.36, -181.25) * mm, "end": v(-11.14, -181.52) * mm});
            skLineSegment(sketch, "E1267", {"start": v(-11.14, -181.52) * mm, "end": v(-7.2, -182) * mm});
            skLineSegment(sketch, "E1268", {"start": v(-7.2, -182) * mm, "end": v(-3.75, -182.9) * mm});
            skLineSegment(sketch, "E1269", {"start": v(-3.75, -182.9) * mm, "end": v(7.35, -186.66) * mm});
            skLineSegment(sketch, "E1270", {"start": v(7.35, -186.66) * mm, "end": v(12.51, -188.67) * mm});
            skLineSegment(sketch, "E1271", {"start": v(12.51, -188.67) * mm, "end": v(16.87, -190.83) * mm});
            skLineSegment(sketch, "E1272", {"start": v(16.87, -190.83) * mm, "end": v(21.73, -193.65) * mm});
            skLineSegment(sketch, "E1273", {"start": v(21.73, -193.65) * mm, "end": v(24.12, -195.47) * mm});
            skLineSegment(sketch, "E1274", {"start": v(24.12, -195.47) * mm, "end": v(27.32, -198.08) * mm});
            skLineSegment(sketch, "E1275", {"start": v(27.32, -198.08) * mm, "end": v(29.14, -199.5) * mm});
            skLineSegment(sketch, "E1276", {"start": v(29.14, -199.5) * mm, "end": v(32.86, -201.87) * mm});
            skLineSegment(sketch, "E1277", {"start": v(32.86, -201.87) * mm, "end": v(36.47, -203.91) * mm});
            skLineSegment(sketch, "E1278", {"start": v(36.47, -203.91) * mm, "end": v(40.68, -206.16) * mm});
            skLineSegment(sketch, "E1279", {"start": v(40.68, -206.16) * mm, "end": v(48.21, -210.35) * mm});
            skLineSegment(sketch, "E1280", {"start": v(48.21, -210.35) * mm, "end": v(52.57, -212.84) * mm});
            skLineSegment(sketch, "E1281", {"start": v(52.57, -212.84) * mm, "end": v(58.84, -216.49) * mm});
            skLineSegment(sketch, "E1282", {"start": v(58.84, -216.49) * mm, "end": v(63.46, -219.24) * mm});
            skLineSegment(sketch, "E1283", {"start": v(63.46, -219.24) * mm, "end": v(65.22, -220.52) * mm});
            skLineSegment(sketch, "E1284", {"start": v(65.22, -220.52) * mm, "end": v(65.97, -221.35) * mm});
            skLineSegment(sketch, "E1285", {"start": v(65.97, -221.35) * mm, "end": v(66.44, -222.34) * mm});
            skLineSegment(sketch, "E1286", {"start": v(66.44, -222.34) * mm, "end": v(66.44, -223.3) * mm});
            skLineSegment(sketch, "E1287", {"start": v(66.44, -223.3) * mm, "end": v(66.07, -224.08) * mm});
            skLineSegment(sketch, "E1288", {"start": v(66.07, -224.08) * mm, "end": v(65.12, -225.03) * mm});
            skLineSegment(sketch, "E1289", {"start": v(65.12, -225.03) * mm, "end": v(63.14, -226.65) * mm});
            skLineSegment(sketch, "E1290", {"start": v(63.14, -226.65) * mm, "end": v(61.84, -227.6) * mm});
            skLineSegment(sketch, "E1291", {"start": v(61.51, -222.81) * mm, "end": v(61.51, -223.84) * mm});
            skLineSegment(sketch, "E1292", {"start": v(61.51, -223.84) * mm, "end": v(60.66, -225.13) * mm});
            skLineSegment(sketch, "E1293", {"start": v(60.66, -225.13) * mm, "end": v(58.14, -227.6) * mm});
            skLineSegment(sketch, "E1294", {"start": v(58.14, -227.6) * mm, "end": v(53.55, -230.4) * mm});
            skLineSegment(sketch, "E1295", {"start": v(53.55, -230.4) * mm, "end": v(47.46, -233.2) * mm});
            skLineSegment(sketch, "E1296", {"start": v(47.46, -233.2) * mm, "end": v(37.54, -237.91) * mm});
            skLineSegment(sketch, "E1297", {"start": v(37.54, -237.91) * mm, "end": v(31.5, -241.04) * mm});
            skLineSegment(sketch, "E1298", {"start": v(31.5, -241.04) * mm, "end": v(28.63, -242.78) * mm});
            skLineSegment(sketch, "E1299", {"start": v(28.63, -242.78) * mm, "end": v(21.97, -247.94) * mm});
            skLineSegment(sketch, "E1300", {"start": v(21.97, -247.94) * mm, "end": v(16.21, -251.46) * mm});
            skLineSegment(sketch, "E1301", {"start": v(16.21, -251.46) * mm, "end": v(11.96, -253.58) * mm});
            skLineSegment(sketch, "E1302", {"start": v(11.96, -253.58) * mm, "end": v(6.3, -255.9) * mm});
            skLineSegment(sketch, "E1303", {"start": v(6.3, -255.9) * mm, "end": v(-1.22, -258.5) * mm});
            skLineSegment(sketch, "E1304", {"start": v(-1.22, -258.5) * mm, "end": v(-5.37, -259.52) * mm});
            skLineSegment(sketch, "E1305", {"start": v(-5.37, -259.52) * mm, "end": v(-10.09, -260.22) * mm});
            skLineSegment(sketch, "E1306", {"start": v(-10.09, -260.22) * mm, "end": v(-18.1, -260.48) * mm});
            skLineSegment(sketch, "E1307", {"start": v(-18.1, -260.48) * mm, "end": v(-21.74, -260.1) * mm});
            skLineSegment(sketch, "E1308", {"start": v(-21.74, -260.1) * mm, "end": v(-25.67, -259.4) * mm});
            skLineSegment(sketch, "E1309", {"start": v(-25.67, -259.4) * mm, "end": v(-32.34, -257.13) * mm});
            skLineSegment(sketch, "E1310", {"start": v(-32.34, -257.13) * mm, "end": v(-37.42, -254.75) * mm});
            skLineSegment(sketch, "E1311", {"start": v(-37.42, -254.75) * mm, "end": v(-42.21, -251.46) * mm});
            skLineSegment(sketch, "E1312", {"start": v(-42.21, -251.46) * mm, "end": v(-45.24, -248.78) * mm});
            skLineSegment(sketch, "E1313", {"start": v(-45.24, -248.78) * mm, "end": v(-48.57, -244.93) * mm});
            skLineSegment(sketch, "E1314", {"start": v(-48.57, -244.93) * mm, "end": v(-51.57, -240.66) * mm});
            skLineSegment(sketch, "E1315", {"start": v(-51.57, -240.66) * mm, "end": v(-53.55, -237.1) * mm});
            skLineSegment(sketch, "E1316", {"start": v(-53.55, -237.1) * mm, "end": v(-55.55, -231.97) * mm});
            skLineSegment(sketch, "E1317", {"start": v(-55.55, -231.97) * mm, "end": v(-56.49, -227.56) * mm});
            skLineSegment(sketch, "E1318", {"start": v(-56.49, -227.56) * mm, "end": v(-56.75, -225.61) * mm});
            skLineSegment(sketch, "E1319", {"start": v(-56.75, -225.61) * mm, "end": v(-56.75, -220.15) * mm});
            skLineSegment(sketch, "E1320", {"start": v(-56.75, -220.15) * mm, "end": v(-56.35, -217.06) * mm});
            skLineSegment(sketch, "E1321", {"start": v(-56.35, -217.06) * mm, "end": v(-55.02, -211.91) * mm});
            skLineSegment(sketch, "E1322", {"start": v(-55.02, -211.91) * mm, "end": v(-53.2, -207.82) * mm});
            skLineSegment(sketch, "E1323", {"start": v(-53.2, -207.82) * mm, "end": v(-50.85, -203.75) * mm});
            skLineSegment(sketch, "E1324", {"start": v(-50.85, -203.75) * mm, "end": v(-48.13, -200.09) * mm});
            skLineSegment(sketch, "E1325", {"start": v(-48.13, -200.09) * mm, "end": v(-44.33, -195.87) * mm});
            skLineSegment(sketch, "E1326", {"start": v(-44.33, -195.87) * mm, "end": v(-41.03, -193.25) * mm});
            skLineSegment(sketch, "E1327", {"start": v(-41.03, -193.25) * mm, "end": v(-36.6, -190.53) * mm});
            skLineSegment(sketch, "E1328", {"start": v(-36.6, -190.53) * mm, "end": v(-31.74, -188.28) * mm});
            skLineSegment(sketch, "E1329", {"start": v(-31.74, -188.28) * mm, "end": v(-26.34, -186.41) * mm});
            skLineSegment(sketch, "E1330", {"start": v(-26.34, -186.41) * mm, "end": v(-22.29, -185.52) * mm});
            skLineSegment(sketch, "E1331", {"start": v(-22.29, -185.52) * mm, "end": v(-18.8, -185.18) * mm});
            skLineSegment(sketch, "E1332", {"start": v(-18.8, -185.18) * mm, "end": v(-13.33, -185.14) * mm});
            skLineSegment(sketch, "E1333", {"start": v(-13.33, -185.14) * mm, "end": v(-8.03, -185.67) * mm});
            skLineSegment(sketch, "E1334", {"start": v(-8.03, -185.67) * mm, "end": v(-3.29, -186.82) * mm});
            skLineSegment(sketch, "E1335", {"start": v(-3.29, -186.82) * mm, "end": v(1.29, -188.31) * mm});
            skLineSegment(sketch, "E1336", {"start": v(1.29, -188.31) * mm, "end": v(5.4, -189.76) * mm});
            skLineSegment(sketch, "E1337", {"start": v(5.4, -189.76) * mm, "end": v(9, -191.06) * mm});
            skLineSegment(sketch, "E1338", {"start": v(9, -191.06) * mm, "end": v(13.86, -193.18) * mm});
            skLineSegment(sketch, "E1339", {"start": v(13.86, -193.18) * mm, "end": v(18.67, -195.7) * mm});
            skLineSegment(sketch, "E1340", {"start": v(18.67, -195.7) * mm, "end": v(22.67, -198.23) * mm});
            skLineSegment(sketch, "E1341", {"start": v(22.67, -198.23) * mm, "end": v(27.03, -201.49) * mm});
            skLineSegment(sketch, "E1342", {"start": v(27.03, -201.49) * mm, "end": v(29.94, -203.56) * mm});
            skLineSegment(sketch, "E1343", {"start": v(29.94, -203.56) * mm, "end": v(33.22, -205.43) * mm});
            skLineSegment(sketch, "E1344", {"start": v(33.22, -205.43) * mm, "end": v(34.97, -206.3) * mm});
            skLineSegment(sketch, "E1345", {"start": v(34.97, -206.3) * mm, "end": v(38.08, -207.8) * mm});
            skLineSegment(sketch, "E1346", {"start": v(38.08, -207.8) * mm, "end": v(41.33, -209.4) * mm});
            skLineSegment(sketch, "E1347", {"start": v(41.33, -209.4) * mm, "end": v(49.33, -213.45) * mm});
            skLineSegment(sketch, "E1348", {"start": v(49.33, -213.45) * mm, "end": v(54.8, -216.78) * mm});
            skLineSegment(sketch, "E1349", {"start": v(54.8, -216.78) * mm, "end": v(58.64, -219.28) * mm});
            skLineSegment(sketch, "E1350", {"start": v(58.64, -219.28) * mm, "end": v(60.7, -221.01) * mm});
            skLineSegment(sketch, "E1351", {"start": v(60.7, -221.01) * mm, "end": v(61.41, -222.07) * mm});
            skLineSegment(sketch, "E1352", {"start": v(61.41, -222.07) * mm, "end": v(61.51, -222.81) * mm});
            skLineSegment(sketch, "E1353", {"start": v(56.43, -222.81) * mm, "end": v(56.43, -223.5) * mm});
            skLineSegment(sketch, "E1354", {"start": v(56.43, -223.5) * mm, "end": v(56, -224.3) * mm});
            skLineSegment(sketch, "E1355", {"start": v(56, -224.3) * mm, "end": v(55.04, -225.56) * mm});
            skLineSegment(sketch, "E1356", {"start": v(55.04, -225.56) * mm, "end": v(53.24, -227.6) * mm});
            skLineSegment(sketch, "E1357", {"start": v(53.24, -227.6) * mm, "end": v(51.35, -229.1) * mm});
            skLineSegment(sketch, "E1358", {"start": v(51.35, -229.1) * mm, "end": v(48.82, -230.28) * mm});
            skLineSegment(sketch, "E1359", {"start": v(48.82, -230.28) * mm, "end": v(45.6, -231.58) * mm});
            skLineSegment(sketch, "E1360", {"start": v(45.6, -231.58) * mm, "end": v(35.7, -235.65) * mm});
            skLineSegment(sketch, "E1361", {"start": v(35.7, -235.65) * mm, "end": v(30.4, -238.14) * mm});
            skLineSegment(sketch, "E1362", {"start": v(30.4, -238.14) * mm, "end": v(26.63, -240.45) * mm});
            skLineSegment(sketch, "E1363", {"start": v(26.63, -240.45) * mm, "end": v(21.35, -244.38) * mm});
            skLineSegment(sketch, "E1364", {"start": v(21.35, -244.38) * mm, "end": v(15.24, -247.79) * mm});
            skLineSegment(sketch, "E1365", {"start": v(15.24, -247.79) * mm, "end": v(9.94, -250.43) * mm});
            skLineSegment(sketch, "E1366", {"start": v(9.94, -250.43) * mm, "end": v(6.75, -251.74) * mm});
            skLineSegment(sketch, "E1367", {"start": v(6.75, -251.74) * mm, "end": v(1.38, -253.53) * mm});
            skLineSegment(sketch, "E1368", {"start": v(1.38, -253.53) * mm, "end": v(-4, -255.05) * mm});
            skLineSegment(sketch, "E1369", {"start": v(-4, -255.05) * mm, "end": v(-8.32, -255.75) * mm});
            skLineSegment(sketch, "E1370", {"start": v(-8.32, -255.75) * mm, "end": v(-14.98, -256) * mm});
            skLineSegment(sketch, "E1371", {"start": v(-14.98, -256) * mm, "end": v(-19.1, -256) * mm});
            skLineSegment(sketch, "E1372", {"start": v(-19.1, -256) * mm, "end": v(-24.03, -255.13) * mm});
            skLineSegment(sketch, "E1373", {"start": v(-24.03, -255.13) * mm, "end": v(-27.96, -254) * mm});
            skLineSegment(sketch, "E1374", {"start": v(-27.96, -254) * mm, "end": v(-32.01, -252.21) * mm});
            skLineSegment(sketch, "E1375", {"start": v(-32.01, -252.21) * mm, "end": v(-35.35, -250.49) * mm});
            skLineSegment(sketch, "E1376", {"start": v(-35.35, -250.49) * mm, "end": v(-38.94, -248) * mm});
            skLineSegment(sketch, "E1377", {"start": v(-38.94, -248) * mm, "end": v(-42.06, -245.1) * mm});
            skLineSegment(sketch, "E1378", {"start": v(-42.06, -245.1) * mm, "end": v(-45.07, -241.5) * mm});
            skLineSegment(sketch, "E1379", {"start": v(-45.07, -241.5) * mm, "end": v(-47.42, -237.87) * mm});
            skLineSegment(sketch, "E1380", {"start": v(-47.42, -237.87) * mm, "end": v(-49.69, -233.82) * mm});
            skLineSegment(sketch, "E1381", {"start": v(-49.69, -233.82) * mm, "end": v(-50.7, -231.36) * mm});
            skLineSegment(sketch, "E1382", {"start": v(-50.7, -231.36) * mm, "end": v(-51.53, -228.95) * mm});
            skLineSegment(sketch, "E1383", {"start": v(-51.53, -228.95) * mm, "end": v(-51.98, -225.8) * mm});
            skLineSegment(sketch, "E1384", {"start": v(-51.98, -225.8) * mm, "end": v(-52.04, -223.13) * mm});
            skLineSegment(sketch, "E1385", {"start": v(-52.04, -223.13) * mm, "end": v(-52.02, -220.62) * mm});
            skLineSegment(sketch, "E1386", {"start": v(-52.02, -220.62) * mm, "end": v(-51.53, -216.55) * mm});
            skLineSegment(sketch, "E1387", {"start": v(-51.53, -216.55) * mm, "end": v(-50.42, -213.07) * mm});
            skLineSegment(sketch, "E1388", {"start": v(-50.42, -213.07) * mm, "end": v(-47.5, -207.87) * mm});
            skLineSegment(sketch, "E1389", {"start": v(-47.5, -207.87) * mm, "end": v(-44.28, -203.17) * mm});
            skLineSegment(sketch, "E1390", {"start": v(-44.28, -203.17) * mm, "end": v(-42.06, -200.56) * mm});
            skLineSegment(sketch, "E1391", {"start": v(-42.06, -200.56) * mm, "end": v(-39.8, -198.3) * mm});
            skLineSegment(sketch, "E1392", {"start": v(-39.8, -198.3) * mm, "end": v(-36.55, -195.88) * mm});
            skLineSegment(sketch, "E1393", {"start": v(-36.55, -195.88) * mm, "end": v(-31.58, -193.1) * mm});
            skLineSegment(sketch, "E1394", {"start": v(-31.58, -193.1) * mm, "end": v(-27.01, -191.32) * mm});
            skLineSegment(sketch, "E1395", {"start": v(-27.01, -191.32) * mm, "end": v(-23.04, -190.2) * mm});
            skLineSegment(sketch, "E1396", {"start": v(-23.04, -190.2) * mm, "end": v(-18.9, -189.68) * mm});
            skLineSegment(sketch, "E1397", {"start": v(-18.9, -189.68) * mm, "end": v(-13.1, -189.6) * mm});
            skLineSegment(sketch, "E1398", {"start": v(-13.1, -189.6) * mm, "end": v(-7.17, -190.05) * mm});
            skLineSegment(sketch, "E1399", {"start": v(-7.17, -190.05) * mm, "end": v(-2.27, -190.98) * mm});
            skLineSegment(sketch, "E1400", {"start": v(-2.27, -190.98) * mm, "end": v(1.76, -192.17) * mm});
            skLineSegment(sketch, "E1401", {"start": v(1.76, -192.17) * mm, "end": v(7.1, -193.98) * mm});
            skLineSegment(sketch, "E1402", {"start": v(7.1, -193.98) * mm, "end": v(11.79, -196.12) * mm});
            skLineSegment(sketch, "E1403", {"start": v(11.79, -196.12) * mm, "end": v(19.06, -200.07) * mm});
            skLineSegment(sketch, "E1404", {"start": v(19.06, -200.07) * mm, "end": v(22.36, -202.01) * mm});
            skLineSegment(sketch, "E1405", {"start": v(22.36, -202.01) * mm, "end": v(25.76, -204.5) * mm});
            skLineSegment(sketch, "E1406", {"start": v(25.76, -204.5) * mm, "end": v(28.17, -206.12) * mm});
            skLineSegment(sketch, "E1407", {"start": v(28.17, -206.12) * mm, "end": v(30.37, -207.36) * mm});
            skLineSegment(sketch, "E1408", {"start": v(30.37, -207.36) * mm, "end": v(33.78, -209.04) * mm});
            skLineSegment(sketch, "E1409", {"start": v(33.78, -209.04) * mm, "end": v(37.85, -210.6) * mm});
            skLineSegment(sketch, "E1410", {"start": v(37.85, -210.6) * mm, "end": v(40.82, -211.77) * mm});
            skLineSegment(sketch, "E1411", {"start": v(40.82, -211.77) * mm, "end": v(43.3, -213) * mm});
            skLineSegment(sketch, "E1412", {"start": v(43.3, -213) * mm, "end": v(49.83, -216.27) * mm});
            skLineSegment(sketch, "E1413", {"start": v(49.83, -216.27) * mm, "end": v(51.2, -217.14) * mm});
            skLineSegment(sketch, "E1414", {"start": v(51.2, -217.14) * mm, "end": v(53.36, -218.96) * mm});
            skLineSegment(sketch, "E1415", {"start": v(53.36, -218.96) * mm, "end": v(55.82, -221.48) * mm});
            skLineSegment(sketch, "E1416", {"start": v(55.82, -221.48) * mm, "end": v(56.24, -222.04) * mm});
            skLineSegment(sketch, "E1417", {"start": v(56.24, -222.04) * mm, "end": v(56.43, -222.81) * mm});
            skLineSegment(sketch, "E1418", {"start": v(51.33, -222.81) * mm, "end": v(51.12, -223.98) * mm});
            skLineSegment(sketch, "E1419", {"start": v(51.12, -223.98) * mm, "end": v(50.37, -225.33) * mm});
            skLineSegment(sketch, "E1420", {"start": v(50.37, -225.33) * mm, "end": v(48.77, -226.87) * mm});
            skLineSegment(sketch, "E1421", {"start": v(48.77, -226.87) * mm, "end": v(45.76, -228.65) * mm});
            skLineSegment(sketch, "E1422", {"start": v(45.76, -228.65) * mm, "end": v(41, -230.54) * mm});
            skLineSegment(sketch, "E1423", {"start": v(41, -230.54) * mm, "end": v(33.4, -233.17) * mm});
            skLineSegment(sketch, "E1424", {"start": v(33.4, -233.17) * mm, "end": v(29.65, -234.84) * mm});
            skLineSegment(sketch, "E1425", {"start": v(29.65, -234.84) * mm, "end": v(26.03, -236.94) * mm});
            skLineSegment(sketch, "E1426", {"start": v(26.03, -236.94) * mm, "end": v(21.79, -239.92) * mm});
            skLineSegment(sketch, "E1427", {"start": v(21.79, -239.92) * mm, "end": v(16.87, -242.67) * mm});
            skLineSegment(sketch, "E1428", {"start": v(16.87, -242.67) * mm, "end": v(12.85, -244.94) * mm});
            skLineSegment(sketch, "E1429", {"start": v(12.85, -244.94) * mm, "end": v(6.67, -247.78) * mm});
            skLineSegment(sketch, "E1430", {"start": v(6.67, -247.78) * mm, "end": v(-0.35, -250.21) * mm});
            skLineSegment(sketch, "E1431", {"start": v(-0.35, -250.21) * mm, "end": v(-3.7, -251.09) * mm});
            skLineSegment(sketch, "E1432", {"start": v(-3.7, -251.09) * mm, "end": v(-7.31, -251.72) * mm});
            skLineSegment(sketch, "E1433", {"start": v(-7.31, -251.72) * mm, "end": v(-12.81, -251.72) * mm});
            skLineSegment(sketch, "E1434", {"start": v(-12.81, -251.72) * mm, "end": v(-16.24, -251.57) * mm});
            skLineSegment(sketch, "E1435", {"start": v(-16.24, -251.57) * mm, "end": v(-19.83, -251.05) * mm});
            skLineSegment(sketch, "E1436", {"start": v(-19.83, -251.05) * mm, "end": v(-23.25, -250.03) * mm});
            skLineSegment(sketch, "E1437", {"start": v(-23.25, -250.03) * mm, "end": v(-26.95, -248.25) * mm});
            skLineSegment(sketch, "E1438", {"start": v(-26.95, -248.25) * mm, "end": v(-30.32, -246.03) * mm});
            skLineSegment(sketch, "E1439", {"start": v(-30.32, -246.03) * mm, "end": v(-33.64, -243.33) * mm});
            skLineSegment(sketch, "E1440", {"start": v(-33.64, -243.33) * mm, "end": v(-36.08, -240.84) * mm});
            skLineSegment(sketch, "E1441", {"start": v(-36.08, -240.84) * mm, "end": v(-39.49, -236.75) * mm});
            skLineSegment(sketch, "E1442", {"start": v(-39.49, -236.75) * mm, "end": v(-41.15, -234.39) * mm});
            skLineSegment(sketch, "E1443", {"start": v(-41.15, -234.39) * mm, "end": v(-42.67, -231.39) * mm});
            skLineSegment(sketch, "E1444", {"start": v(-42.67, -231.39) * mm, "end": v(-43.66, -228.67) * mm});
            skLineSegment(sketch, "E1445", {"start": v(-43.66, -228.67) * mm, "end": v(-44.33, -225.68) * mm});
            skLineSegment(sketch, "E1446", {"start": v(-44.33, -225.68) * mm, "end": v(-44.6, -223.35) * mm});
            skLineSegment(sketch, "E1447", {"start": v(-44.6, -223.35) * mm, "end": v(-44.57, -221.63) * mm});
            skLineSegment(sketch, "E1448", {"start": v(-44.57, -221.63) * mm, "end": v(-44.3, -219.78) * mm});
            skLineSegment(sketch, "E1449", {"start": v(-44.3, -219.78) * mm, "end": v(-43.72, -216.97) * mm});
            skLineSegment(sketch, "E1450", {"start": v(-43.72, -216.97) * mm, "end": v(-42.42, -213.67) * mm});
            skLineSegment(sketch, "E1451", {"start": v(-42.42, -213.67) * mm, "end": v(-40.1, -209.7) * mm});
            skLineSegment(sketch, "E1452", {"start": v(-40.1, -209.7) * mm, "end": v(-36.53, -204.98) * mm});
            skLineSegment(sketch, "E1453", {"start": v(-36.53, -204.98) * mm, "end": v(-33.07, -201.78) * mm});
            skLineSegment(sketch, "E1454", {"start": v(-33.07, -201.78) * mm, "end": v(-30.23, -199.41) * mm});
            skLineSegment(sketch, "E1455", {"start": v(-30.23, -199.41) * mm, "end": v(-25.94, -196.78) * mm});
            skLineSegment(sketch, "E1456", {"start": v(-25.94, -196.78) * mm, "end": v(-21.37, -194.96) * mm});
            skLineSegment(sketch, "E1457", {"start": v(-21.37, -194.96) * mm, "end": v(-16.53, -194) * mm});
            skLineSegment(sketch, "E1458", {"start": v(-16.53, -194) * mm, "end": v(-10.45, -193.72) * mm});
            skLineSegment(sketch, "E1459", {"start": v(-10.45, -193.72) * mm, "end": v(-4.56, -194.23) * mm});
            skLineSegment(sketch, "E1460", {"start": v(-4.56, -194.23) * mm, "end": v(-0.43, -195.36) * mm});
            skLineSegment(sketch, "E1461", {"start": v(-0.43, -195.36) * mm, "end": v(4.07, -196.84) * mm});
            skLineSegment(sketch, "E1462", {"start": v(4.07, -196.84) * mm, "end": v(9.3, -199.01) * mm});
            skLineSegment(sketch, "E1463", {"start": v(9.3, -199.01) * mm, "end": v(16.74, -203.08) * mm});
            skLineSegment(sketch, "E1464", {"start": v(16.74, -203.08) * mm, "end": v(28.09, -209.87) * mm});
            skLineSegment(sketch, "E1465", {"start": v(28.09, -209.87) * mm, "end": v(31.5, -211.6) * mm});
            skLineSegment(sketch, "E1466", {"start": v(31.5, -211.6) * mm, "end": v(35.4, -213.15) * mm});
            skLineSegment(sketch, "E1467", {"start": v(35.4, -213.15) * mm, "end": v(39.64, -214.47) * mm});
            skLineSegment(sketch, "E1468", {"start": v(39.64, -214.47) * mm, "end": v(43, -215.72) * mm});
            skLineSegment(sketch, "E1469", {"start": v(43, -215.72) * mm, "end": v(45.38, -216.93) * mm});
            skLineSegment(sketch, "E1470", {"start": v(45.38, -216.93) * mm, "end": v(48.2, -218.7) * mm});
            skLineSegment(sketch, "E1471", {"start": v(48.2, -218.7) * mm, "end": v(50.12, -220.37) * mm});
            skLineSegment(sketch, "E1472", {"start": v(50.12, -220.37) * mm, "end": v(50.7, -221.19) * mm});
            skLineSegment(sketch, "E1473", {"start": v(50.7, -221.19) * mm, "end": v(51.1, -221.93) * mm});
            skLineSegment(sketch, "E1474", {"start": v(51.1, -221.93) * mm, "end": v(51.33, -222.81) * mm});
            skLineSegment(sketch, "E1475", {"start": v(45.2, -222.81) * mm, "end": v(44.91, -223.98) * mm});
            skLineSegment(sketch, "E1476", {"start": v(44.91, -223.98) * mm, "end": v(43.94, -224.93) * mm});
            skLineSegment(sketch, "E1477", {"start": v(43.94, -224.93) * mm, "end": v(42.26, -225.82) * mm});
            skLineSegment(sketch, "E1478", {"start": v(42.26, -225.82) * mm, "end": v(37.34, -227.38) * mm});
            skLineSegment(sketch, "E1479", {"start": v(37.34, -227.38) * mm, "end": v(34.4, -228.41) * mm});
            skLineSegment(sketch, "E1480", {"start": v(34.4, -228.41) * mm, "end": v(32.04, -229.57) * mm});
            skLineSegment(sketch, "E1481", {"start": v(32.04, -229.57) * mm, "end": v(28.98, -231.09) * mm});
            skLineSegment(sketch, "E1482", {"start": v(28.98, -231.09) * mm, "end": v(22.57, -235.17) * mm});
            skLineSegment(sketch, "E1483", {"start": v(22.57, -235.17) * mm, "end": v(17.31, -238.47) * mm});
            skLineSegment(sketch, "E1484", {"start": v(17.31, -238.47) * mm, "end": v(13.5, -240.62) * mm});
            skLineSegment(sketch, "E1485", {"start": v(13.5, -240.62) * mm, "end": v(8.8, -242.91) * mm});
            skLineSegment(sketch, "E1486", {"start": v(8.8, -242.91) * mm, "end": v(4.86, -244.29) * mm});
            skLineSegment(sketch, "E1487", {"start": v(4.86, -244.29) * mm, "end": v(-2.72, -246.51) * mm});
            skLineSegment(sketch, "E1488", {"start": v(-2.72, -246.51) * mm, "end": v(-6.65, -246.9) * mm});
            skLineSegment(sketch, "E1489", {"start": v(-6.65, -246.9) * mm, "end": v(-10.44, -246.96) * mm});
            skLineSegment(sketch, "E1490", {"start": v(-10.44, -246.96) * mm, "end": v(-14.08, -246.53) * mm});
            skLineSegment(sketch, "E1491", {"start": v(-14.08, -246.53) * mm, "end": v(-17.6, -245.8) * mm});
            skLineSegment(sketch, "E1492", {"start": v(-17.6, -245.8) * mm, "end": v(-21.4, -244.7) * mm});
            skLineSegment(sketch, "E1493", {"start": v(-21.4, -244.7) * mm, "end": v(-24.47, -243.03) * mm});
            skLineSegment(sketch, "E1494", {"start": v(-24.47, -243.03) * mm, "end": v(-27.02, -241.13) * mm});
            skLineSegment(sketch, "E1495", {"start": v(-27.02, -241.13) * mm, "end": v(-29.54, -238.56) * mm});
            skLineSegment(sketch, "E1496", {"start": v(-29.54, -238.56) * mm, "end": v(-31.45, -236.28) * mm});
            skLineSegment(sketch, "E1497", {"start": v(-31.45, -236.28) * mm, "end": v(-33.4, -233.09) * mm});
            skLineSegment(sketch, "E1498", {"start": v(-33.4, -233.09) * mm, "end": v(-34.2, -231.68) * mm});
            skLineSegment(sketch, "E1499", {"start": v(-34.2, -231.68) * mm, "end": v(-35.2, -229.2) * mm});
            skLineSegment(sketch, "E1500", {"start": v(-35.2, -229.2) * mm, "end": v(-35.86, -227.6) * mm});
            skLineSegment(sketch, "E1501", {"start": v(-35.86, -227.6) * mm, "end": v(-36.31, -223.95) * mm});
            skLineSegment(sketch, "E1502", {"start": v(-36.31, -223.95) * mm, "end": v(-36.31, -221.55) * mm});
            skLineSegment(sketch, "E1503", {"start": v(-36.31, -221.55) * mm, "end": v(-35.78, -217.95) * mm});
            skLineSegment(sketch, "E1504", {"start": v(-35.78, -217.95) * mm, "end": v(-34.83, -215.38) * mm});
            skLineSegment(sketch, "E1505", {"start": v(-34.83, -215.38) * mm, "end": v(-33.83, -213.12) * mm});
            skLineSegment(sketch, "E1506", {"start": v(-33.83, -213.12) * mm, "end": v(-31.92, -209.97) * mm});
            skLineSegment(sketch, "E1507", {"start": v(-31.92, -209.97) * mm, "end": v(-29.21, -206.66) * mm});
            skLineSegment(sketch, "E1508", {"start": v(-29.21, -206.66) * mm, "end": v(-27.1, -204.55) * mm});
            skLineSegment(sketch, "E1509", {"start": v(-27.1, -204.55) * mm, "end": v(-25.18, -203.09) * mm});
            skLineSegment(sketch, "E1510", {"start": v(-25.18, -203.09) * mm, "end": v(-23.42, -201.93) * mm});
            skLineSegment(sketch, "E1511", {"start": v(-23.42, -201.93) * mm, "end": v(-20.89, -200.76) * mm});
            skLineSegment(sketch, "E1512", {"start": v(-20.89, -200.76) * mm, "end": v(-17.61, -199.62) * mm});
            skLineSegment(sketch, "E1513", {"start": v(-17.61, -199.62) * mm, "end": v(-12.18, -198.85) * mm});
            skLineSegment(sketch, "E1514", {"start": v(-12.18, -198.85) * mm, "end": v(-9.37, -198.6) * mm});
            skLineSegment(sketch, "E1515", {"start": v(-9.37, -198.6) * mm, "end": v(-5.95, -198.7) * mm});
            skLineSegment(sketch, "E1516", {"start": v(-5.95, -198.7) * mm, "end": v(-2.33, -199.26) * mm});
            skLineSegment(sketch, "E1517", {"start": v(-2.33, -199.26) * mm, "end": v(1.35, -200.26) * mm});
            skLineSegment(sketch, "E1518", {"start": v(1.35, -200.26) * mm, "end": v(6, -201.73) * mm});
            skLineSegment(sketch, "E1519", {"start": v(6, -201.73) * mm, "end": v(8.54, -202.75) * mm});
            skLineSegment(sketch, "E1520", {"start": v(8.54, -202.75) * mm, "end": v(11.42, -204.1) * mm});
            skLineSegment(sketch, "E1521", {"start": v(11.42, -204.1) * mm, "end": v(19.13, -208.43) * mm});
            skLineSegment(sketch, "E1522", {"start": v(19.13, -208.43) * mm, "end": v(22.6, -210.34) * mm});
            skLineSegment(sketch, "E1523", {"start": v(22.6, -210.34) * mm, "end": v(26.1, -212.48) * mm});
            skLineSegment(sketch, "E1524", {"start": v(26.1, -212.48) * mm, "end": v(29.48, -214.63) * mm});
            skLineSegment(sketch, "E1525", {"start": v(29.48, -214.63) * mm, "end": v(31.53, -215.9) * mm});
            skLineSegment(sketch, "E1526", {"start": v(31.53, -215.9) * mm, "end": v(33.67, -216.92) * mm});
            skLineSegment(sketch, "E1527", {"start": v(33.67, -216.92) * mm, "end": v(35.62, -217.7) * mm});
            skLineSegment(sketch, "E1528", {"start": v(35.62, -217.7) * mm, "end": v(37.97, -218.42) * mm});
            skLineSegment(sketch, "E1529", {"start": v(37.97, -218.42) * mm, "end": v(40, -219.04) * mm});
            skLineSegment(sketch, "E1530", {"start": v(40, -219.04) * mm, "end": v(42.38, -219.84) * mm});
            skLineSegment(sketch, "E1531", {"start": v(42.38, -219.84) * mm, "end": v(43.64, -220.4) * mm});
            skLineSegment(sketch, "E1532", {"start": v(43.64, -220.4) * mm, "end": v(44.47, -221.14) * mm});
            skLineSegment(sketch, "E1533", {"start": v(44.47, -221.14) * mm, "end": v(44.97, -221.82) * mm});
            skLineSegment(sketch, "E1534", {"start": v(44.97, -221.82) * mm, "end": v(45.2, -222.81) * mm});
            skLineSegment(sketch, "E1535", {"start": v(31.67, -222.81) * mm, "end": v(31.52, -223.65) * mm});
            skLineSegment(sketch, "E1536", {"start": v(31.52, -223.65) * mm, "end": v(28.53, -226.77) * mm});
            skLineSegment(sketch, "E1537", {"start": v(28.53, -226.77) * mm, "end": v(25.31, -229.48) * mm});
            skLineSegment(sketch, "E1538", {"start": v(25.31, -229.48) * mm, "end": v(22.29, -231.54) * mm});
            skLineSegment(sketch, "E1539", {"start": v(22.29, -231.54) * mm, "end": v(14.6, -235.69) * mm});
            skLineSegment(sketch, "E1540", {"start": v(14.6, -235.69) * mm, "end": v(10.5, -237.14) * mm});
            skLineSegment(sketch, "E1541", {"start": v(10.5, -237.14) * mm, "end": v(1.99, -239.32) * mm});
            skLineSegment(sketch, "E1542", {"start": v(1.99, -239.32) * mm, "end": v(-3.35, -240.68) * mm});
            skLineSegment(sketch, "E1543", {"start": v(-3.35, -240.68) * mm, "end": v(-6.03, -241.1) * mm});
            skLineSegment(sketch, "E1544", {"start": v(-6.03, -241.1) * mm, "end": v(-8.04, -241.2) * mm});
            skLineSegment(sketch, "E1545", {"start": v(-8.04, -241.2) * mm, "end": v(-10.44, -241) * mm});
            skLineSegment(sketch, "E1546", {"start": v(-10.44, -241) * mm, "end": v(-15.24, -239.92) * mm});
            skLineSegment(sketch, "E1547", {"start": v(-15.24, -239.92) * mm, "end": v(-18.14, -238.99) * mm});
            skLineSegment(sketch, "E1548", {"start": v(-18.14, -238.99) * mm, "end": v(-20.38, -238.01) * mm});
            skLineSegment(sketch, "E1549", {"start": v(-20.38, -238.01) * mm, "end": v(-22.03, -237.09) * mm});
            skLineSegment(sketch, "E1550", {"start": v(-22.03, -237.09) * mm, "end": v(-23.74, -235.94) * mm});
            skLineSegment(sketch, "E1551", {"start": v(-23.74, -235.94) * mm, "end": v(-25.39, -234.48) * mm});
            skLineSegment(sketch, "E1552", {"start": v(-25.39, -234.48) * mm, "end": v(-26.9, -232.61) * mm});
            skLineSegment(sketch, "E1553", {"start": v(-26.9, -232.61) * mm, "end": v(-27.9, -230.95) * mm});
            skLineSegment(sketch, "E1554", {"start": v(-27.9, -230.95) * mm, "end": v(-28.73, -229.06) * mm});
            skLineSegment(sketch, "E1555", {"start": v(-28.73, -229.06) * mm, "end": v(-29.77, -225.56) * mm});
            skLineSegment(sketch, "E1556", {"start": v(-29.77, -225.56) * mm, "end": v(-30.1, -224.02) * mm});
            skLineSegment(sketch, "E1557", {"start": v(-30.1, -224.02) * mm, "end": v(-30.06, -221.96) * mm});
            skLineSegment(sketch, "E1558", {"start": v(-30.06, -221.96) * mm, "end": v(-29.91, -220.5) * mm});
            skLineSegment(sketch, "E1559", {"start": v(-29.91, -220.5) * mm, "end": v(-29.16, -217.64) * mm});
            skLineSegment(sketch, "E1560", {"start": v(-29.16, -217.64) * mm, "end": v(-28.31, -215.66) * mm});
            skLineSegment(sketch, "E1561", {"start": v(-28.31, -215.66) * mm, "end": v(-27.27, -213.56) * mm});
            skLineSegment(sketch, "E1562", {"start": v(-27.27, -213.56) * mm, "end": v(-26.1, -211.91) * mm});
            skLineSegment(sketch, "E1563", {"start": v(-26.1, -211.91) * mm, "end": v(-24.22, -210.1) * mm});
            skLineSegment(sketch, "E1564", {"start": v(-24.22, -210.1) * mm, "end": v(-22.25, -208.6) * mm});
            skLineSegment(sketch, "E1565", {"start": v(-22.25, -208.6) * mm, "end": v(-20.05, -207.44) * mm});
            skLineSegment(sketch, "E1566", {"start": v(-20.05, -207.44) * mm, "end": v(-16.53, -206.1) * mm});
            skLineSegment(sketch, "E1567", {"start": v(-16.53, -206.1) * mm, "end": v(-10.5, -204.62) * mm});
            skLineSegment(sketch, "E1568", {"start": v(-10.5, -204.62) * mm, "end": v(-7.6, -204.45) * mm});
            skLineSegment(sketch, "E1569", {"start": v(-7.6, -204.45) * mm, "end": v(-4.36, -204.7) * mm});
            skLineSegment(sketch, "E1570", {"start": v(-4.36, -204.7) * mm, "end": v(6.55, -207.36) * mm});
            skLineSegment(sketch, "E1571", {"start": v(6.55, -207.36) * mm, "end": v(10.2, -208.4) * mm});
            skLineSegment(sketch, "E1572", {"start": v(10.2, -208.4) * mm, "end": v(13.5, -209.62) * mm});
            skLineSegment(sketch, "E1573", {"start": v(13.5, -209.62) * mm, "end": v(17.58, -211.55) * mm});
            skLineSegment(sketch, "E1574", {"start": v(17.58, -211.55) * mm, "end": v(20.89, -213.4) * mm});
            skLineSegment(sketch, "E1575", {"start": v(20.89, -213.4) * mm, "end": v(24.8, -215.78) * mm});
            skLineSegment(sketch, "E1576", {"start": v(24.8, -215.78) * mm, "end": v(27.76, -218.28) * mm});
            skLineSegment(sketch, "E1577", {"start": v(27.76, -218.28) * mm, "end": v(30.22, -220.53) * mm});
            skLineSegment(sketch, "E1578", {"start": v(30.22, -220.53) * mm, "end": v(31.44, -221.78) * mm});
            skLineSegment(sketch, "E1579", {"start": v(31.44, -221.78) * mm, "end": v(31.67, -222.81) * mm});
            skLineSegment(sketch, "E1580", {"start": v(20.54, -222.81) * mm, "end": v(20.54, -224.06) * mm});
            skLineSegment(sketch, "E1581", {"start": v(20.54, -224.06) * mm, "end": v(20.34, -225.05) * mm});
            skLineSegment(sketch, "E1582", {"start": v(20.34, -225.05) * mm, "end": v(19.6, -226.41) * mm});
            skLineSegment(sketch, "E1583", {"start": v(19.6, -226.41) * mm, "end": v(18.36, -227.46) * mm});
            skLineSegment(sketch, "E1584", {"start": v(18.36, -227.46) * mm, "end": v(11.94, -229.55) * mm});
            skLineSegment(sketch, "E1585", {"start": v(11.94, -229.55) * mm, "end": v(5.3, -231.03) * mm});
            skLineSegment(sketch, "E1586", {"start": v(5.3, -231.03) * mm, "end": v(0.44, -231.7) * mm});
            skLineSegment(sketch, "E1587", {"start": v(0.44, -231.7) * mm, "end": v(-3.82, -232.42) * mm});
            skLineSegment(sketch, "E1588", {"start": v(-3.82, -232.42) * mm, "end": v(-8.09, -232.42) * mm});
            skLineSegment(sketch, "E1589", {"start": v(-8.09, -232.42) * mm, "end": v(-9.8, -232.1) * mm});
            skLineSegment(sketch, "E1590", {"start": v(-9.8, -232.1) * mm, "end": v(-13.13, -231.07) * mm});
            skLineSegment(sketch, "E1591", {"start": v(-13.13, -231.07) * mm, "end": v(-16.47, -229.35) * mm});
            skLineSegment(sketch, "E1592", {"start": v(-16.47, -229.35) * mm, "end": v(-18.91, -227.6) * mm});
            skLineSegment(sketch, "E1593", {"start": v(-18.91, -227.6) * mm, "end": v(-20.24, -226.24) * mm});
            skLineSegment(sketch, "E1594", {"start": v(-20.24, -226.24) * mm, "end": v(-21.3, -225.03) * mm});
            skLineSegment(sketch, "E1595", {"start": v(-21.3, -225.03) * mm, "end": v(-21.86, -223.68) * mm});
            skLineSegment(sketch, "E1596", {"start": v(-21.86, -223.68) * mm, "end": v(-21.9, -222.1) * mm});
            skLineSegment(sketch, "E1597", {"start": v(-21.9, -222.1) * mm, "end": v(-21.31, -220.84) * mm});
            skLineSegment(sketch, "E1598", {"start": v(-21.31, -220.84) * mm, "end": v(-20.38, -219.47) * mm});
            skLineSegment(sketch, "E1599", {"start": v(-20.38, -219.47) * mm, "end": v(-18.01, -217.34) * mm});
            skLineSegment(sketch, "E1600", {"start": v(-18.01, -217.34) * mm, "end": v(-15.78, -215.82) * mm});
            skLineSegment(sketch, "E1601", {"start": v(-15.78, -215.82) * mm, "end": v(-12.9, -214.27) * mm});
            skLineSegment(sketch, "E1602", {"start": v(-12.9, -214.27) * mm, "end": v(-9.87, -213.6) * mm});
            skLineSegment(sketch, "E1603", {"start": v(-9.87, -213.6) * mm, "end": v(-6.85, -213.1) * mm});
            skLineSegment(sketch, "E1604", {"start": v(-6.85, -213.1) * mm, "end": v(-3.84, -212.97) * mm});
            skLineSegment(sketch, "E1605", {"start": v(-3.84, -212.97) * mm, "end": v(-0.15, -213.2) * mm});
            skLineSegment(sketch, "E1606", {"start": v(-0.15, -213.2) * mm, "end": v(4.69, -213.92) * mm});
            skLineSegment(sketch, "E1607", {"start": v(4.69, -213.92) * mm, "end": v(9.47, -214.95) * mm});
            skLineSegment(sketch, "E1608", {"start": v(9.47, -214.95) * mm, "end": v(13.33, -216.16) * mm});
            skLineSegment(sketch, "E1609", {"start": v(13.33, -216.16) * mm, "end": v(17.04, -217.78) * mm});
            skLineSegment(sketch, "E1610", {"start": v(17.04, -217.78) * mm, "end": v(18.6, -218.5) * mm});
            skLineSegment(sketch, "E1611", {"start": v(18.6, -218.5) * mm, "end": v(19.81, -219.87) * mm});
            skLineSegment(sketch, "E1612", {"start": v(19.81, -219.87) * mm, "end": v(20.36, -221.27) * mm});
            skLineSegment(sketch, "E1613", {"start": v(20.36, -221.27) * mm, "end": v(20.54, -222.81) * mm});
            skSolve(sketch);
        }
        {
            var Q0;
            Q0=makeQuery(id+"F0.imprint","IMPRINT",FACE,{"disambiguationData":[TD([[makeQuery(id+"F0.imprint","IMPRINT",EDGE,{"derivedFrom":sQuery(id+"F0.wireOp",EDGE,"E19.MirrorCS")}),1.0]])]});
            var Q1;
            Q1=makeQuery(id+"F0.imprint","IMPRINT",FACE,{"disambiguationData":[TD([[makeQuery(id+"F0.imprint","IMPRINT",EDGE,{"derivedFrom":sQuery(id+"F0.wireOp",EDGE,"E203.MirrorCS")}),1.0]])]});
            var Q2;
            Q2=makeQuery(id+"F0.imprint","IMPRINT",FACE,{"disambiguationData":[TD([[makeQuery(id+"F0.imprint","IMPRINT",EDGE,{"derivedFrom":sQuery(id+"F0.wireOp",EDGE,"E184.MirrorCS")}),1.0]])]});
            var Q3;
            {var subQ0=sQuery(id+"F0.wireOp",EDGE,"E197.MirrorCS");Q3=makeQuery(id+"F0.imprint","IMPRINT",FACE,{"disambiguationData":[TD([[makeQuery(id+"F0.imprint","IMPRINT",EDGE,{"derivedFrom":subQ0}),-1.0]])]});}
            var Q4;
            {var subQ5=sQuery(id+"F0.wireOp",EDGE,"E33.MirrorCS");Q4=makeQuery(id+"F0.imprint","IMPRINT",FACE,{"disambiguationData":[TD([[makeQuery(id+"F0.imprint","IMPRINT",EDGE,{"derivedFrom":subQ5}),-1.0]])]});}
            var Q5;
            Q5=makeQuery(id+"F0.imprint","IMPRINT",FACE,{"disambiguationData":[TD([[makeQuery(id+"F0.imprint","IMPRINT",EDGE,{"derivedFrom":sQuery(id+"F0.wireOp",EDGE,"E3.MirrorCS")}),1.0]])]});
            var Q6;
            Q6=makeQuery(id+"F0.imprint","IMPRINT",FACE,{"disambiguationData":[TD([[makeQuery(id+"F0.imprint","IMPRINT",EDGE,{"derivedFrom":sQuery(id+"F0.wireOp",EDGE,"E0.MirrorCS")}),1.0]])]});
            var Q7;
            Q7=makeQuery(id+"F0.imprint","IMPRINT",FACE,{"disambiguationData":[TD([[makeQuery(id+"F0.imprint","IMPRINT",EDGE,{"derivedFrom":sQuery(id+"F0.wireOp",EDGE,"E11.MirrorCS")}),1.0]])]});
            extrude(context, id + "F1", {"entities" : qUnion([Q0, Q1, Q2, Q3, Q4, Q5, Q6, Q7]), "depth" : 5 * mm, "offsetDistance" : 25 * mm});
        }
        {
            var Q0;
            Q0=makeQuery(id+"F0.imprint","IMPRINT",FACE,{"disambiguationData":[TD([[makeQuery(id+"F0.imprint","IMPRINT",EDGE,{"derivedFrom":sQuery(id+"F0.wireOp",EDGE,"E22.MirrorCS")}),1.0]])]});
            extrude(context, id + "F2", {"entities" : qUnion([Q0]), "operationType" : NewBodyOperationType.ADD, "depth" : 6 * mm, "offsetDistance" : 25 * mm});
        }
        {
            var Q0;
            Q0=makeQuery(id+"F0.imprint","IMPRINT",FACE,{"disambiguationData":[TD([[makeQuery(id+"F0.imprint","IMPRINT",EDGE,{"derivedFrom":sQuery(id+"F0.wireOp",EDGE,"E847")}),-1.0]])]});
            var Q1;
            Q1=makeQuery(id+"F0.imprint","IMPRINT",FACE,{"disambiguationData":[TD([[makeQuery(id+"F0.imprint","IMPRINT",EDGE,{"derivedFrom":sQuery(id+"F0.wireOp",EDGE,"E68.MirrorCS")}),1.0]])]});
            extrude(context, id + "F3", {"entities" : qUnion([Q0, Q1]), "operationType" : NewBodyOperationType.ADD, "depth" : 7 * mm, "offsetDistance" : 25 * mm});
        }
        {
            var Q0;
            Q0=makeQuery(id+"F0.imprint","IMPRINT",FACE,{"disambiguationData":[TD([[makeQuery(id+"F0.imprint","IMPRINT",EDGE,{"derivedFrom":sQuery(id+"F0.wireOp",EDGE,"E957.0")}),-1.0]])]});
            var Q1;
            {var subQ4=sQuery(id+"F0.wireOp",EDGE,"E197.MirrorCS");Q1=makeQuery(id+"F0.imprint","IMPRINT",FACE,{"disambiguationData":[TD([[makeQuery(id+"F0.imprint","IMPRINT",EDGE,{"derivedFrom":subQ4}),1.0]])]});}
            extrude(context, id + "F4", {"entities" : qUnion([Q0, Q1]), "operationType" : NewBodyOperationType.ADD, "depth" : 8 * mm, "offsetDistance" : 25 * mm});
        }
        {
            var Q0;
            Q0=makeQuery(id+"F0.imprint","IMPRINT",FACE,{"disambiguationData":[TD([[makeQuery(id+"F0.imprint","IMPRINT",EDGE,{"derivedFrom":sQuery(id+"F0.wireOp",EDGE,"E1052")}),-1.0]])]});
            var Q1;
            {var subQ6=sQuery(id+"F0.wireOp",EDGE,"E33.MirrorCS");Q1=makeQuery(id+"F0.imprint","IMPRINT",FACE,{"disambiguationData":[TD([[makeQuery(id+"F0.imprint","IMPRINT",EDGE,{"derivedFrom":subQ6}),1.0]])]});}
            extrude(context, id + "F5", {"entities" : qUnion([Q0, Q1]), "operationType" : NewBodyOperationType.ADD, "depth" : 9 * mm, "offsetDistance" : 25 * mm});
        }
        {
            var Q0;
            Q0=makeQuery(id+"F0.imprint","IMPRINT",FACE,{"disambiguationData":[TD([[makeQuery(id+"F0.imprint","IMPRINT",EDGE,{"derivedFrom":sQuery(id+"F0.wireOp",EDGE,"E1143")}),-1.0]])]});
            var Q1;
            Q1=makeQuery(id+"F0.imprint","IMPRINT",FACE,{"disambiguationData":[TD([[makeQuery(id+"F0.imprint","IMPRINT",EDGE,{"derivedFrom":sQuery(id+"F0.wireOp",EDGE,"E80.MirrorCS")}),1.0]])]});
            extrude(context, id + "F6", {"entities" : qUnion([Q0, Q1]), "operationType" : NewBodyOperationType.ADD, "depth" : 10 * mm, "offsetDistance" : 25 * mm});
        }
        {
            var Q0;
            Q0=makeQuery(id+"F0.imprint","IMPRINT",FACE,{"disambiguationData":[TD([[makeQuery(id+"F0.imprint","IMPRINT",EDGE,{"derivedFrom":sQuery(id+"F0.wireOp",EDGE,"E1219")}),-1.0]])]});
            var Q1;
            Q1=makeQuery(id+"F0.imprint","IMPRINT",FACE,{"disambiguationData":[TD([[makeQuery(id+"F0.imprint","IMPRINT",EDGE,{"derivedFrom":sQuery(id+"F0.wireOp",EDGE,"E6.MirrorCS")}),1.0]])]});
            extrude(context, id + "F7", {"entities" : qUnion([Q0, Q1]), "operationType" : NewBodyOperationType.ADD, "depth" : 11 * mm, "offsetDistance" : 25 * mm});
        }
        {
            var Q0;
            Q0=makeQuery(id+"F0.imprint","IMPRINT",FACE,{"disambiguationData":[TD([[makeQuery(id+"F0.imprint","IMPRINT",EDGE,{"derivedFrom":sQuery(id+"F0.wireOp",EDGE,"E1291")}),-1.0]])]});
            var Q1;
            Q1=makeQuery(id+"F0.imprint","IMPRINT",FACE,{"disambiguationData":[TD([[makeQuery(id+"F0.imprint","IMPRINT",EDGE,{"derivedFrom":sQuery(id+"F0.wireOp",EDGE,"E2.MirrorCS")}),1.0]])]});
            extrude(context, id + "F8", {"entities" : qUnion([Q0, Q1]), "operationType" : NewBodyOperationType.ADD, "depth" : 12 * mm, "offsetDistance" : 25 * mm});
        }
        {
            var Q0;
            Q0=makeQuery(id+"F0.imprint","IMPRINT",FACE,{"disambiguationData":[TD([[makeQuery(id+"F0.imprint","IMPRINT",EDGE,{"derivedFrom":sQuery(id+"F0.wireOp",EDGE,"E1353")}),-1.0]])]});
            extrude(context, id + "F9", {"entities" : qUnion([Q0]), "operationType" : NewBodyOperationType.ADD, "depth" : 13 * mm, "offsetDistance" : 25 * mm});
        }
        {
            var Q0;
            Q0=makeQuery(id+"F0.imprint","IMPRINT",FACE,{"disambiguationData":[TD([[makeQuery(id+"F0.imprint","IMPRINT",EDGE,{"derivedFrom":sQuery(id+"F0.wireOp",EDGE,"E1418")}),-1.0]])]});
            extrude(context, id + "F10", {"entities" : qUnion([Q0]), "operationType" : NewBodyOperationType.ADD, "depth" : 14 * mm, "offsetDistance" : 25 * mm});
        }
        {
            var Q0;
            Q0=makeQuery(id+"F0.imprint","IMPRINT",FACE,{"disambiguationData":[TD([[makeQuery(id+"F0.imprint","IMPRINT",EDGE,{"derivedFrom":sQuery(id+"F0.wireOp",EDGE,"E1475")}),-1.0]])]});
            extrude(context, id + "F11", {"entities" : qUnion([Q0]), "operationType" : NewBodyOperationType.ADD, "depth" : 15 * mm, "offsetDistance" : 25 * mm});
        }
        {
            var Q0;
            Q0=makeQuery(id+"F0.imprint","IMPRINT",FACE,{"disambiguationData":[TD([[makeQuery(id+"F0.imprint","IMPRINT",EDGE,{"derivedFrom":sQuery(id+"F0.wireOp",EDGE,"E1535")}),-1.0]])]});
            extrude(context, id + "F12", {"entities" : qUnion([Q0]), "operationType" : NewBodyOperationType.ADD, "depth" : 16 * mm, "offsetDistance" : 25 * mm});
        }
        {
            var Q0;
            Q0=makeQuery(id+"F0.imprint","IMPRINT",FACE,{"disambiguationData":[TD([[makeQuery(id+"F0.imprint","IMPRINT",EDGE,{"derivedFrom":sQuery(id+"F0.wireOp",EDGE,"E1580")}),-1.0]])]});
            extrude(context, id + "F13", {"entities" : qUnion([Q0]), "operationType" : NewBodyOperationType.ADD, "depth" : 17 * mm, "offsetDistance" : 25 * mm});
        }
    });
